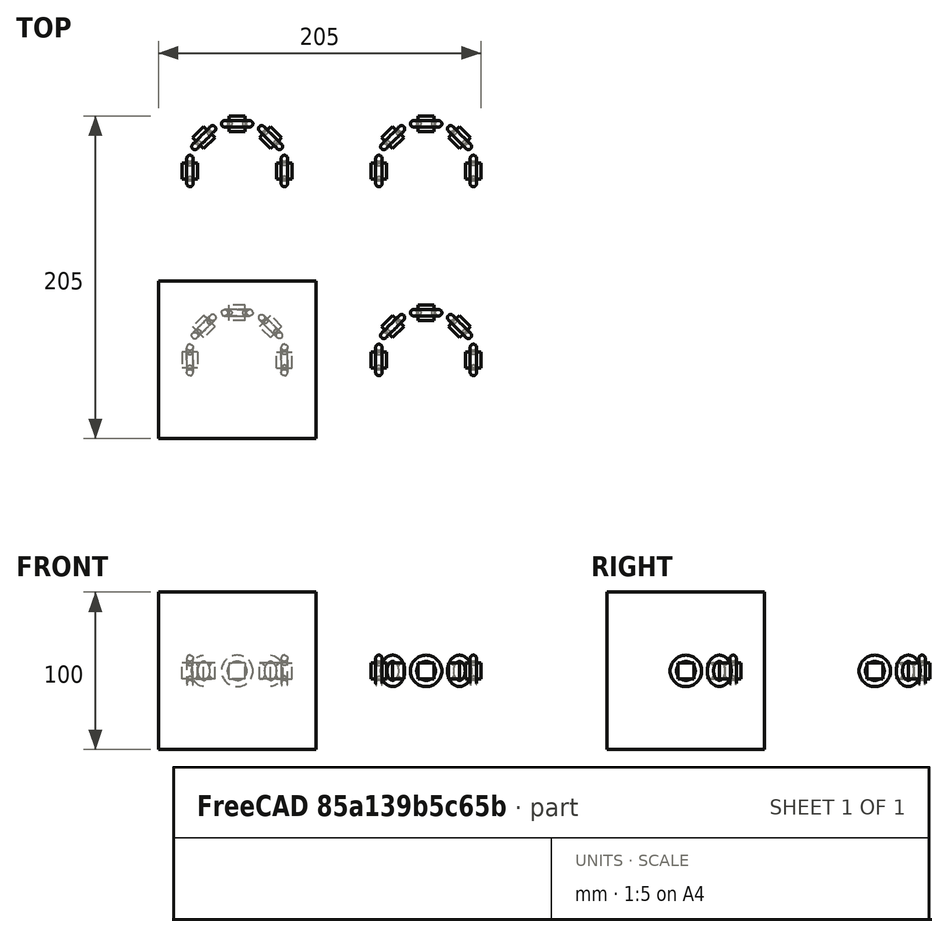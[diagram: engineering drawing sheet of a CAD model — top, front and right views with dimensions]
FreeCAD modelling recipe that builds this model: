
FCSTD DOCUMENT  (FreeCAD 1.0R39109 (Git))
Label: array-of-array-of-solid
License: All rights reserved
objects: App::DocumentObjectGroupPython×1251, Part::FeaturePython×5, App::Part×2, Part::MultiFuse×1
note: 5 computed .brp shape members not serialized (recipe doc carries the construction recipe); baked Part::Feature solids carry a one-line shape summary decoded from their .brp

FEATURE [App::DocumentObjectGroupPython] HALFPI  # scripted group (container) (typed FeaturePython)
  name = HALFPI
  value = pi/2.
FEATURE [App::DocumentObjectGroupPython] PI  # scripted group (container) (typed FeaturePython)
  name = PI
  value = 1.*pi
FEATURE [App::DocumentObjectGroupPython] TWOPI  # scripted group (container) (typed FeaturePython)
  name = TWOPI
  value = 2.*pi
FEATURE [App::DocumentObjectGroupPython] Constants  # scripted group (container) (typed FeaturePython)
  Group = -> [HALFPI,PI,TWOPI]
FEATURE [App::DocumentObjectGroupPython] Variables  # scripted group (container) (typed FeaturePython)
FEATURE [App::DocumentObjectGroupPython] Quantities  # scripted group (container) (typed FeaturePython)
FEATURE [App::DocumentObjectGroupPython] Isotopes  # scripted group (container) (typed FeaturePython)
FEATURE [App::DocumentObjectGroupPython] Elements  # scripted group (container) (typed FeaturePython)
FEATURE [App::DocumentObjectGroupPython] Matrix  # scripted group (container) (typed FeaturePython)
FEATURE [App::DocumentObjectGroupPython] Surfaces  # scripted group (container) (typed FeaturePython)
FEATURE [App::DocumentObjectGroupPython] Opticals  # scripted group (container) (typed FeaturePython)
  Group = -> [Matrix,Surfaces]
FEATURE [App::DocumentObjectGroupPython] G4Isotopes  # scripted group (container) (typed FeaturePython)
FEATURE [App::DocumentObjectGroupPython] H_element  # scripted group (container) (typed FeaturePython)
  Z = 1
  atom_value = 1.008
  formula = H
  name = H_element
FEATURE [App::DocumentObjectGroupPython] He_element  # scripted group (container) (typed FeaturePython)
  Z = 2
  atom_value = 4.0026
  formula = He
  name = He_element
FEATURE [App::DocumentObjectGroupPython] Li_element  # scripted group (container) (typed FeaturePython)
  Z = 3
  atom_value = 6.94
  formula = Li
  name = Li_element
FEATURE [App::DocumentObjectGroupPython] Be_element  # scripted group (container) (typed FeaturePython)
  Z = 4
  atom_value = 9.01218
  formula = Be
  name = Be_element
FEATURE [App::DocumentObjectGroupPython] B_element  # scripted group (container) (typed FeaturePython)
  Z = 5
  atom_value = 10.81
  formula = B
  name = B_element
FEATURE [App::DocumentObjectGroupPython] C_element  # scripted group (container) (typed FeaturePython)
  Z = 6
  atom_value = 12.011
  formula = C
  name = C_element
FEATURE [App::DocumentObjectGroupPython] N_element  # scripted group (container) (typed FeaturePython)
  Z = 7
  atom_value = 14.007
  formula = N
  name = N_element
FEATURE [App::DocumentObjectGroupPython] O_element  # scripted group (container) (typed FeaturePython)
  Z = 8
  atom_value = 15.999
  formula = O
  name = O_element
FEATURE [App::DocumentObjectGroupPython] F_element  # scripted group (container) (typed FeaturePython)
  Z = 9
  atom_value = 18.9984
  formula = F
  name = F_element
FEATURE [App::DocumentObjectGroupPython] Ne_element  # scripted group (container) (typed FeaturePython)
  Z = 10
  atom_value = 20.1797
  formula = Ne
  name = Ne_element
FEATURE [App::DocumentObjectGroupPython] Na_element  # scripted group (container) (typed FeaturePython)
  Z = 11
  atom_value = 22.9898
  formula = Na
  name = Na_element
FEATURE [App::DocumentObjectGroupPython] Mg_element  # scripted group (container) (typed FeaturePython)
  Z = 12
  atom_value = 24.305
  formula = Mg
  name = Mg_element
FEATURE [App::DocumentObjectGroupPython] Al_element  # scripted group (container) (typed FeaturePython)
  Z = 13
  atom_value = 26.9815
  formula = Al
  name = Al_element
FEATURE [App::DocumentObjectGroupPython] Si_element  # scripted group (container) (typed FeaturePython)
  Z = 14
  atom_value = 28.085
  formula = Si
  name = Si_element
FEATURE [App::DocumentObjectGroupPython] P_element  # scripted group (container) (typed FeaturePython)
  Z = 15
  atom_value = 30.9738
  formula = P
  name = P_element
FEATURE [App::DocumentObjectGroupPython] S_element  # scripted group (container) (typed FeaturePython)
  Z = 16
  atom_value = 32.06
  formula = S
  name = S_element
FEATURE [App::DocumentObjectGroupPython] Cl_element  # scripted group (container) (typed FeaturePython)
  Z = 17
  atom_value = 35.45
  formula = Cl
  name = Cl_element
FEATURE [App::DocumentObjectGroupPython] Ar_element  # scripted group (container) (typed FeaturePython)
  Z = 18
  atom_value = 39.95
  formula = Ar
  name = Ar_element
FEATURE [App::DocumentObjectGroupPython] K_element  # scripted group (container) (typed FeaturePython)
  Z = 19
  atom_value = 39.0983
  formula = K
  name = K_element
FEATURE [App::DocumentObjectGroupPython] Ca_element  # scripted group (container) (typed FeaturePython)
  Z = 20
  atom_value = 40.078
  formula = Ca
  name = Ca_element
FEATURE [App::DocumentObjectGroupPython] Sc_element  # scripted group (container) (typed FeaturePython)
  Z = 21
  atom_value = 44.9559
  formula = Sc
  name = Sc_element
FEATURE [App::DocumentObjectGroupPython] Ti_element  # scripted group (container) (typed FeaturePython)
  Z = 22
  atom_value = 47.867
  formula = Ti
  name = Ti_element
FEATURE [App::DocumentObjectGroupPython] V_element  # scripted group (container) (typed FeaturePython)
  Z = 23
  atom_value = 50.9415
  formula = V
  name = V_element
FEATURE [App::DocumentObjectGroupPython] Cr_element  # scripted group (container) (typed FeaturePython)
  Z = 24
  atom_value = 51.9961
  formula = Cr
  name = Cr_element
FEATURE [App::DocumentObjectGroupPython] Mn_element  # scripted group (container) (typed FeaturePython)
  Z = 25
  atom_value = 54.938
  formula = Mn
  name = Mn_element
FEATURE [App::DocumentObjectGroupPython] Fe_element  # scripted group (container) (typed FeaturePython)
  Z = 26
  atom_value = 55.845
  formula = Fe
  name = Fe_element
FEATURE [App::DocumentObjectGroupPython] Co_element  # scripted group (container) (typed FeaturePython)
  Z = 27
  atom_value = 58.9332
  formula = Co
  name = Co_element
FEATURE [App::DocumentObjectGroupPython] Ni_element  # scripted group (container) (typed FeaturePython)
  Z = 28
  atom_value = 58.6934
  formula = Ni
  name = Ni_element
FEATURE [App::DocumentObjectGroupPython] Cu_element  # scripted group (container) (typed FeaturePython)
  Z = 29
  atom_value = 63.546
  formula = Cu
  name = Cu_element
FEATURE [App::DocumentObjectGroupPython] Zn_element  # scripted group (container) (typed FeaturePython)
  Z = 30
  atom_value = 65.38
  formula = Zn
  name = Zn_element
FEATURE [App::DocumentObjectGroupPython] Ga_element  # scripted group (container) (typed FeaturePython)
  Z = 31
  atom_value = 69.723
  formula = Ga
  name = Ga_element
FEATURE [App::DocumentObjectGroupPython] Ge_element  # scripted group (container) (typed FeaturePython)
  Z = 32
  atom_value = 72.63
  formula = Ge
  name = Ge_element
FEATURE [App::DocumentObjectGroupPython] As_element  # scripted group (container) (typed FeaturePython)
  Z = 33
  atom_value = 74.9216
  formula = As
  name = As_element
FEATURE [App::DocumentObjectGroupPython] Se_element  # scripted group (container) (typed FeaturePython)
  Z = 34
  atom_value = 78.971
  formula = Se
  name = Se_element
FEATURE [App::DocumentObjectGroupPython] Br_element  # scripted group (container) (typed FeaturePython)
  Z = 35
  atom_value = 79.904
  formula = Br
  name = Br_element
FEATURE [App::DocumentObjectGroupPython] Kr_element  # scripted group (container) (typed FeaturePython)
  Z = 36
  atom_value = 83.798
  formula = Kr
  name = Kr_element
FEATURE [App::DocumentObjectGroupPython] Rb_element  # scripted group (container) (typed FeaturePython)
  Z = 37
  atom_value = 85.4678
  formula = Rb
  name = Rb_element
FEATURE [App::DocumentObjectGroupPython] Sr_element  # scripted group (container) (typed FeaturePython)
  Z = 38
  atom_value = 87.62
  formula = Sr
  name = Sr_element
FEATURE [App::DocumentObjectGroupPython] Y_element  # scripted group (container) (typed FeaturePython)
  Z = 39
  atom_value = 88.9058
  formula = Y
  name = Y_element
FEATURE [App::DocumentObjectGroupPython] Zr_element  # scripted group (container) (typed FeaturePython)
  Z = 40
  atom_value = 91.224
  formula = Zr
  name = Zr_element
FEATURE [App::DocumentObjectGroupPython] Nb_element  # scripted group (container) (typed FeaturePython)
  Z = 41
  atom_value = 92.9064
  formula = Nb
  name = Nb_element
FEATURE [App::DocumentObjectGroupPython] Mo_element  # scripted group (container) (typed FeaturePython)
  Z = 42
  atom_value = 95.95
  formula = Mo
  name = Mo_element
FEATURE [App::DocumentObjectGroupPython] Tc_element  # scripted group (container) (typed FeaturePython)
  Z = 43
  atom_value = 97
  formula = Tc
  name = Tc_element
FEATURE [App::DocumentObjectGroupPython] Ru_element  # scripted group (container) (typed FeaturePython)
  Z = 44
  atom_value = 101.07
  formula = Ru
  name = Ru_element
FEATURE [App::DocumentObjectGroupPython] Rh_element  # scripted group (container) (typed FeaturePython)
  Z = 45
  atom_value = 102.905
  formula = Rh
  name = Rh_element
FEATURE [App::DocumentObjectGroupPython] Pd_element  # scripted group (container) (typed FeaturePython)
  Z = 46
  atom_value = 106.42
  formula = Pd
  name = Pd_element
FEATURE [App::DocumentObjectGroupPython] Ag_element  # scripted group (container) (typed FeaturePython)
  Z = 47
  atom_value = 107.868
  formula = Ag
  name = Ag_element
FEATURE [App::DocumentObjectGroupPython] Cd_element  # scripted group (container) (typed FeaturePython)
  Z = 48
  atom_value = 112.414
  formula = Cd
  name = Cd_element
FEATURE [App::DocumentObjectGroupPython] In_element  # scripted group (container) (typed FeaturePython)
  Z = 49
  atom_value = 114.818
  formula = In
  name = In_element
FEATURE [App::DocumentObjectGroupPython] Sn_element  # scripted group (container) (typed FeaturePython)
  Z = 50
  atom_value = 118.71
  formula = Sn
  name = Sn_element
FEATURE [App::DocumentObjectGroupPython] Sb_element  # scripted group (container) (typed FeaturePython)
  Z = 51
  atom_value = 121.76
  formula = Sb
  name = Sb_element
FEATURE [App::DocumentObjectGroupPython] Te_element  # scripted group (container) (typed FeaturePython)
  Z = 52
  atom_value = 127.6
  formula = Te
  name = Te_element
FEATURE [App::DocumentObjectGroupPython] I_element  # scripted group (container) (typed FeaturePython)
  Z = 53
  atom_value = 126.904
  formula = I
  name = I_element
FEATURE [App::DocumentObjectGroupPython] Xe_element  # scripted group (container) (typed FeaturePython)
  Z = 54
  atom_value = 131.293
  formula = Xe
  name = Xe_element
FEATURE [App::DocumentObjectGroupPython] Cs_element  # scripted group (container) (typed FeaturePython)
  Z = 55
  atom_value = 132.905
  formula = Cs
  name = Cs_element
FEATURE [App::DocumentObjectGroupPython] Ba_element  # scripted group (container) (typed FeaturePython)
  Z = 56
  atom_value = 137.327
  formula = Ba
  name = Ba_element
FEATURE [App::DocumentObjectGroupPython] La_element  # scripted group (container) (typed FeaturePython)
  Z = 57
  atom_value = 138.905
  formula = La
  name = La_element
FEATURE [App::DocumentObjectGroupPython] Ce_element  # scripted group (container) (typed FeaturePython)
  Z = 58
  atom_value = 140.116
  formula = Ce
  name = Ce_element
FEATURE [App::DocumentObjectGroupPython] Pr_element  # scripted group (container) (typed FeaturePython)
  Z = 59
  atom_value = 140.908
  formula = Pr
  name = Pr_element
FEATURE [App::DocumentObjectGroupPython] Nd_element  # scripted group (container) (typed FeaturePython)
  Z = 60
  atom_value = 144.242
  formula = Nd
  name = Nd_element
FEATURE [App::DocumentObjectGroupPython] Pm_element  # scripted group (container) (typed FeaturePython)
  Z = 61
  atom_value = 145
  formula = Pm
  name = Pm_element
FEATURE [App::DocumentObjectGroupPython] Sm_element  # scripted group (container) (typed FeaturePython)
  Z = 62
  atom_value = 150.36
  formula = Sm
  name = Sm_element
FEATURE [App::DocumentObjectGroupPython] Eu_element  # scripted group (container) (typed FeaturePython)
  Z = 63
  atom_value = 151.964
  formula = Eu
  name = Eu_element
FEATURE [App::DocumentObjectGroupPython] Gd_element  # scripted group (container) (typed FeaturePython)
  Z = 64
  atom_value = 157.25
  formula = Gd
  name = Gd_element
FEATURE [App::DocumentObjectGroupPython] Tb_element  # scripted group (container) (typed FeaturePython)
  Z = 65
  atom_value = 158.925
  formula = Tb
  name = Tb_element
FEATURE [App::DocumentObjectGroupPython] Dy_element  # scripted group (container) (typed FeaturePython)
  Z = 66
  atom_value = 162.5
  formula = Dy
  name = Dy_element
FEATURE [App::DocumentObjectGroupPython] Ho_element  # scripted group (container) (typed FeaturePython)
  Z = 67
  atom_value = 164.93
  formula = Ho
  name = Ho_element
FEATURE [App::DocumentObjectGroupPython] Er_element  # scripted group (container) (typed FeaturePython)
  Z = 68
  atom_value = 167.259
  formula = Er
  name = Er_element
FEATURE [App::DocumentObjectGroupPython] Tm_element  # scripted group (container) (typed FeaturePython)
  Z = 69
  atom_value = 168.934
  formula = Tm
  name = Tm_element
FEATURE [App::DocumentObjectGroupPython] Yb_element  # scripted group (container) (typed FeaturePython)
  Z = 70
  atom_value = 173.045
  formula = Yb
  name = Yb_element
FEATURE [App::DocumentObjectGroupPython] Lu_element  # scripted group (container) (typed FeaturePython)
  Z = 71
  atom_value = 174.967
  formula = Lu
  name = Lu_element
FEATURE [App::DocumentObjectGroupPython] Hf_element  # scripted group (container) (typed FeaturePython)
  Z = 72
  atom_value = 178.49
  formula = Hf
  name = Hf_element
FEATURE [App::DocumentObjectGroupPython] Ta_element  # scripted group (container) (typed FeaturePython)
  Z = 73
  atom_value = 180.948
  formula = Ta
  name = Ta_element
FEATURE [App::DocumentObjectGroupPython] W_element  # scripted group (container) (typed FeaturePython)
  Z = 74
  atom_value = 183.84
  formula = W
  name = W_element
FEATURE [App::DocumentObjectGroupPython] Re_element  # scripted group (container) (typed FeaturePython)
  Z = 75
  atom_value = 186.207
  formula = Re
  name = Re_element
FEATURE [App::DocumentObjectGroupPython] Os_element  # scripted group (container) (typed FeaturePython)
  Z = 76
  atom_value = 190.23
  formula = Os
  name = Os_element
FEATURE [App::DocumentObjectGroupPython] Ir_element  # scripted group (container) (typed FeaturePython)
  Z = 77
  atom_value = 192.217
  formula = Ir
  name = Ir_element
FEATURE [App::DocumentObjectGroupPython] Pt_element  # scripted group (container) (typed FeaturePython)
  Z = 78
  atom_value = 195.084
  formula = Pt
  name = Pt_element
FEATURE [App::DocumentObjectGroupPython] Au_element  # scripted group (container) (typed FeaturePython)
  Z = 79
  atom_value = 196.967
  formula = Au
  name = Au_element
FEATURE [App::DocumentObjectGroupPython] Hg_element  # scripted group (container) (typed FeaturePython)
  Z = 80
  atom_value = 200.592
  formula = Hg
  name = Hg_element
FEATURE [App::DocumentObjectGroupPython] Tl_element  # scripted group (container) (typed FeaturePython)
  Z = 81
  atom_value = 204.38
  formula = Tl
  name = Tl_element
FEATURE [App::DocumentObjectGroupPython] Pb_element  # scripted group (container) (typed FeaturePython)
  Z = 82
  atom_value = 207.2
  formula = Pb
  name = Pb_element
FEATURE [App::DocumentObjectGroupPython] Bi_element  # scripted group (container) (typed FeaturePython)
  Z = 83
  atom_value = 208.98
  formula = Bi
  name = Bi_element
FEATURE [App::DocumentObjectGroupPython] Po_element  # scripted group (container) (typed FeaturePython)
  Z = 84
  atom_value = 209
  formula = Po
  name = Po_element
FEATURE [App::DocumentObjectGroupPython] At_element  # scripted group (container) (typed FeaturePython)
  Z = 85
  atom_value = 210
  formula = At
  name = At_element
FEATURE [App::DocumentObjectGroupPython] Rn_element  # scripted group (container) (typed FeaturePython)
  Z = 86
  atom_value = 222
  formula = Rn
  name = Rn_element
FEATURE [App::DocumentObjectGroupPython] Fr_element  # scripted group (container) (typed FeaturePython)
  Z = 87
  atom_value = 223
  formula = Fr
  name = Fr_element
FEATURE [App::DocumentObjectGroupPython] Ra_element  # scripted group (container) (typed FeaturePython)
  Z = 88
  atom_value = 226
  formula = Ra
  name = Ra_element
FEATURE [App::DocumentObjectGroupPython] Ac_element  # scripted group (container) (typed FeaturePython)
  Z = 89
  atom_value = 227
  formula = Ac
  name = Ac_element
FEATURE [App::DocumentObjectGroupPython] Th_element  # scripted group (container) (typed FeaturePython)
  Z = 90
  atom_value = 232.038
  formula = Th
  name = Th_element
FEATURE [App::DocumentObjectGroupPython] Pa_element  # scripted group (container) (typed FeaturePython)
  Z = 91
  atom_value = 231.036
  formula = Pa
  name = Pa_element
FEATURE [App::DocumentObjectGroupPython] U_element  # scripted group (container) (typed FeaturePython)
  Z = 92
  atom_value = 238.029
  formula = U
  name = U_element
FEATURE [App::DocumentObjectGroupPython] Np_element  # scripted group (container) (typed FeaturePython)
  Z = 93
  atom_value = 237
  formula = Np
  name = Np_element
FEATURE [App::DocumentObjectGroupPython] Pu_element  # scripted group (container) (typed FeaturePython)
  Z = 94
  atom_value = 244
  formula = Pu
  name = Pu_element
FEATURE [App::DocumentObjectGroupPython] Am_element  # scripted group (container) (typed FeaturePython)
  Z = 95
  atom_value = 243
  formula = Am
  name = Am_element
FEATURE [App::DocumentObjectGroupPython] Cm_element  # scripted group (container) (typed FeaturePython)
  Z = 96
  atom_value = 247
  formula = Cm
  name = Cm_element
FEATURE [App::DocumentObjectGroupPython] Bk_element  # scripted group (container) (typed FeaturePython)
  Z = 97
  atom_value = 247
  formula = Bk
  name = Bk_element
FEATURE [App::DocumentObjectGroupPython] Cf_element  # scripted group (container) (typed FeaturePython)
  Z = 98
  atom_value = 251
  formula = Cf
  name = Cf_element
FEATURE [App::DocumentObjectGroupPython] G4Elements  # scripted group (container) (typed FeaturePython)
  Group = -> [H_element,He_element,Li_element,Be_element,B_element,C_element,N_element,O_element,F_element,Ne_element,Na_element,Mg_element,Al_element,Si_element,P_element,S_element,Cl_element,Ar_element,K_element,Ca_element,Sc_element,Ti_element,V_element,Cr_element,Mn_element,Fe_element,Co_element,Ni_element,Cu_element,Zn_element,Ga_element,Ge_element,As_element,Se_element,Br_element,Kr_element,Rb_element,+61 more]
FEATURE [App::DocumentObjectGroupPython] H_element001  label="H_element : 0.101"  # scripted group (container) (typed FeaturePython)
  n = 0.101327
FEATURE [App::DocumentObjectGroupPython] C_element001  label="C_element : 0.775"  # scripted group (container) (typed FeaturePython)
  n = 0.7755
FEATURE [App::DocumentObjectGroupPython] N_element001  label="N_element : 0.035"  # scripted group (container) (typed FeaturePython)
  n = 0.035057
FEATURE [App::DocumentObjectGroupPython] O_element001  label="O_element : 0.052"  # scripted group (container) (typed FeaturePython)
  n = 0.0523159
FEATURE [App::DocumentObjectGroupPython] F_element001  label="F_element : 0.017"  # scripted group (container) (typed FeaturePython)
  n = 0.017422
FEATURE [App::DocumentObjectGroupPython] Ca_element001  label="Ca_element : 0.018"  # scripted group (container) (typed FeaturePython)
  n = 0.018378
FEATURE [App::DocumentObjectGroupPython] G4_A_150_TISSUE  label="G4_A-150_TISSUE"  # scripted group (container) (typed FeaturePython)
  Dunit = g/cm3
  Dvalue = 1.127
  Group = -> [H_element001,C_element001,N_element001,O_element001,F_element001,Ca_element001]
  conduct = 2
  density = 1
  expand = 3
  formula = G4_A-150_TISSUE
  name = G4_A-150_TISSUE
  specific = 4
FEATURE [App::DocumentObjectGroupPython] C_element002  label="C_element : 3"  # scripted group (container) (typed FeaturePython)
  n = 3
  ref = C_element
FEATURE [App::DocumentObjectGroupPython] H_element002  label="H_element : 6"  # scripted group (container) (typed FeaturePython)
  n = 6
  ref = H_element
FEATURE [App::DocumentObjectGroupPython] O_element002  label="O_element : 1"  # scripted group (container) (typed FeaturePython)
  n = 1
  ref = O_element
FEATURE [App::DocumentObjectGroupPython] G4_ACETONE  # scripted group (container) (typed FeaturePython)
  Dunit = g/cm3
  Dvalue = 0.7899
  Group = -> [C_element002,H_element002,O_element002]
  conduct = 2
  density = 1
  expand = 3
  formula = G4_ACETONE
  name = G4_ACETONE
  specific = 4
FEATURE [App::DocumentObjectGroupPython] C_element003  label="C_element : 2"  # scripted group (container) (typed FeaturePython)
  n = 2
  ref = C_element
FEATURE [App::DocumentObjectGroupPython] H_element003  label="H_element : 2"  # scripted group (container) (typed FeaturePython)
  n = 2
  ref = H_element
FEATURE [App::DocumentObjectGroupPython] G4_ACETYLENE  # scripted group (container) (typed FeaturePython)
  Dunit = g/cm3
  Dvalue = 0.0010967
  Group = -> [C_element003,H_element003]
  conduct = 2
  density = 1
  expand = 3
  formula = G4_ACETYLENE
  name = G4_ACETYLENE
  specific = 4
FEATURE [App::DocumentObjectGroupPython] C_element004  label="C_element : 5"  # scripted group (container) (typed FeaturePython)
  n = 5
  ref = C_element
FEATURE [App::DocumentObjectGroupPython] H_element004  label="H_element : 5"  # scripted group (container) (typed FeaturePython)
  n = 5
  ref = H_element
FEATURE [App::DocumentObjectGroupPython] N_element002  label="N_element : 5"  # scripted group (container) (typed FeaturePython)
  n = 5
  ref = N_element
FEATURE [App::DocumentObjectGroupPython] G4_ADENINE  # scripted group (container) (typed FeaturePython)
  Dunit = g/cm3
  Dvalue = 1.6
  Group = -> [C_element004,H_element004,N_element002]
  conduct = 2
  density = 1
  expand = 3
  formula = G4_ADENINE
  name = G4_ADENINE
  specific = 4
FEATURE [App::DocumentObjectGroupPython] H_element005  label="H_element : 0.114"  # scripted group (container) (typed FeaturePython)
  n = 0.114
FEATURE [App::DocumentObjectGroupPython] C_element005  label="C_element : 0.598"  # scripted group (container) (typed FeaturePython)
  n = 0.598
FEATURE [App::DocumentObjectGroupPython] N_element003  label="N_element : 0.007"  # scripted group (container) (typed FeaturePython)
  n = 0.007
FEATURE [App::DocumentObjectGroupPython] O_element003  label="O_element : 0.278"  # scripted group (container) (typed FeaturePython)
  n = 0.278
FEATURE [App::DocumentObjectGroupPython] Na_element001  label="Na_element : 0.001"  # scripted group (container) (typed FeaturePython)
  n = 0.001
FEATURE [App::DocumentObjectGroupPython] S_element001  label="S_element : 0.001"  # scripted group (container) (typed FeaturePython)
  n = 0.001
FEATURE [App::DocumentObjectGroupPython] Cl_element001  label="Cl_element : 0.001"  # scripted group (container) (typed FeaturePython)
  n = 0.001
FEATURE [App::DocumentObjectGroupPython] G4_ADIPOSE_TISSUE_ICRP  # scripted group (container) (typed FeaturePython)
  Dunit = g/cm3
  Dvalue = 0.95
  Group = -> [H_element005,C_element005,N_element003,O_element003,Na_element001,S_element001,Cl_element001]
  conduct = 2
  density = 1
  expand = 3
  formula = G4_ADIPOSE_TISSUE_ICRP
  name = G4_ADIPOSE_TISSUE_ICRP
  specific = 4
FEATURE [App::DocumentObjectGroupPython] C_element006  label="C_element : 0.000"  # scripted group (container) (typed FeaturePython)
  n = 0.000124
FEATURE [App::DocumentObjectGroupPython] N_element004  label="N_element : 0.755"  # scripted group (container) (typed FeaturePython)
  n = 0.755268
FEATURE [App::DocumentObjectGroupPython] O_element004  label="O_element : 0.232"  # scripted group (container) (typed FeaturePython)
  n = 0.231781
FEATURE [App::DocumentObjectGroupPython] Ar_element001  label="Ar_element : 0.013"  # scripted group (container) (typed FeaturePython)
  n = 0.012827
FEATURE [App::DocumentObjectGroupPython] G4_AIR  # scripted group (container) (typed FeaturePython)
  Dunit = g/cm3
  Dvalue = 0.00120479
  Group = -> [C_element006,N_element004,O_element004,Ar_element001]
  conduct = 2
  density = 1
  expand = 3
  formula = G4_AIR
  name = G4_AIR
  specific = 4
FEATURE [App::DocumentObjectGroupPython] C_element007  label="C_element : 006"  # scripted group (container) (typed FeaturePython)
  n = 3
  ref = C_element
FEATURE [App::DocumentObjectGroupPython] H_element006  label="H_element : 7"  # scripted group (container) (typed FeaturePython)
  n = 7
  ref = H_element
FEATURE [App::DocumentObjectGroupPython] N_element005  label="N_element : 1"  # scripted group (container) (typed FeaturePython)
  n = 1
  ref = N_element
FEATURE [App::DocumentObjectGroupPython] O_element005  label="O_element : 2"  # scripted group (container) (typed FeaturePython)
  n = 2
  ref = O_element
FEATURE [App::DocumentObjectGroupPython] G4_ALANINE  # scripted group (container) (typed FeaturePython)
  Dunit = g/cm3
  Dvalue = 1.42
  Group = -> [C_element007,H_element006,N_element005,O_element005]
  conduct = 2
  density = 1
  expand = 3
  formula = G4_ALANINE
  name = G4_ALANINE
  specific = 4
FEATURE [App::DocumentObjectGroupPython] Al_element001  label="Al_element : 2"  # scripted group (container) (typed FeaturePython)
  n = 2
  ref = Al_element
FEATURE [App::DocumentObjectGroupPython] O_element006  label="O_element : 3"  # scripted group (container) (typed FeaturePython)
  n = 3
  ref = O_element
FEATURE [App::DocumentObjectGroupPython] G4_ALUMINUM_OXIDE  # scripted group (container) (typed FeaturePython)
  Dunit = g/cm3
  Dvalue = 3.97
  Group = -> [Al_element001,O_element006]
  conduct = 2
  density = 1
  expand = 3
  formula = G4_ALUMINUM_OXIDE
  name = G4_ALUMINUM_OXIDE
  specific = 4
FEATURE [App::DocumentObjectGroupPython] H_element007  label="H_element : 0.106"  # scripted group (container) (typed FeaturePython)
  n = 0.10593
FEATURE [App::DocumentObjectGroupPython] C_element008  label="C_element : 0.789"  # scripted group (container) (typed FeaturePython)
  n = 0.788974
FEATURE [App::DocumentObjectGroupPython] O_element007  label="O_element : 0.105"  # scripted group (container) (typed FeaturePython)
  n = 0.105096
FEATURE [App::DocumentObjectGroupPython] G4_AMBER  # scripted group (container) (typed FeaturePython)
  Dunit = g/cm3
  Dvalue = 1.1
  Group = -> [H_element007,C_element008,O_element007]
  conduct = 2
  density = 1
  expand = 3
  formula = G4_AMBER
  name = G4_AMBER
  specific = 4
FEATURE [App::DocumentObjectGroupPython] N_element006  label="N_element : 006"  # scripted group (container) (typed FeaturePython)
  n = 1
  ref = N_element
FEATURE [App::DocumentObjectGroupPython] H_element008  label="H_element : 3"  # scripted group (container) (typed FeaturePython)
  n = 3
  ref = H_element
FEATURE [App::DocumentObjectGroupPython] G4_AMMONIA  # scripted group (container) (typed FeaturePython)
  Dunit = g/cm3
  Dvalue = 0.000826019
  Group = -> [N_element006,H_element008]
  conduct = 2
  density = 1
  expand = 3
  formula = G4_AMMONIA
  name = G4_AMMONIA
  specific = 4
FEATURE [App::DocumentObjectGroupPython] C_element009  label="C_element : 6"  # scripted group (container) (typed FeaturePython)
  n = 6
  ref = C_element
FEATURE [App::DocumentObjectGroupPython] H_element009  label="H_element : 008"  # scripted group (container) (typed FeaturePython)
  n = 7
  ref = H_element
FEATURE [App::DocumentObjectGroupPython] N_element007  label="N_element : 007"  # scripted group (container) (typed FeaturePython)
  n = 1
  ref = N_element
FEATURE [App::DocumentObjectGroupPython] G4_ANILINE  # scripted group (container) (typed FeaturePython)
  Dunit = g/cm3
  Dvalue = 1.0235
  Group = -> [C_element009,H_element009,N_element007]
  conduct = 2
  density = 1
  expand = 3
  formula = G4_ANILINE
  name = G4_ANILINE
  specific = 4
FEATURE [App::DocumentObjectGroupPython] C_element010  label="C_element : 14"  # scripted group (container) (typed FeaturePython)
  n = 14
  ref = C_element
FEATURE [App::DocumentObjectGroupPython] H_element010  label="H_element : 10"  # scripted group (container) (typed FeaturePython)
  n = 10
  ref = H_element
FEATURE [App::DocumentObjectGroupPython] G4_ANTHRACENE  # scripted group (container) (typed FeaturePython)
  Dunit = g/cm3
  Dvalue = 1.283
  Group = -> [C_element010,H_element010]
  conduct = 2
  density = 1
  expand = 3
  formula = G4_ANTHRACENE
  name = G4_ANTHRACENE
  specific = 4
FEATURE [App::DocumentObjectGroupPython] H_element011  label="H_element : 0.065"  # scripted group (container) (typed FeaturePython)
  n = 0.0654709
FEATURE [App::DocumentObjectGroupPython] C_element011  label="C_element : 0.537"  # scripted group (container) (typed FeaturePython)
  n = 0.536944
FEATURE [App::DocumentObjectGroupPython] N_element008  label="N_element : 0.021"  # scripted group (container) (typed FeaturePython)
  n = 0.0215
FEATURE [App::DocumentObjectGroupPython] O_element008  label="O_element : 0.032"  # scripted group (container) (typed FeaturePython)
  n = 0.032085
FEATURE [App::DocumentObjectGroupPython] F_element002  label="F_element : 0.167"  # scripted group (container) (typed FeaturePython)
  n = 0.167411
FEATURE [App::DocumentObjectGroupPython] Ca_element002  label="Ca_element : 0.177"  # scripted group (container) (typed FeaturePython)
  n = 0.176589
FEATURE [App::DocumentObjectGroupPython] G4_B_100_BONE  label="G4_B-100_BONE"  # scripted group (container) (typed FeaturePython)
  Dunit = g/cm3
  Dvalue = 1.45
  Group = -> [H_element011,C_element011,N_element008,O_element008,F_element002,Ca_element002]
  conduct = 2
  density = 1
  expand = 3
  formula = G4_B-100_BONE
  name = G4_B-100_BONE
  specific = 4
FEATURE [App::DocumentObjectGroupPython] H_element012  label="H_element : 0.057"  # scripted group (container) (typed FeaturePython)
  n = 0.057441
FEATURE [App::DocumentObjectGroupPython] C_element012  label="C_element : 0.790"  # scripted group (container) (typed FeaturePython)
  n = 0.774591
FEATURE [App::DocumentObjectGroupPython] O_element009  label="O_element : 0.168"  # scripted group (container) (typed FeaturePython)
  n = 0.167968
FEATURE [App::DocumentObjectGroupPython] G4_BAKELITE  # scripted group (container) (typed FeaturePython)
  Dunit = g/cm3
  Dvalue = 1.25
  Group = -> [H_element012,C_element012,O_element009]
  conduct = 2
  density = 1
  expand = 3
  formula = G4_BAKELITE
  name = G4_BAKELITE
  specific = 4
FEATURE [App::DocumentObjectGroupPython] Ba_element001  label="Ba_element : 1"  # scripted group (container) (typed FeaturePython)
  n = 1
  ref = Ba_element
FEATURE [App::DocumentObjectGroupPython] F_element003  label="F_element : 2"  # scripted group (container) (typed FeaturePython)
  n = 2
  ref = F_element
FEATURE [App::DocumentObjectGroupPython] G4_BARIUM_FLUORIDE  # scripted group (container) (typed FeaturePython)
  Dunit = g/cm3
  Dvalue = 4.89
  Group = -> [Ba_element001,F_element003]
  conduct = 2
  density = 1
  expand = 3
  formula = G4_BARIUM_FLUORIDE
  name = G4_BARIUM_FLUORIDE
  specific = 4
FEATURE [App::DocumentObjectGroupPython] Ba_element002  label="Ba_element : 002"  # scripted group (container) (typed FeaturePython)
  n = 1
  ref = Ba_element
FEATURE [App::DocumentObjectGroupPython] S_element002  label="S_element : 1"  # scripted group (container) (typed FeaturePython)
  n = 1
  ref = S_element
FEATURE [App::DocumentObjectGroupPython] O_element010  label="O_element : 4"  # scripted group (container) (typed FeaturePython)
  n = 4
  ref = O_element
FEATURE [App::DocumentObjectGroupPython] G4_BARIUM_SULFATE  # scripted group (container) (typed FeaturePython)
  Dunit = g/cm3
  Dvalue = 4.5
  Group = -> [Ba_element002,S_element002,O_element010]
  conduct = 2
  density = 1
  expand = 3
  formula = G4_BARIUM_SULFATE
  name = G4_BARIUM_SULFATE
  specific = 4
FEATURE [App::DocumentObjectGroupPython] C_element013  label="C_element : 007"  # scripted group (container) (typed FeaturePython)
  n = 6
  ref = C_element
FEATURE [App::DocumentObjectGroupPython] H_element013  label="H_element : 009"  # scripted group (container) (typed FeaturePython)
  n = 6
  ref = H_element
FEATURE [App::DocumentObjectGroupPython] G4_BENZENE  # scripted group (container) (typed FeaturePython)
  Dunit = g/cm3
  Dvalue = 0.87865
  Group = -> [C_element013,H_element013]
  conduct = 2
  density = 1
  expand = 3
  formula = G4_BENZENE
  name = G4_BENZENE
  specific = 4
FEATURE [App::DocumentObjectGroupPython] Be_element001  label="Be_element : 1"  # scripted group (container) (typed FeaturePython)
  n = 1
  ref = Be_element
FEATURE [App::DocumentObjectGroupPython] O_element011  label="O_element : 005"  # scripted group (container) (typed FeaturePython)
  n = 1
  ref = O_element
FEATURE [App::DocumentObjectGroupPython] G4_BERYLLIUM_OXIDE  # scripted group (container) (typed FeaturePython)
  Dunit = g/cm3
  Dvalue = 3.01
  Group = -> [Be_element001,O_element011]
  conduct = 2
  density = 1
  expand = 3
  formula = G4_BERYLLIUM_OXIDE
  name = G4_BERYLLIUM_OXIDE
  specific = 4
FEATURE [App::DocumentObjectGroupPython] Bi_element001  label="Bi_element : 4"  # scripted group (container) (typed FeaturePython)
  n = 4
  ref = Bi_element
FEATURE [App::DocumentObjectGroupPython] Ge_element001  label="Ge_element : 3"  # scripted group (container) (typed FeaturePython)
  n = 3
  ref = Ge_element
FEATURE [App::DocumentObjectGroupPython] O_element012  label="O_element : 12"  # scripted group (container) (typed FeaturePython)
  n = 12
  ref = O_element
FEATURE [App::DocumentObjectGroupPython] G4_BGO  # scripted group (container) (typed FeaturePython)
  Dunit = g/cm3
  Dvalue = 7.13
  Group = -> [Bi_element001,Ge_element001,O_element012]
  conduct = 2
  density = 1
  expand = 3
  formula = G4_BGO
  name = G4_BGO
  specific = 4
FEATURE [App::DocumentObjectGroupPython] H_element014  label="H_element : 0.102"  # scripted group (container) (typed FeaturePython)
  n = 0.102
FEATURE [App::DocumentObjectGroupPython] C_element014  label="C_element : 0.110"  # scripted group (container) (typed FeaturePython)
  n = 0.11
FEATURE [App::DocumentObjectGroupPython] N_element009  label="N_element : 0.033"  # scripted group (container) (typed FeaturePython)
  n = 0.033
FEATURE [App::DocumentObjectGroupPython] O_element013  label="O_element : 0.745"  # scripted group (container) (typed FeaturePython)
  n = 0.745
FEATURE [App::DocumentObjectGroupPython] Na_element002  label="Na_element : 0.002"  # scripted group (container) (typed FeaturePython)
  n = 0.001
FEATURE [App::DocumentObjectGroupPython] P_element001  label="P_element : 0.001"  # scripted group (container) (typed FeaturePython)
  n = 0.001
FEATURE [App::DocumentObjectGroupPython] S_element003  label="S_element : 0.002"  # scripted group (container) (typed FeaturePython)
  n = 0.002
FEATURE [App::DocumentObjectGroupPython] Cl_element002  label="Cl_element : 0.003"  # scripted group (container) (typed FeaturePython)
  n = 0.003
FEATURE [App::DocumentObjectGroupPython] K_element001  label="K_element : 0.002"  # scripted group (container) (typed FeaturePython)
  n = 0.002
FEATURE [App::DocumentObjectGroupPython] Fe_element001  label="Fe_element : 0.001"  # scripted group (container) (typed FeaturePython)
  n = 0.001
FEATURE [App::DocumentObjectGroupPython] G4_BLOOD_ICRP  # scripted group (container) (typed FeaturePython)
  Dunit = g/cm3
  Dvalue = 1.06
  Group = -> [H_element014,C_element014,N_element009,O_element013,Na_element002,P_element001,S_element003,Cl_element002,K_element001,Fe_element001]
  conduct = 2
  density = 1
  expand = 3
  formula = G4_BLOOD_ICRP
  name = G4_BLOOD_ICRP
  specific = 4
FEATURE [App::DocumentObjectGroupPython] H_element015  label="H_element : 0.064"  # scripted group (container) (typed FeaturePython)
  n = 0.064
FEATURE [App::DocumentObjectGroupPython] C_element015  label="C_element : 0.278"  # scripted group (container) (typed FeaturePython)
  n = 0.278
FEATURE [App::DocumentObjectGroupPython] N_element010  label="N_element : 0.027"  # scripted group (container) (typed FeaturePython)
  n = 0.027
FEATURE [App::DocumentObjectGroupPython] O_element014  label="O_element : 0.410"  # scripted group (container) (typed FeaturePython)
  n = 0.41
FEATURE [App::DocumentObjectGroupPython] Mg_element001  label="Mg_element : 0.002"  # scripted group (container) (typed FeaturePython)
  n = 0.002
FEATURE [App::DocumentObjectGroupPython] P_element002  label="P_element : 0.070"  # scripted group (container) (typed FeaturePython)
  n = 0.07
FEATURE [App::DocumentObjectGroupPython] S_element004  label="S_element : 0.003"  # scripted group (container) (typed FeaturePython)
  n = 0.002
FEATURE [App::DocumentObjectGroupPython] Ca_element003  label="Ca_element : 0.147"  # scripted group (container) (typed FeaturePython)
  n = 0.147
FEATURE [App::DocumentObjectGroupPython] G4_BONE_COMPACT_ICRU  # scripted group (container) (typed FeaturePython)
  Dunit = g/cm3
  Dvalue = 1.85
  Group = -> [H_element015,C_element015,N_element010,O_element014,Mg_element001,P_element002,S_element004,Ca_element003]
  conduct = 2
  density = 1
  expand = 3
  formula = G4_BONE_COMPACT_ICRU
  name = G4_BONE_COMPACT_ICRU
  specific = 4
FEATURE [App::DocumentObjectGroupPython] H_element016  label="H_element : 0.034"  # scripted group (container) (typed FeaturePython)
  n = 0.034
FEATURE [App::DocumentObjectGroupPython] C_element016  label="C_element : 0.155"  # scripted group (container) (typed FeaturePython)
  n = 0.155
FEATURE [App::DocumentObjectGroupPython] N_element011  label="N_element : 0.042"  # scripted group (container) (typed FeaturePython)
  n = 0.042
FEATURE [App::DocumentObjectGroupPython] O_element015  label="O_element : 0.435"  # scripted group (container) (typed FeaturePython)
  n = 0.435
FEATURE [App::DocumentObjectGroupPython] Na_element003  label="Na_element : 0.003"  # scripted group (container) (typed FeaturePython)
  n = 0.001
FEATURE [App::DocumentObjectGroupPython] Mg_element002  label="Mg_element : 0.003"  # scripted group (container) (typed FeaturePython)
  n = 0.002
FEATURE [App::DocumentObjectGroupPython] P_element003  label="P_element : 0.103"  # scripted group (container) (typed FeaturePython)
  n = 0.103
FEATURE [App::DocumentObjectGroupPython] S_element005  label="S_element : 0.004"  # scripted group (container) (typed FeaturePython)
  n = 0.003
FEATURE [App::DocumentObjectGroupPython] Ca_element004  label="Ca_element : 0.225"  # scripted group (container) (typed FeaturePython)
  n = 0.225
FEATURE [App::DocumentObjectGroupPython] G4_BONE_CORTICAL_ICRP  # scripted group (container) (typed FeaturePython)
  Dunit = g/cm3
  Dvalue = 1.92
  Group = -> [H_element016,C_element016,N_element011,O_element015,Na_element003,Mg_element002,P_element003,S_element005,Ca_element004]
  conduct = 2
  density = 1
  expand = 3
  formula = G4_BONE_CORTICAL_ICRP
  name = G4_BONE_CORTICAL_ICRP
  specific = 4
FEATURE [App::DocumentObjectGroupPython] B_element001  label="B_element : 4"  # scripted group (container) (typed FeaturePython)
  n = 4
  ref = B_element
FEATURE [App::DocumentObjectGroupPython] C_element017  label="C_element : 1"  # scripted group (container) (typed FeaturePython)
  n = 1
  ref = C_element
FEATURE [App::DocumentObjectGroupPython] G4_BORON_CARBIDE  # scripted group (container) (typed FeaturePython)
  Dunit = g/cm3
  Dvalue = 2.52
  Group = -> [B_element001,C_element017]
  conduct = 2
  density = 1
  expand = 3
  formula = G4_BORON_CARBIDE
  name = G4_BORON_CARBIDE
  specific = 4
FEATURE [App::DocumentObjectGroupPython] B_element002  label="B_element : 2"  # scripted group (container) (typed FeaturePython)
  n = 2
  ref = B_element
FEATURE [App::DocumentObjectGroupPython] O_element016  label="O_element : 006"  # scripted group (container) (typed FeaturePython)
  n = 3
  ref = O_element
FEATURE [App::DocumentObjectGroupPython] G4_BORON_OXIDE  # scripted group (container) (typed FeaturePython)
  Dunit = g/cm3
  Dvalue = 1.812
  Group = -> [B_element002,O_element016]
  conduct = 2
  density = 1
  expand = 3
  formula = G4_BORON_OXIDE
  name = G4_BORON_OXIDE
  specific = 4
FEATURE [App::DocumentObjectGroupPython] H_element017  label="H_element : 0.107"  # scripted group (container) (typed FeaturePython)
  n = 0.107
FEATURE [App::DocumentObjectGroupPython] C_element018  label="C_element : 0.145"  # scripted group (container) (typed FeaturePython)
  n = 0.145
FEATURE [App::DocumentObjectGroupPython] N_element012  label="N_element : 0.022"  # scripted group (container) (typed FeaturePython)
  n = 0.022
FEATURE [App::DocumentObjectGroupPython] O_element017  label="O_element : 0.712"  # scripted group (container) (typed FeaturePython)
  n = 0.712
FEATURE [App::DocumentObjectGroupPython] Na_element004  label="Na_element : 0.004"  # scripted group (container) (typed FeaturePython)
  n = 0.002
FEATURE [App::DocumentObjectGroupPython] P_element004  label="P_element : 0.004"  # scripted group (container) (typed FeaturePython)
  n = 0.004
FEATURE [App::DocumentObjectGroupPython] S_element006  label="S_element : 0.005"  # scripted group (container) (typed FeaturePython)
  n = 0.002
FEATURE [App::DocumentObjectGroupPython] Cl_element003  label="Cl_element : 0.004"  # scripted group (container) (typed FeaturePython)
  n = 0.003
FEATURE [App::DocumentObjectGroupPython] K_element002  label="K_element : 0.003"  # scripted group (container) (typed FeaturePython)
  n = 0.003
FEATURE [App::DocumentObjectGroupPython] G4_BRAIN_ICRP  # scripted group (container) (typed FeaturePython)
  Dunit = g/cm3
  Dvalue = 1.04
  Group = -> [H_element017,C_element018,N_element012,O_element017,Na_element004,P_element004,S_element006,Cl_element003,K_element002]
  conduct = 2
  density = 1
  expand = 3
  formula = G4_BRAIN_ICRP
  name = G4_BRAIN_ICRP
  specific = 4
FEATURE [App::DocumentObjectGroupPython] C_element019  label="C_element : 4"  # scripted group (container) (typed FeaturePython)
  n = 4
  ref = C_element
FEATURE [App::DocumentObjectGroupPython] H_element018  label="H_element : 010"  # scripted group (container) (typed FeaturePython)
  n = 10
  ref = H_element
FEATURE [App::DocumentObjectGroupPython] G4_BUTANE  # scripted group (container) (typed FeaturePython)
  Dunit = g/cm3
  Dvalue = 0.00249343
  Group = -> [C_element019,H_element018]
  conduct = 2
  density = 1
  expand = 3
  formula = G4_BUTANE
  name = G4_BUTANE
  specific = 4
FEATURE [App::DocumentObjectGroupPython] C_element020  label="C_element : 008"  # scripted group (container) (typed FeaturePython)
  n = 4
  ref = C_element
FEATURE [App::DocumentObjectGroupPython] H_element019  label="H_element : 011"  # scripted group (container) (typed FeaturePython)
  n = 10
  ref = H_element
FEATURE [App::DocumentObjectGroupPython] O_element018  label="O_element : 007"  # scripted group (container) (typed FeaturePython)
  n = 1
  ref = O_element
FEATURE [App::DocumentObjectGroupPython] G4_N_BUTYL_ALCOHOL  label="G4_N-BUTYL_ALCOHOL"  # scripted group (container) (typed FeaturePython)
  Dunit = g/cm3
  Dvalue = 0.8098
  Group = -> [C_element020,H_element019,O_element018]
  conduct = 2
  density = 1
  expand = 3
  formula = G4_N-BUTYL_ALCOHOL
  name = G4_N-BUTYL_ALCOHOL
  specific = 4
FEATURE [App::DocumentObjectGroupPython] H_element020  label="H_element : 0.025"  # scripted group (container) (typed FeaturePython)
  n = 0.02468
FEATURE [App::DocumentObjectGroupPython] C_element021  label="C_element : 0.502"  # scripted group (container) (typed FeaturePython)
  n = 0.501611
FEATURE [App::DocumentObjectGroupPython] O_element019  label="O_element : 0.005"  # scripted group (container) (typed FeaturePython)
  n = 0.004527
FEATURE [App::DocumentObjectGroupPython] F_element004  label="F_element : 0.465"  # scripted group (container) (typed FeaturePython)
  n = 0.465209
FEATURE [App::DocumentObjectGroupPython] Si_element001  label="Si_element : 0.004"  # scripted group (container) (typed FeaturePython)
  n = 0.003973
FEATURE [App::DocumentObjectGroupPython] G4_C_552  label="G4_C-552"  # scripted group (container) (typed FeaturePython)
  Dunit = g/cm3
  Dvalue = 1.76
  Group = -> [H_element020,C_element021,O_element019,F_element004,Si_element001]
  conduct = 2
  density = 1
  expand = 3
  formula = G4_C-552
  name = G4_C-552
  specific = 4
FEATURE [App::DocumentObjectGroupPython] Cd_element001  label="Cd_element : 1"  # scripted group (container) (typed FeaturePython)
  n = 1
  ref = Cd_element
FEATURE [App::DocumentObjectGroupPython] Te_element001  label="Te_element : 1"  # scripted group (container) (typed FeaturePython)
  n = 1
  ref = Te_element
FEATURE [App::DocumentObjectGroupPython] G4_CADMIUM_TELLURIDE  # scripted group (container) (typed FeaturePython)
  Dunit = g/cm3
  Dvalue = 6.2
  Group = -> [Cd_element001,Te_element001]
  conduct = 2
  density = 1
  expand = 3
  formula = G4_CADMIUM_TELLURIDE
  name = G4_CADMIUM_TELLURIDE
  specific = 4
FEATURE [App::DocumentObjectGroupPython] Cd_element002  label="Cd_element : 002"  # scripted group (container) (typed FeaturePython)
  n = 1
  ref = Cd_element
FEATURE [App::DocumentObjectGroupPython] W_element001  label="W_element : 1"  # scripted group (container) (typed FeaturePython)
  n = 1
  ref = W_element
FEATURE [App::DocumentObjectGroupPython] O_element020  label="O_element : 008"  # scripted group (container) (typed FeaturePython)
  n = 4
  ref = O_element
FEATURE [App::DocumentObjectGroupPython] G4_CADMIUM_TUNGSTATE  # scripted group (container) (typed FeaturePython)
  Dunit = g/cm3
  Dvalue = 7.9
  Group = -> [Cd_element002,W_element001,O_element020]
  conduct = 2
  density = 1
  expand = 3
  formula = G4_CADMIUM_TUNGSTATE
  name = G4_CADMIUM_TUNGSTATE
  specific = 4
FEATURE [App::DocumentObjectGroupPython] Ca_element005  label="Ca_element : 1"  # scripted group (container) (typed FeaturePython)
  n = 1
  ref = Ca_element
FEATURE [App::DocumentObjectGroupPython] C_element022  label="C_element : 009"  # scripted group (container) (typed FeaturePython)
  n = 1
  ref = C_element
FEATURE [App::DocumentObjectGroupPython] O_element021  label="O_element : 009"  # scripted group (container) (typed FeaturePython)
  n = 3
  ref = O_element
FEATURE [App::DocumentObjectGroupPython] G4_CALCIUM_CARBONATE  # scripted group (container) (typed FeaturePython)
  Dunit = g/cm3
  Dvalue = 2.8
  Group = -> [Ca_element005,C_element022,O_element021]
  conduct = 2
  density = 1
  expand = 3
  formula = G4_CALCIUM_CARBONATE
  name = G4_CALCIUM_CARBONATE
  specific = 4
FEATURE [App::DocumentObjectGroupPython] Ca_element006  label="Ca_element : 002"  # scripted group (container) (typed FeaturePython)
  n = 1
  ref = Ca_element
FEATURE [App::DocumentObjectGroupPython] F_element005  label="F_element : 003"  # scripted group (container) (typed FeaturePython)
  n = 2
  ref = F_element
FEATURE [App::DocumentObjectGroupPython] G4_CALCIUM_FLUORIDE  # scripted group (container) (typed FeaturePython)
  Dunit = g/cm3
  Dvalue = 3.18
  Group = -> [Ca_element006,F_element005]
  conduct = 2
  density = 1
  expand = 3
  formula = G4_CALCIUM_FLUORIDE
  name = G4_CALCIUM_FLUORIDE
  specific = 4
FEATURE [App::DocumentObjectGroupPython] Ca_element007  label="Ca_element : 003"  # scripted group (container) (typed FeaturePython)
  n = 1
  ref = Ca_element
FEATURE [App::DocumentObjectGroupPython] O_element022  label="O_element : 010"  # scripted group (container) (typed FeaturePython)
  n = 1
  ref = O_element
FEATURE [App::DocumentObjectGroupPython] G4_CALCIUM_OXIDE  # scripted group (container) (typed FeaturePython)
  Dunit = g/cm3
  Dvalue = 3.3
  Group = -> [Ca_element007,O_element022]
  conduct = 2
  density = 1
  expand = 3
  formula = G4_CALCIUM_OXIDE
  name = G4_CALCIUM_OXIDE
  specific = 4
FEATURE [App::DocumentObjectGroupPython] Ca_element008  label="Ca_element : 004"  # scripted group (container) (typed FeaturePython)
  n = 1
  ref = Ca_element
FEATURE [App::DocumentObjectGroupPython] S_element007  label="S_element : 002"  # scripted group (container) (typed FeaturePython)
  n = 1
  ref = S_element
FEATURE [App::DocumentObjectGroupPython] O_element023  label="O_element : 011"  # scripted group (container) (typed FeaturePython)
  n = 4
  ref = O_element
FEATURE [App::DocumentObjectGroupPython] G4_CALCIUM_SULFATE  # scripted group (container) (typed FeaturePython)
  Dunit = g/cm3
  Dvalue = 2.96
  Group = -> [Ca_element008,S_element007,O_element023]
  conduct = 2
  density = 1
  expand = 3
  formula = G4_CALCIUM_SULFATE
  name = G4_CALCIUM_SULFATE
  specific = 4
FEATURE [App::DocumentObjectGroupPython] Ca_element009  label="Ca_element : 005"  # scripted group (container) (typed FeaturePython)
  n = 1
  ref = Ca_element
FEATURE [App::DocumentObjectGroupPython] W_element002  label="W_element : 002"  # scripted group (container) (typed FeaturePython)
  n = 1
  ref = W_element
FEATURE [App::DocumentObjectGroupPython] O_element024  label="O_element : 012"  # scripted group (container) (typed FeaturePython)
  n = 4
  ref = O_element
FEATURE [App::DocumentObjectGroupPython] G4_CALCIUM_TUNGSTATE  # scripted group (container) (typed FeaturePython)
  Dunit = g/cm3
  Dvalue = 6.062
  Group = -> [Ca_element009,W_element002,O_element024]
  conduct = 2
  density = 1
  expand = 3
  formula = G4_CALCIUM_TUNGSTATE
  name = G4_CALCIUM_TUNGSTATE
  specific = 4
FEATURE [App::DocumentObjectGroupPython] C_element023  label="C_element : 010"  # scripted group (container) (typed FeaturePython)
  n = 1
  ref = C_element
FEATURE [App::DocumentObjectGroupPython] O_element025  label="O_element : 013"  # scripted group (container) (typed FeaturePython)
  n = 2
  ref = O_element
FEATURE [App::DocumentObjectGroupPython] G4_CARBON_DIOXIDE  # scripted group (container) (typed FeaturePython)
  Dunit = g/cm3
  Dvalue = 0.00184212
  Group = -> [C_element023,O_element025]
  conduct = 2
  density = 1
  expand = 3
  formula = G4_CARBON_DIOXIDE
  name = G4_CARBON_DIOXIDE
  specific = 4
FEATURE [App::DocumentObjectGroupPython] C_element024  label="C_element : 011"  # scripted group (container) (typed FeaturePython)
  n = 1
  ref = C_element
FEATURE [App::DocumentObjectGroupPython] Cl_element004  label="Cl_element : 4"  # scripted group (container) (typed FeaturePython)
  n = 4
  ref = Cl_element
FEATURE [App::DocumentObjectGroupPython] G4_CARBON_TETRACHLORIDE  # scripted group (container) (typed FeaturePython)
  Dunit = g/cm3
  Dvalue = 1.594
  Group = -> [C_element024,Cl_element004]
  conduct = 2
  density = 1
  expand = 3
  formula = G4_CARBON_TETRACHLORIDE
  name = G4_CARBON_TETRACHLORIDE
  specific = 4
FEATURE [App::DocumentObjectGroupPython] C_element025  label="C_element : 012"  # scripted group (container) (typed FeaturePython)
  n = 6
  ref = C_element
FEATURE [App::DocumentObjectGroupPython] H_element021  label="H_element : 012"  # scripted group (container) (typed FeaturePython)
  n = 10
  ref = H_element
FEATURE [App::DocumentObjectGroupPython] O_element026  label="O_element : 5"  # scripted group (container) (typed FeaturePython)
  n = 5
  ref = O_element
FEATURE [App::DocumentObjectGroupPython] G4_CELLULOSE_CELLOPHANE  # scripted group (container) (typed FeaturePython)
  Dunit = g/cm3
  Dvalue = 1.42
  Group = -> [C_element025,H_element021,O_element026]
  conduct = 2
  density = 1
  expand = 3
  formula = G4_CELLULOSE_CELLOPHANE
  name = G4_CELLULOSE_CELLOPHANE
  specific = 4
FEATURE [App::DocumentObjectGroupPython] H_element022  label="H_element : 0.067"  # scripted group (container) (typed FeaturePython)
  n = 0.067125
FEATURE [App::DocumentObjectGroupPython] C_element026  label="C_element : 0.545"  # scripted group (container) (typed FeaturePython)
  n = 0.545403
FEATURE [App::DocumentObjectGroupPython] O_element027  label="O_element : 0.387"  # scripted group (container) (typed FeaturePython)
  n = 0.387472
FEATURE [App::DocumentObjectGroupPython] G4_CELLULOSE_BUTYRATE  # scripted group (container) (typed FeaturePython)
  Dunit = g/cm3
  Dvalue = 1.2
  Group = -> [H_element022,C_element026,O_element027]
  conduct = 2
  density = 1
  expand = 3
  formula = G4_CELLULOSE_BUTYRATE
  name = G4_CELLULOSE_BUTYRATE
  specific = 4
FEATURE [App::DocumentObjectGroupPython] H_element023  label="H_element : 0.029"  # scripted group (container) (typed FeaturePython)
  n = 0.029216
FEATURE [App::DocumentObjectGroupPython] C_element027  label="C_element : 0.271"  # scripted group (container) (typed FeaturePython)
  n = 0.271296
FEATURE [App::DocumentObjectGroupPython] N_element013  label="N_element : 0.121"  # scripted group (container) (typed FeaturePython)
  n = 0.121276
FEATURE [App::DocumentObjectGroupPython] O_element028  label="O_element : 0.578"  # scripted group (container) (typed FeaturePython)
  n = 0.578212
FEATURE [App::DocumentObjectGroupPython] G4_CELLULOSE_NITRATE  # scripted group (container) (typed FeaturePython)
  Dunit = g/cm3
  Dvalue = 1.49
  Group = -> [H_element023,C_element027,N_element013,O_element028]
  conduct = 2
  density = 1
  expand = 3
  formula = G4_CELLULOSE_NITRATE
  name = G4_CELLULOSE_NITRATE
  specific = 4
FEATURE [App::DocumentObjectGroupPython] H_element024  label="H_element : 0.108"  # scripted group (container) (typed FeaturePython)
  n = 0.107596
FEATURE [App::DocumentObjectGroupPython] N_element014  label="N_element : 0.001"  # scripted group (container) (typed FeaturePython)
  n = 0.0008
FEATURE [App::DocumentObjectGroupPython] O_element029  label="O_element : 0.875"  # scripted group (container) (typed FeaturePython)
  n = 0.874976
FEATURE [App::DocumentObjectGroupPython] S_element008  label="S_element : 0.015"  # scripted group (container) (typed FeaturePython)
  n = 0.014627
FEATURE [App::DocumentObjectGroupPython] Ce_element001  label="Ce_element : 0.002"  # scripted group (container) (typed FeaturePython)
  n = 0.002001
FEATURE [App::DocumentObjectGroupPython] G4_CERIC_SULFATE  # scripted group (container) (typed FeaturePython)
  Dunit = g/cm3
  Dvalue = 1.03
  Group = -> [H_element024,N_element014,O_element029,S_element008,Ce_element001]
  conduct = 2
  density = 1
  expand = 3
  formula = G4_CERIC_SULFATE
  name = G4_CERIC_SULFATE
  specific = 4
FEATURE [App::DocumentObjectGroupPython] Cs_element001  label="Cs_element : 1"  # scripted group (container) (typed FeaturePython)
  n = 1
  ref = Cs_element
FEATURE [App::DocumentObjectGroupPython] F_element006  label="F_element : 1"  # scripted group (container) (typed FeaturePython)
  n = 1
  ref = F_element
FEATURE [App::DocumentObjectGroupPython] G4_CESIUM_FLUORIDE  # scripted group (container) (typed FeaturePython)
  Dunit = g/cm3
  Dvalue = 4.115
  Group = -> [Cs_element001,F_element006]
  conduct = 2
  density = 1
  expand = 3
  formula = G4_CESIUM_FLUORIDE
  name = G4_CESIUM_FLUORIDE
  specific = 4
FEATURE [App::DocumentObjectGroupPython] Cs_element002  label="Cs_element : 002"  # scripted group (container) (typed FeaturePython)
  n = 1
  ref = Cs_element
FEATURE [App::DocumentObjectGroupPython] I_element001  label="I_element : 1"  # scripted group (container) (typed FeaturePython)
  n = 1
  ref = I_element
FEATURE [App::DocumentObjectGroupPython] G4_CESIUM_IODIDE  # scripted group (container) (typed FeaturePython)
  Dunit = g/cm3
  Dvalue = 4.51
  Group = -> [Cs_element002,I_element001]
  conduct = 2
  density = 1
  expand = 3
  formula = G4_CESIUM_IODIDE
  name = G4_CESIUM_IODIDE
  specific = 4
FEATURE [App::DocumentObjectGroupPython] C_element028  label="C_element : 013"  # scripted group (container) (typed FeaturePython)
  n = 6
  ref = C_element
FEATURE [App::DocumentObjectGroupPython] H_element025  label="H_element : 013"  # scripted group (container) (typed FeaturePython)
  n = 5
  ref = H_element
FEATURE [App::DocumentObjectGroupPython] Cl_element005  label="Cl_element : 1"  # scripted group (container) (typed FeaturePython)
  n = 1
  ref = Cl_element
FEATURE [App::DocumentObjectGroupPython] G4_CHLOROBENZENE  # scripted group (container) (typed FeaturePython)
  Dunit = g/cm3
  Dvalue = 1.1058
  Group = -> [C_element028,H_element025,Cl_element005]
  conduct = 2
  density = 1
  expand = 3
  formula = G4_CHLOROBENZENE
  name = G4_CHLOROBENZENE
  specific = 4
FEATURE [App::DocumentObjectGroupPython] C_element029  label="C_element : 014"  # scripted group (container) (typed FeaturePython)
  n = 1
  ref = C_element
FEATURE [App::DocumentObjectGroupPython] H_element026  label="H_element : 1"  # scripted group (container) (typed FeaturePython)
  n = 1
  ref = H_element
FEATURE [App::DocumentObjectGroupPython] Cl_element006  label="Cl_element : 3"  # scripted group (container) (typed FeaturePython)
  n = 3
  ref = Cl_element
FEATURE [App::DocumentObjectGroupPython] G4_CHLOROFORM  # scripted group (container) (typed FeaturePython)
  Dunit = g/cm3
  Dvalue = 1.4832
  Group = -> [C_element029,H_element026,Cl_element006]
  conduct = 2
  density = 1
  expand = 3
  formula = G4_CHLOROFORM
  name = G4_CHLOROFORM
  specific = 4
FEATURE [App::DocumentObjectGroupPython] H_element027  label="H_element : 0.010"  # scripted group (container) (typed FeaturePython)
  n = 0.01
FEATURE [App::DocumentObjectGroupPython] C_element030  label="C_element : 0.001"  # scripted group (container) (typed FeaturePython)
  n = 0.001
FEATURE [App::DocumentObjectGroupPython] O_element030  label="O_element : 0.529"  # scripted group (container) (typed FeaturePython)
  n = 0.529107
FEATURE [App::DocumentObjectGroupPython] Na_element005  label="Na_element : 0.016"  # scripted group (container) (typed FeaturePython)
  n = 0.016
FEATURE [App::DocumentObjectGroupPython] Mg_element003  label="Mg_element : 0.004"  # scripted group (container) (typed FeaturePython)
  n = 0.002
FEATURE [App::DocumentObjectGroupPython] Al_element002  label="Al_element : 0.034"  # scripted group (container) (typed FeaturePython)
  n = 0.033872
FEATURE [App::DocumentObjectGroupPython] Si_element002  label="Si_element : 0.337"  # scripted group (container) (typed FeaturePython)
  n = 0.337021
FEATURE [App::DocumentObjectGroupPython] K_element003  label="K_element : 0.013"  # scripted group (container) (typed FeaturePython)
  n = 0.013
FEATURE [App::DocumentObjectGroupPython] Ca_element010  label="Ca_element : 0.044"  # scripted group (container) (typed FeaturePython)
  n = 0.044
FEATURE [App::DocumentObjectGroupPython] Fe_element002  label="Fe_element : 0.014"  # scripted group (container) (typed FeaturePython)
  n = 0.014
FEATURE [App::DocumentObjectGroupPython] G4_CONCRETE  # scripted group (container) (typed FeaturePython)
  Dunit = g/cm3
  Dvalue = 2.3
  Group = -> [H_element027,C_element030,O_element030,Na_element005,Mg_element003,Al_element002,Si_element002,K_element003,Ca_element010,Fe_element002]
  conduct = 2
  density = 1
  expand = 3
  formula = G4_CONCRETE
  name = G4_CONCRETE
  specific = 4
FEATURE [App::DocumentObjectGroupPython] C_element031  label="C_element : 015"  # scripted group (container) (typed FeaturePython)
  n = 6
  ref = C_element
FEATURE [App::DocumentObjectGroupPython] H_element028  label="H_element : 12"  # scripted group (container) (typed FeaturePython)
  n = 12
  ref = H_element
FEATURE [App::DocumentObjectGroupPython] G4_CYCLOHEXANE  # scripted group (container) (typed FeaturePython)
  Dunit = g/cm3
  Dvalue = 0.779
  Group = -> [C_element031,H_element028]
  conduct = 2
  density = 1
  expand = 3
  formula = G4_CYCLOHEXANE
  name = G4_CYCLOHEXANE
  specific = 4
FEATURE [App::DocumentObjectGroupPython] C_element032  label="C_element : 016"  # scripted group (container) (typed FeaturePython)
  n = 6
  ref = C_element
FEATURE [App::DocumentObjectGroupPython] H_element029  label="H_element : 4"  # scripted group (container) (typed FeaturePython)
  n = 4
  ref = H_element
FEATURE [App::DocumentObjectGroupPython] Cl_element007  label="Cl_element : 2"  # scripted group (container) (typed FeaturePython)
  n = 2
  ref = Cl_element
FEATURE [App::DocumentObjectGroupPython] G4_1_2_DICHLOROBENZENE  label="G4_1.2-DICHLOROBENZENE"  # scripted group (container) (typed FeaturePython)
  Dunit = g/cm3
  Dvalue = 1.3048
  Group = -> [C_element032,H_element029,Cl_element007]
  conduct = 2
  density = 1
  expand = 3
  formula = G4_1.2-DICHLOROBENZENE
  name = G4_1.2-DICHLOROBENZENE
  specific = 4
FEATURE [App::DocumentObjectGroupPython] C_element033  label="C_element : 017"  # scripted group (container) (typed FeaturePython)
  n = 4
  ref = C_element
FEATURE [App::DocumentObjectGroupPython] H_element030  label="H_element : 8"  # scripted group (container) (typed FeaturePython)
  n = 8
  ref = H_element
FEATURE [App::DocumentObjectGroupPython] O_element031  label="O_element : 014"  # scripted group (container) (typed FeaturePython)
  n = 1
  ref = O_element
FEATURE [App::DocumentObjectGroupPython] Cl_element008  label="Cl_element : 005"  # scripted group (container) (typed FeaturePython)
  n = 2
  ref = Cl_element
FEATURE [App::DocumentObjectGroupPython] G4_DICHLORODIETHYL_ETHER  # scripted group (container) (typed FeaturePython)
  Dunit = g/cm3
  Dvalue = 1.2199
  Group = -> [C_element033,H_element030,O_element031,Cl_element008]
  conduct = 2
  density = 1
  expand = 3
  formula = G4_DICHLORODIETHYL_ETHER
  name = G4_DICHLORODIETHYL_ETHER
  specific = 4
FEATURE [App::DocumentObjectGroupPython] C_element034  label="C_element : 018"  # scripted group (container) (typed FeaturePython)
  n = 2
  ref = C_element
FEATURE [App::DocumentObjectGroupPython] H_element031  label="H_element : 014"  # scripted group (container) (typed FeaturePython)
  n = 4
  ref = H_element
FEATURE [App::DocumentObjectGroupPython] Cl_element009  label="Cl_element : 006"  # scripted group (container) (typed FeaturePython)
  n = 2
  ref = Cl_element
FEATURE [App::DocumentObjectGroupPython] G4_1_2_DICHLOROETHANE  label="G4_1.2-DICHLOROETHANE"  # scripted group (container) (typed FeaturePython)
  Dunit = g/cm3
  Dvalue = 1.2351
  Group = -> [C_element034,H_element031,Cl_element009]
  conduct = 2
  density = 1
  expand = 3
  formula = G4_1.2-DICHLOROETHANE
  name = G4_1.2-DICHLOROETHANE
  specific = 4
FEATURE [App::DocumentObjectGroupPython] C_element035  label="C_element : 019"  # scripted group (container) (typed FeaturePython)
  n = 4
  ref = C_element
FEATURE [App::DocumentObjectGroupPython] H_element032  label="H_element : 015"  # scripted group (container) (typed FeaturePython)
  n = 10
  ref = H_element
FEATURE [App::DocumentObjectGroupPython] O_element032  label="O_element : 015"  # scripted group (container) (typed FeaturePython)
  n = 1
  ref = O_element
FEATURE [App::DocumentObjectGroupPython] G4_DIETHYL_ETHER  # scripted group (container) (typed FeaturePython)
  Dunit = g/cm3
  Dvalue = 0.71378
  Group = -> [C_element035,H_element032,O_element032]
  conduct = 2
  density = 1
  expand = 3
  formula = G4_DIETHYL_ETHER
  name = G4_DIETHYL_ETHER
  specific = 4
FEATURE [App::DocumentObjectGroupPython] C_element036  label="C_element : 020"  # scripted group (container) (typed FeaturePython)
  n = 3
  ref = C_element
FEATURE [App::DocumentObjectGroupPython] H_element033  label="H_element : 016"  # scripted group (container) (typed FeaturePython)
  n = 7
  ref = H_element
FEATURE [App::DocumentObjectGroupPython] N_element015  label="N_element : 008"  # scripted group (container) (typed FeaturePython)
  n = 1
  ref = N_element
FEATURE [App::DocumentObjectGroupPython] O_element033  label="O_element : 016"  # scripted group (container) (typed FeaturePython)
  n = 1
  ref = O_element
FEATURE [App::DocumentObjectGroupPython] G4_N_N_DIMETHYL_FORMAMIDE  label="G4_N.N-DIMETHYL_FORMAMIDE"  # scripted group (container) (typed FeaturePython)
  Dunit = g/cm3
  Dvalue = 0.9487
  Group = -> [C_element036,H_element033,N_element015,O_element033]
  conduct = 2
  density = 1
  expand = 3
  formula = G4_N.N-DIMETHYL_FORMAMIDE
  name = G4_N.N-DIMETHYL_FORMAMIDE
  specific = 4
FEATURE [App::DocumentObjectGroupPython] C_element037  label="C_element : 021"  # scripted group (container) (typed FeaturePython)
  n = 2
  ref = C_element
FEATURE [App::DocumentObjectGroupPython] H_element034  label="H_element : 017"  # scripted group (container) (typed FeaturePython)
  n = 6
  ref = H_element
FEATURE [App::DocumentObjectGroupPython] O_element034  label="O_element : 017"  # scripted group (container) (typed FeaturePython)
  n = 1
  ref = O_element
FEATURE [App::DocumentObjectGroupPython] S_element009  label="S_element : 003"  # scripted group (container) (typed FeaturePython)
  n = 1
  ref = S_element
FEATURE [App::DocumentObjectGroupPython] G4_DIMETHYL_SULFOXIDE  # scripted group (container) (typed FeaturePython)
  Dunit = g/cm3
  Dvalue = 1.1014
  Group = -> [C_element037,H_element034,O_element034,S_element009]
  conduct = 2
  density = 1
  expand = 3
  formula = G4_DIMETHYL_SULFOXIDE
  name = G4_DIMETHYL_SULFOXIDE
  specific = 4
FEATURE [App::DocumentObjectGroupPython] C_element038  label="C_element : 022"  # scripted group (container) (typed FeaturePython)
  n = 2
  ref = C_element
FEATURE [App::DocumentObjectGroupPython] H_element035  label="H_element : 018"  # scripted group (container) (typed FeaturePython)
  n = 6
  ref = H_element
FEATURE [App::DocumentObjectGroupPython] G4_ETHANE  # scripted group (container) (typed FeaturePython)
  Dunit = g/cm3
  Dvalue = 0.00125324
  Group = -> [C_element038,H_element035]
  conduct = 2
  density = 1
  expand = 3
  formula = G4_ETHANE
  name = G4_ETHANE
  specific = 4
FEATURE [App::DocumentObjectGroupPython] C_element039  label="C_element : 023"  # scripted group (container) (typed FeaturePython)
  n = 2
  ref = C_element
FEATURE [App::DocumentObjectGroupPython] H_element036  label="H_element : 019"  # scripted group (container) (typed FeaturePython)
  n = 6
  ref = H_element
FEATURE [App::DocumentObjectGroupPython] O_element035  label="O_element : 018"  # scripted group (container) (typed FeaturePython)
  n = 1
  ref = O_element
FEATURE [App::DocumentObjectGroupPython] G4_ETHYL_ALCOHOL  # scripted group (container) (typed FeaturePython)
  Dunit = g/cm3
  Dvalue = 0.7893
  Group = -> [C_element039,H_element036,O_element035]
  conduct = 2
  density = 1
  expand = 3
  formula = G4_ETHYL_ALCOHOL
  name = G4_ETHYL_ALCOHOL
  specific = 4
FEATURE [App::DocumentObjectGroupPython] H_element037  label="H_element : 0.090"  # scripted group (container) (typed FeaturePython)
  n = 0.090027
FEATURE [App::DocumentObjectGroupPython] C_element040  label="C_element : 0.585"  # scripted group (container) (typed FeaturePython)
  n = 0.585182
FEATURE [App::DocumentObjectGroupPython] O_element036  label="O_element : 0.325"  # scripted group (container) (typed FeaturePython)
  n = 0.324791
FEATURE [App::DocumentObjectGroupPython] G4_ETHYL_CELLULOSE  # scripted group (container) (typed FeaturePython)
  Dunit = g/cm3
  Dvalue = 1.13
  Group = -> [H_element037,C_element040,O_element036]
  conduct = 2
  density = 1
  expand = 3
  formula = G4_ETHYL_CELLULOSE
  name = G4_ETHYL_CELLULOSE
  specific = 4
FEATURE [App::DocumentObjectGroupPython] C_element041  label="C_element : 024"  # scripted group (container) (typed FeaturePython)
  n = 2
  ref = C_element
FEATURE [App::DocumentObjectGroupPython] H_element038  label="H_element : 020"  # scripted group (container) (typed FeaturePython)
  n = 4
  ref = H_element
FEATURE [App::DocumentObjectGroupPython] G4_ETHYLENE  # scripted group (container) (typed FeaturePython)
  Dunit = g/cm3
  Dvalue = 0.00117497
  Group = -> [C_element041,H_element038]
  conduct = 2
  density = 1
  expand = 3
  formula = G4_ETHYLENE
  name = G4_ETHYLENE
  specific = 4
FEATURE [App::DocumentObjectGroupPython] H_element039  label="H_element : 0.096"  # scripted group (container) (typed FeaturePython)
  n = 0.096
FEATURE [App::DocumentObjectGroupPython] C_element042  label="C_element : 0.195"  # scripted group (container) (typed FeaturePython)
  n = 0.195
FEATURE [App::DocumentObjectGroupPython] N_element016  label="N_element : 0.057"  # scripted group (container) (typed FeaturePython)
  n = 0.057
FEATURE [App::DocumentObjectGroupPython] O_element037  label="O_element : 0.646"  # scripted group (container) (typed FeaturePython)
  n = 0.646
FEATURE [App::DocumentObjectGroupPython] Na_element006  label="Na_element : 0.017"  # scripted group (container) (typed FeaturePython)
  n = 0.001
FEATURE [App::DocumentObjectGroupPython] P_element005  label="P_element : 0.104"  # scripted group (container) (typed FeaturePython)
  n = 0.001
FEATURE [App::DocumentObjectGroupPython] S_element010  label="S_element : 0.016"  # scripted group (container) (typed FeaturePython)
  n = 0.003
FEATURE [App::DocumentObjectGroupPython] Cl_element010  label="Cl_element : 0.005"  # scripted group (container) (typed FeaturePython)
  n = 0.001
FEATURE [App::DocumentObjectGroupPython] G4_EYE_LENS_ICRP  # scripted group (container) (typed FeaturePython)
  Dunit = g/cm3
  Dvalue = 1.07
  Group = -> [H_element039,C_element042,N_element016,O_element037,Na_element006,P_element005,S_element010,Cl_element010]
  conduct = 2
  density = 1
  expand = 3
  formula = G4_EYE_LENS_ICRP
  name = G4_EYE_LENS_ICRP
  specific = 4
FEATURE [App::DocumentObjectGroupPython] Fe_element003  label="Fe_element : 2"  # scripted group (container) (typed FeaturePython)
  n = 2
  ref = Fe_element
FEATURE [App::DocumentObjectGroupPython] O_element038  label="O_element : 019"  # scripted group (container) (typed FeaturePython)
  n = 3
  ref = O_element
FEATURE [App::DocumentObjectGroupPython] G4_FERRIC_OXIDE  # scripted group (container) (typed FeaturePython)
  Dunit = g/cm3
  Dvalue = 5.2
  Group = -> [Fe_element003,O_element038]
  conduct = 2
  density = 1
  expand = 3
  formula = G4_FERRIC_OXIDE
  name = G4_FERRIC_OXIDE
  specific = 4
FEATURE [App::DocumentObjectGroupPython] Fe_element004  label="Fe_element : 1"  # scripted group (container) (typed FeaturePython)
  n = 1
  ref = Fe_element
FEATURE [App::DocumentObjectGroupPython] B_element003  label="B_element : 1"  # scripted group (container) (typed FeaturePython)
  n = 1
  ref = B_element
FEATURE [App::DocumentObjectGroupPython] G4_FERROBORIDE  # scripted group (container) (typed FeaturePython)
  Dunit = g/cm3
  Dvalue = 7.15
  Group = -> [Fe_element004,B_element003]
  conduct = 2
  density = 1
  expand = 3
  formula = G4_FERROBORIDE
  name = G4_FERROBORIDE
  specific = 4
FEATURE [App::DocumentObjectGroupPython] Fe_element005  label="Fe_element : 003"  # scripted group (container) (typed FeaturePython)
  n = 1
  ref = Fe_element
FEATURE [App::DocumentObjectGroupPython] O_element039  label="O_element : 020"  # scripted group (container) (typed FeaturePython)
  n = 1
  ref = O_element
FEATURE [App::DocumentObjectGroupPython] G4_FERROUS_OXIDE  # scripted group (container) (typed FeaturePython)
  Dunit = g/cm3
  Dvalue = 5.7
  Group = -> [Fe_element005,O_element039]
  conduct = 2
  density = 1
  expand = 3
  formula = G4_FERROUS_OXIDE
  name = G4_FERROUS_OXIDE
  specific = 4
FEATURE [App::DocumentObjectGroupPython] H_element040  label="H_element : 0.115"  # scripted group (container) (typed FeaturePython)
  n = 0.108259
FEATURE [App::DocumentObjectGroupPython] N_element017  label="N_element : 0.000"  # scripted group (container) (typed FeaturePython)
  n = 2.7e-05
FEATURE [App::DocumentObjectGroupPython] O_element040  label="O_element : 0.879"  # scripted group (container) (typed FeaturePython)
  n = 0.878636
FEATURE [App::DocumentObjectGroupPython] Na_element007  label="Na_element : 0.000"  # scripted group (container) (typed FeaturePython)
  n = 2.2e-05
FEATURE [App::DocumentObjectGroupPython] S_element011  label="S_element : 0.013"  # scripted group (container) (typed FeaturePython)
  n = 0.012968
FEATURE [App::DocumentObjectGroupPython] Cl_element011  label="Cl_element : 0.000"  # scripted group (container) (typed FeaturePython)
  n = 3.4e-05
FEATURE [App::DocumentObjectGroupPython] Fe_element006  label="Fe_element : 0.000"  # scripted group (container) (typed FeaturePython)
  n = 5.4e-05
FEATURE [App::DocumentObjectGroupPython] G4_FERROUS_SULFATE  # scripted group (container) (typed FeaturePython)
  Dunit = g/cm3
  Dvalue = 1.024
  Group = -> [H_element040,N_element017,O_element040,Na_element007,S_element011,Cl_element011,Fe_element006]
  conduct = 2
  density = 1
  expand = 3
  formula = G4_FERROUS_SULFATE
  name = G4_FERROUS_SULFATE
  specific = 4
FEATURE [App::DocumentObjectGroupPython] C_element043  label="C_element : 0.099"  # scripted group (container) (typed FeaturePython)
  n = 0.099335
FEATURE [App::DocumentObjectGroupPython] F_element007  label="F_element : 0.314"  # scripted group (container) (typed FeaturePython)
  n = 0.314247
FEATURE [App::DocumentObjectGroupPython] Cl_element012  label="Cl_element : 0.586"  # scripted group (container) (typed FeaturePython)
  n = 0.586418
FEATURE [App::DocumentObjectGroupPython] G4_FREON_12  label="G4_FREON-12"  # scripted group (container) (typed FeaturePython)
  Dunit = g/cm3
  Dvalue = 1.12
  Group = -> [C_element043,F_element007,Cl_element012]
  conduct = 2
  density = 1
  expand = 3
  formula = G4_FREON-12
  name = G4_FREON-12
  specific = 4
FEATURE [App::DocumentObjectGroupPython] C_element044  label="C_element : 0.057"  # scripted group (container) (typed FeaturePython)
  n = 0.057245
FEATURE [App::DocumentObjectGroupPython] F_element008  label="F_element : 0.181"  # scripted group (container) (typed FeaturePython)
  n = 0.181096
FEATURE [App::DocumentObjectGroupPython] Br_element001  label="Br_element : 0.762"  # scripted group (container) (typed FeaturePython)
  n = 0.761659
FEATURE [App::DocumentObjectGroupPython] G4_FREON_12B2  label="G4_FREON-12B2"  # scripted group (container) (typed FeaturePython)
  Dunit = g/cm3
  Dvalue = 1.8
  Group = -> [C_element044,F_element008,Br_element001]
  conduct = 2
  density = 1
  expand = 3
  formula = G4_FREON-12B2
  name = G4_FREON-12B2
  specific = 4
FEATURE [App::DocumentObjectGroupPython] C_element045  label="C_element : 0.115"  # scripted group (container) (typed FeaturePython)
  n = 0.114983
FEATURE [App::DocumentObjectGroupPython] F_element009  label="F_element : 0.546"  # scripted group (container) (typed FeaturePython)
  n = 0.545621
FEATURE [App::DocumentObjectGroupPython] Cl_element013  label="Cl_element : 0.339"  # scripted group (container) (typed FeaturePython)
  n = 0.339396
FEATURE [App::DocumentObjectGroupPython] G4_FREON_13  label="G4_FREON-13"  # scripted group (container) (typed FeaturePython)
  Dunit = g/cm3
  Dvalue = 0.95
  Group = -> [C_element045,F_element009,Cl_element013]
  conduct = 2
  density = 1
  expand = 3
  formula = G4_FREON-13
  name = G4_FREON-13
  specific = 4
FEATURE [App::DocumentObjectGroupPython] C_element046  label="C_element : 025"  # scripted group (container) (typed FeaturePython)
  n = 1
  ref = C_element
FEATURE [App::DocumentObjectGroupPython] F_element010  label="F_element : 3"  # scripted group (container) (typed FeaturePython)
  n = 3
  ref = F_element
FEATURE [App::DocumentObjectGroupPython] Br_element002  label="Br_element : 1"  # scripted group (container) (typed FeaturePython)
  n = 1
  ref = Br_element
FEATURE [App::DocumentObjectGroupPython] G4_FREON_13B1  label="G4_FREON-13B1"  # scripted group (container) (typed FeaturePython)
  Dunit = g/cm3
  Dvalue = 1.5
  Group = -> [C_element046,F_element010,Br_element002]
  conduct = 2
  density = 1
  expand = 3
  formula = G4_FREON-13B1
  name = G4_FREON-13B1
  specific = 4
FEATURE [App::DocumentObjectGroupPython] C_element047  label="C_element : 0.061"  # scripted group (container) (typed FeaturePython)
  n = 0.061309
FEATURE [App::DocumentObjectGroupPython] F_element011  label="F_element : 0.291"  # scripted group (container) (typed FeaturePython)
  n = 0.290924
FEATURE [App::DocumentObjectGroupPython] I_element002  label="I_element : 0.648"  # scripted group (container) (typed FeaturePython)
  n = 0.647767
FEATURE [App::DocumentObjectGroupPython] G4_FREON_13I1  label="G4_FREON-13I1"  # scripted group (container) (typed FeaturePython)
  Dunit = g/cm3
  Dvalue = 1.8
  Group = -> [C_element047,F_element011,I_element002]
  conduct = 2
  density = 1
  expand = 3
  formula = G4_FREON-13I1
  name = G4_FREON-13I1
  specific = 4
FEATURE [App::DocumentObjectGroupPython] Gd_element001  label="Gd_element : 2"  # scripted group (container) (typed FeaturePython)
  n = 2
  ref = Gd_element
FEATURE [App::DocumentObjectGroupPython] O_element041  label="O_element : 021"  # scripted group (container) (typed FeaturePython)
  n = 2
  ref = O_element
FEATURE [App::DocumentObjectGroupPython] S_element012  label="S_element : 004"  # scripted group (container) (typed FeaturePython)
  n = 1
  ref = S_element
FEATURE [App::DocumentObjectGroupPython] G4_GADOLINIUM_OXYSULFIDE  # scripted group (container) (typed FeaturePython)
  Dunit = g/cm3
  Dvalue = 7.44
  Group = -> [Gd_element001,O_element041,S_element012]
  conduct = 2
  density = 1
  expand = 3
  formula = G4_GADOLINIUM_OXYSULFIDE
  name = G4_GADOLINIUM_OXYSULFIDE
  specific = 4
FEATURE [App::DocumentObjectGroupPython] Ga_element001  label="Ga_element : 1"  # scripted group (container) (typed FeaturePython)
  n = 1
  ref = Ga_element
FEATURE [App::DocumentObjectGroupPython] As_element001  label="As_element : 1"  # scripted group (container) (typed FeaturePython)
  n = 1
  ref = As_element
FEATURE [App::DocumentObjectGroupPython] G4_GALLIUM_ARSENIDE  # scripted group (container) (typed FeaturePython)
  Dunit = g/cm3
  Dvalue = 5.31
  Group = -> [Ga_element001,As_element001]
  conduct = 2
  density = 1
  expand = 3
  formula = G4_GALLIUM_ARSENIDE
  name = G4_GALLIUM_ARSENIDE
  specific = 4
FEATURE [App::DocumentObjectGroupPython] H_element041  label="H_element : 0.081"  # scripted group (container) (typed FeaturePython)
  n = 0.08118
FEATURE [App::DocumentObjectGroupPython] C_element048  label="C_element : 0.416"  # scripted group (container) (typed FeaturePython)
  n = 0.41606
FEATURE [App::DocumentObjectGroupPython] N_element018  label="N_element : 0.111"  # scripted group (container) (typed FeaturePython)
  n = 0.11124
FEATURE [App::DocumentObjectGroupPython] O_element042  label="O_element : 0.381"  # scripted group (container) (typed FeaturePython)
  n = 0.38064
FEATURE [App::DocumentObjectGroupPython] S_element013  label="S_element : 0.011"  # scripted group (container) (typed FeaturePython)
  n = 0.01088
FEATURE [App::DocumentObjectGroupPython] G4_GEL_PHOTO_EMULSION  # scripted group (container) (typed FeaturePython)
  Dunit = g/cm3
  Dvalue = 1.2914
  Group = -> [H_element041,C_element048,N_element018,O_element042,S_element013]
  conduct = 2
  density = 1
  expand = 3
  formula = G4_GEL_PHOTO_EMULSION
  name = G4_GEL_PHOTO_EMULSION
  specific = 4
FEATURE [App::DocumentObjectGroupPython] B_element004  label="B_element : 0.040"  # scripted group (container) (typed FeaturePython)
  n = 0.0400639
FEATURE [App::DocumentObjectGroupPython] O_element043  label="O_element : 0.540"  # scripted group (container) (typed FeaturePython)
  n = 0.539561
FEATURE [App::DocumentObjectGroupPython] Na_element008  label="Na_element : 0.028"  # scripted group (container) (typed FeaturePython)
  n = 0.0281909
FEATURE [App::DocumentObjectGroupPython] Al_element003  label="Al_element : 0.012"  # scripted group (container) (typed FeaturePython)
  n = 0.011644
FEATURE [App::DocumentObjectGroupPython] Si_element003  label="Si_element : 0.377"  # scripted group (container) (typed FeaturePython)
  n = 0.377219
FEATURE [App::DocumentObjectGroupPython] K_element004  label="K_element : 0.014"  # scripted group (container) (typed FeaturePython)
  n = 0.00332099
FEATURE [App::DocumentObjectGroupPython] G4_Pyrex_Glass  # scripted group (container) (typed FeaturePython)
  Dunit = g/cm3
  Dvalue = 2.23
  Group = -> [B_element004,O_element043,Na_element008,Al_element003,Si_element003,K_element004]
  conduct = 2
  density = 1
  expand = 3
  formula = G4_Pyrex_Glass
  name = G4_Pyrex_Glass
  specific = 4
FEATURE [App::DocumentObjectGroupPython] O_element044  label="O_element : 0.156"  # scripted group (container) (typed FeaturePython)
  n = 0.156453
FEATURE [App::DocumentObjectGroupPython] Si_element004  label="Si_element : 0.081"  # scripted group (container) (typed FeaturePython)
  n = 0.080866
FEATURE [App::DocumentObjectGroupPython] Ti_element001  label="Ti_element : 0.008"  # scripted group (container) (typed FeaturePython)
  n = 0.008092
FEATURE [App::DocumentObjectGroupPython] As_element002  label="As_element : 0.003"  # scripted group (container) (typed FeaturePython)
  n = 0.002651
FEATURE [App::DocumentObjectGroupPython] Pb_element001  label="Pb_element : 0.752"  # scripted group (container) (typed FeaturePython)
  n = 0.751938
FEATURE [App::DocumentObjectGroupPython] G4_GLASS_LEAD  # scripted group (container) (typed FeaturePython)
  Dunit = g/cm3
  Dvalue = 6.22
  Group = -> [O_element044,Si_element004,Ti_element001,As_element002,Pb_element001]
  conduct = 2
  density = 1
  expand = 3
  formula = G4_GLASS_LEAD
  name = G4_GLASS_LEAD
  specific = 4
FEATURE [App::DocumentObjectGroupPython] O_element045  label="O_element : 0.460"  # scripted group (container) (typed FeaturePython)
  n = 0.4598
FEATURE [App::DocumentObjectGroupPython] Na_element009  label="Na_element : 0.096"  # scripted group (container) (typed FeaturePython)
  n = 0.0964411
FEATURE [App::DocumentObjectGroupPython] Si_element005  label="Si_element : 0.378"  # scripted group (container) (typed FeaturePython)
  n = 0.336553
FEATURE [App::DocumentObjectGroupPython] Ca_element011  label="Ca_element : 0.107"  # scripted group (container) (typed FeaturePython)
  n = 0.107205
FEATURE [App::DocumentObjectGroupPython] G4_GLASS_PLATE  # scripted group (container) (typed FeaturePython)
  Dunit = g/cm3
  Dvalue = 2.4
  Group = -> [O_element045,Na_element009,Si_element005,Ca_element011]
  conduct = 2
  density = 1
  expand = 3
  formula = G4_GLASS_PLATE
  name = G4_GLASS_PLATE
  specific = 4
FEATURE [App::DocumentObjectGroupPython] C_element049  label="C_element : 026"  # scripted group (container) (typed FeaturePython)
  n = 5
  ref = C_element
FEATURE [App::DocumentObjectGroupPython] H_element042  label="H_element : 021"  # scripted group (container) (typed FeaturePython)
  n = 10
  ref = H_element
FEATURE [App::DocumentObjectGroupPython] N_element019  label="N_element : 2"  # scripted group (container) (typed FeaturePython)
  n = 2
  ref = N_element
FEATURE [App::DocumentObjectGroupPython] O_element046  label="O_element : 022"  # scripted group (container) (typed FeaturePython)
  n = 3
  ref = O_element
FEATURE [App::DocumentObjectGroupPython] G4_GLUTAMINE  # scripted group (container) (typed FeaturePython)
  Dunit = g/cm3
  Dvalue = 1.46
  Group = -> [C_element049,H_element042,N_element019,O_element046]
  conduct = 2
  density = 1
  expand = 3
  formula = G4_GLUTAMINE
  name = G4_GLUTAMINE
  specific = 4
FEATURE [App::DocumentObjectGroupPython] C_element050  label="C_element : 027"  # scripted group (container) (typed FeaturePython)
  n = 3
  ref = C_element
FEATURE [App::DocumentObjectGroupPython] H_element043  label="H_element : 022"  # scripted group (container) (typed FeaturePython)
  n = 8
  ref = H_element
FEATURE [App::DocumentObjectGroupPython] O_element047  label="O_element : 023"  # scripted group (container) (typed FeaturePython)
  n = 3
  ref = O_element
FEATURE [App::DocumentObjectGroupPython] G4_GLYCEROL  # scripted group (container) (typed FeaturePython)
  Dunit = g/cm3
  Dvalue = 1.2613
  Group = -> [C_element050,H_element043,O_element047]
  conduct = 2
  density = 1
  expand = 3
  formula = G4_GLYCEROL
  name = G4_GLYCEROL
  specific = 4
FEATURE [App::DocumentObjectGroupPython] C_element051  label="C_element : 028"  # scripted group (container) (typed FeaturePython)
  n = 5
  ref = C_element
FEATURE [App::DocumentObjectGroupPython] H_element044  label="H_element : 023"  # scripted group (container) (typed FeaturePython)
  n = 5
  ref = H_element
FEATURE [App::DocumentObjectGroupPython] N_element020  label="N_element : 009"  # scripted group (container) (typed FeaturePython)
  n = 5
  ref = N_element
FEATURE [App::DocumentObjectGroupPython] O_element048  label="O_element : 024"  # scripted group (container) (typed FeaturePython)
  n = 1
  ref = O_element
FEATURE [App::DocumentObjectGroupPython] G4_GUANINE  # scripted group (container) (typed FeaturePython)
  Dunit = g/cm3
  Dvalue = 2.2
  Group = -> [C_element051,H_element044,N_element020,O_element048]
  conduct = 2
  density = 1
  expand = 3
  formula = G4_GUANINE
  name = G4_GUANINE
  specific = 4
FEATURE [App::DocumentObjectGroupPython] Ca_element012  label="Ca_element : 006"  # scripted group (container) (typed FeaturePython)
  n = 1
  ref = Ca_element
FEATURE [App::DocumentObjectGroupPython] S_element014  label="S_element : 005"  # scripted group (container) (typed FeaturePython)
  n = 1
  ref = S_element
FEATURE [App::DocumentObjectGroupPython] O_element049  label="O_element : 6"  # scripted group (container) (typed FeaturePython)
  n = 6
  ref = O_element
FEATURE [App::DocumentObjectGroupPython] H_element045  label="H_element : 024"  # scripted group (container) (typed FeaturePython)
  n = 4
  ref = H_element
FEATURE [App::DocumentObjectGroupPython] G4_GYPSUM  # scripted group (container) (typed FeaturePython)
  Dunit = g/cm3
  Dvalue = 2.32
  Group = -> [Ca_element012,S_element014,O_element049,H_element045]
  conduct = 2
  density = 1
  expand = 3
  formula = G4_GYPSUM
  name = G4_GYPSUM
  specific = 4
FEATURE [App::DocumentObjectGroupPython] C_element052  label="C_element : 7"  # scripted group (container) (typed FeaturePython)
  n = 7
  ref = C_element
FEATURE [App::DocumentObjectGroupPython] H_element046  label="H_element : 16"  # scripted group (container) (typed FeaturePython)
  n = 16
  ref = H_element
FEATURE [App::DocumentObjectGroupPython] G4_N_HEPTANE  label="G4_N-HEPTANE"  # scripted group (container) (typed FeaturePython)
  Dunit = g/cm3
  Dvalue = 0.68376
  Group = -> [C_element052,H_element046]
  conduct = 2
  density = 1
  expand = 3
  formula = G4_N-HEPTANE
  name = G4_N-HEPTANE
  specific = 4
FEATURE [App::DocumentObjectGroupPython] C_element053  label="C_element : 029"  # scripted group (container) (typed FeaturePython)
  n = 6
  ref = C_element
FEATURE [App::DocumentObjectGroupPython] H_element047  label="H_element : 14"  # scripted group (container) (typed FeaturePython)
  n = 14
  ref = H_element
FEATURE [App::DocumentObjectGroupPython] G4_N_HEXANE  label="G4_N-HEXANE"  # scripted group (container) (typed FeaturePython)
  Dunit = g/cm3
  Dvalue = 0.6603
  Group = -> [C_element053,H_element047]
  conduct = 2
  density = 1
  expand = 3
  formula = G4_N-HEXANE
  name = G4_N-HEXANE
  specific = 4
FEATURE [App::DocumentObjectGroupPython] C_element054  label="C_element : 22"  # scripted group (container) (typed FeaturePython)
  n = 22
  ref = C_element
FEATURE [App::DocumentObjectGroupPython] H_element048  label="H_element : 025"  # scripted group (container) (typed FeaturePython)
  n = 10
  ref = H_element
FEATURE [App::DocumentObjectGroupPython] N_element021  label="N_element : 010"  # scripted group (container) (typed FeaturePython)
  n = 2
  ref = N_element
FEATURE [App::DocumentObjectGroupPython] O_element050  label="O_element : 025"  # scripted group (container) (typed FeaturePython)
  n = 5
  ref = O_element
FEATURE [App::DocumentObjectGroupPython] G4_KAPTON  # scripted group (container) (typed FeaturePython)
  Dunit = g/cm3
  Dvalue = 1.42
  Group = -> [C_element054,H_element048,N_element021,O_element050]
  conduct = 2
  density = 1
  expand = 3
  formula = G4_KAPTON
  name = G4_KAPTON
  specific = 4
FEATURE [App::DocumentObjectGroupPython] La_element001  label="La_element : 1"  # scripted group (container) (typed FeaturePython)
  n = 1
  ref = La_element
FEATURE [App::DocumentObjectGroupPython] Br_element003  label="Br_element : 002"  # scripted group (container) (typed FeaturePython)
  n = 1
  ref = Br_element
FEATURE [App::DocumentObjectGroupPython] O_element051  label="O_element : 026"  # scripted group (container) (typed FeaturePython)
  n = 1
  ref = O_element
FEATURE [App::DocumentObjectGroupPython] G4_LANTHANUM_OXYBROMIDE  # scripted group (container) (typed FeaturePython)
  Dunit = g/cm3
  Dvalue = 6.28
  Group = -> [La_element001,Br_element003,O_element051]
  conduct = 2
  density = 1
  expand = 3
  formula = G4_LANTHANUM_OXYBROMIDE
  name = G4_LANTHANUM_OXYBROMIDE
  specific = 4
FEATURE [App::DocumentObjectGroupPython] La_element002  label="La_element : 2"  # scripted group (container) (typed FeaturePython)
  n = 2
  ref = La_element
FEATURE [App::DocumentObjectGroupPython] O_element052  label="O_element : 027"  # scripted group (container) (typed FeaturePython)
  n = 2
  ref = O_element
FEATURE [App::DocumentObjectGroupPython] S_element015  label="S_element : 006"  # scripted group (container) (typed FeaturePython)
  n = 1
  ref = S_element
FEATURE [App::DocumentObjectGroupPython] G4_LANTHANUM_OXYSULFIDE  # scripted group (container) (typed FeaturePython)
  Dunit = g/cm3
  Dvalue = 5.86
  Group = -> [La_element002,O_element052,S_element015]
  conduct = 2
  density = 1
  expand = 3
  formula = G4_LANTHANUM_OXYSULFIDE
  name = G4_LANTHANUM_OXYSULFIDE
  specific = 4
FEATURE [App::DocumentObjectGroupPython] O_element053  label="O_element : 0.072"  # scripted group (container) (typed FeaturePython)
  n = 0.071682
FEATURE [App::DocumentObjectGroupPython] Pb_element002  label="Pb_element : 0.928"  # scripted group (container) (typed FeaturePython)
  n = 0.928318
FEATURE [App::DocumentObjectGroupPython] G4_LEAD_OXIDE  # scripted group (container) (typed FeaturePython)
  Dunit = g/cm3
  Dvalue = 9.53
  Group = -> [O_element053,Pb_element002]
  conduct = 2
  density = 1
  expand = 3
  formula = G4_LEAD_OXIDE
  name = G4_LEAD_OXIDE
  specific = 4
FEATURE [App::DocumentObjectGroupPython] Li_element001  label="Li_element : 1"  # scripted group (container) (typed FeaturePython)
  n = 1
  ref = Li_element
FEATURE [App::DocumentObjectGroupPython] N_element022  label="N_element : 011"  # scripted group (container) (typed FeaturePython)
  n = 1
  ref = N_element
FEATURE [App::DocumentObjectGroupPython] H_element049  label="H_element : 026"  # scripted group (container) (typed FeaturePython)
  n = 2
  ref = H_element
FEATURE [App::DocumentObjectGroupPython] G4_LITHIUM_AMIDE  # scripted group (container) (typed FeaturePython)
  Dunit = g/cm3
  Dvalue = 1.178
  Group = -> [Li_element001,N_element022,H_element049]
  conduct = 2
  density = 1
  expand = 3
  formula = G4_LITHIUM_AMIDE
  name = G4_LITHIUM_AMIDE
  specific = 4
FEATURE [App::DocumentObjectGroupPython] Li_element002  label="Li_element : 2"  # scripted group (container) (typed FeaturePython)
  n = 2
  ref = Li_element
FEATURE [App::DocumentObjectGroupPython] C_element055  label="C_element : 030"  # scripted group (container) (typed FeaturePython)
  n = 1
  ref = C_element
FEATURE [App::DocumentObjectGroupPython] O_element054  label="O_element : 028"  # scripted group (container) (typed FeaturePython)
  n = 3
  ref = O_element
FEATURE [App::DocumentObjectGroupPython] G4_LITHIUM_CARBONATE  # scripted group (container) (typed FeaturePython)
  Dunit = g/cm3
  Dvalue = 2.11
  Group = -> [Li_element002,C_element055,O_element054]
  conduct = 2
  density = 1
  expand = 3
  formula = G4_LITHIUM_CARBONATE
  name = G4_LITHIUM_CARBONATE
  specific = 4
FEATURE [App::DocumentObjectGroupPython] Li_element003  label="Li_element : 003"  # scripted group (container) (typed FeaturePython)
  n = 1
  ref = Li_element
FEATURE [App::DocumentObjectGroupPython] F_element012  label="F_element : 004"  # scripted group (container) (typed FeaturePython)
  n = 1
  ref = F_element
FEATURE [App::DocumentObjectGroupPython] G4_LITHIUM_FLUORIDE  # scripted group (container) (typed FeaturePython)
  Dunit = g/cm3
  Dvalue = 2.635
  Group = -> [Li_element003,F_element012]
  conduct = 2
  density = 1
  expand = 3
  formula = G4_LITHIUM_FLUORIDE
  name = G4_LITHIUM_FLUORIDE
  specific = 4
FEATURE [App::DocumentObjectGroupPython] Li_element004  label="Li_element : 004"  # scripted group (container) (typed FeaturePython)
  n = 1
  ref = Li_element
FEATURE [App::DocumentObjectGroupPython] H_element050  label="H_element : 027"  # scripted group (container) (typed FeaturePython)
  n = 1
  ref = H_element
FEATURE [App::DocumentObjectGroupPython] G4_LITHIUM_HYDRIDE  # scripted group (container) (typed FeaturePython)
  Dunit = g/cm3
  Dvalue = 0.82
  Group = -> [Li_element004,H_element050]
  conduct = 2
  density = 1
  expand = 3
  formula = G4_LITHIUM_HYDRIDE
  name = G4_LITHIUM_HYDRIDE
  specific = 4
FEATURE [App::DocumentObjectGroupPython] Li_element005  label="Li_element : 005"  # scripted group (container) (typed FeaturePython)
  n = 1
  ref = Li_element
FEATURE [App::DocumentObjectGroupPython] I_element003  label="I_element : 002"  # scripted group (container) (typed FeaturePython)
  n = 1
  ref = I_element
FEATURE [App::DocumentObjectGroupPython] G4_LITHIUM_IODIDE  # scripted group (container) (typed FeaturePython)
  Dunit = g/cm3
  Dvalue = 3.494
  Group = -> [Li_element005,I_element003]
  conduct = 2
  density = 1
  expand = 3
  formula = G4_LITHIUM_IODIDE
  name = G4_LITHIUM_IODIDE
  specific = 4
FEATURE [App::DocumentObjectGroupPython] Li_element006  label="Li_element : 006"  # scripted group (container) (typed FeaturePython)
  n = 2
  ref = Li_element
FEATURE [App::DocumentObjectGroupPython] O_element055  label="O_element : 029"  # scripted group (container) (typed FeaturePython)
  n = 1
  ref = O_element
FEATURE [App::DocumentObjectGroupPython] G4_LITHIUM_OXIDE  # scripted group (container) (typed FeaturePython)
  Dunit = g/cm3
  Dvalue = 2.013
  Group = -> [Li_element006,O_element055]
  conduct = 2
  density = 1
  expand = 3
  formula = G4_LITHIUM_OXIDE
  name = G4_LITHIUM_OXIDE
  specific = 4
FEATURE [App::DocumentObjectGroupPython] Li_element007  label="Li_element : 007"  # scripted group (container) (typed FeaturePython)
  n = 2
  ref = Li_element
FEATURE [App::DocumentObjectGroupPython] B_element005  label="B_element : 005"  # scripted group (container) (typed FeaturePython)
  n = 4
  ref = B_element
FEATURE [App::DocumentObjectGroupPython] O_element056  label="O_element : 7"  # scripted group (container) (typed FeaturePython)
  n = 7
  ref = O_element
FEATURE [App::DocumentObjectGroupPython] G4_LITHIUM_TETRABORATE  # scripted group (container) (typed FeaturePython)
  Dunit = g/cm3
  Dvalue = 2.44
  Group = -> [Li_element007,B_element005,O_element056]
  conduct = 2
  density = 1
  expand = 3
  formula = G4_LITHIUM_TETRABORATE
  name = G4_LITHIUM_TETRABORATE
  specific = 4
FEATURE [App::DocumentObjectGroupPython] H_element051  label="H_element : 0.105"  # scripted group (container) (typed FeaturePython)
  n = 0.105
FEATURE [App::DocumentObjectGroupPython] C_element056  label="C_element : 0.083"  # scripted group (container) (typed FeaturePython)
  n = 0.083
FEATURE [App::DocumentObjectGroupPython] N_element023  label="N_element : 0.023"  # scripted group (container) (typed FeaturePython)
  n = 0.023
FEATURE [App::DocumentObjectGroupPython] O_element057  label="O_element : 0.779"  # scripted group (container) (typed FeaturePython)
  n = 0.779
FEATURE [App::DocumentObjectGroupPython] Na_element010  label="Na_element : 0.097"  # scripted group (container) (typed FeaturePython)
  n = 0.002
FEATURE [App::DocumentObjectGroupPython] P_element006  label="P_element : 0.105"  # scripted group (container) (typed FeaturePython)
  n = 0.001
FEATURE [App::DocumentObjectGroupPython] S_element016  label="S_element : 0.017"  # scripted group (container) (typed FeaturePython)
  n = 0.002
FEATURE [App::DocumentObjectGroupPython] Cl_element014  label="Cl_element : 0.587"  # scripted group (container) (typed FeaturePython)
  n = 0.003
FEATURE [App::DocumentObjectGroupPython] K_element005  label="K_element : 0.015"  # scripted group (container) (typed FeaturePython)
  n = 0.002
FEATURE [App::DocumentObjectGroupPython] G4_LUNG_ICRP  # scripted group (container) (typed FeaturePython)
  Dunit = g/cm3
  Dvalue = 1.04
  Group = -> [H_element051,C_element056,N_element023,O_element057,Na_element010,P_element006,S_element016,Cl_element014,K_element005]
  conduct = 2
  density = 1
  expand = 3
  formula = G4_LUNG_ICRP
  name = G4_LUNG_ICRP
  specific = 4
FEATURE [App::DocumentObjectGroupPython] H_element052  label="H_element : 0.116"  # scripted group (container) (typed FeaturePython)
  n = 0.114318
FEATURE [App::DocumentObjectGroupPython] C_element057  label="C_element : 0.656"  # scripted group (container) (typed FeaturePython)
  n = 0.655824
FEATURE [App::DocumentObjectGroupPython] O_element058  label="O_element : 0.092"  # scripted group (container) (typed FeaturePython)
  n = 0.0921831
FEATURE [App::DocumentObjectGroupPython] Mg_element004  label="Mg_element : 0.135"  # scripted group (container) (typed FeaturePython)
  n = 0.134792
FEATURE [App::DocumentObjectGroupPython] Ca_element013  label="Ca_element : 0.003"  # scripted group (container) (typed FeaturePython)
  n = 0.002883
FEATURE [App::DocumentObjectGroupPython] G4_M3_WAX  # scripted group (container) (typed FeaturePython)
  Dunit = g/cm3
  Dvalue = 1.05
  Group = -> [H_element052,C_element057,O_element058,Mg_element004,Ca_element013]
  conduct = 2
  density = 1
  expand = 3
  formula = G4_M3_WAX
  name = G4_M3_WAX
  specific = 4
FEATURE [App::DocumentObjectGroupPython] Mg_element005  label="Mg_element : 1"  # scripted group (container) (typed FeaturePython)
  n = 1
  ref = Mg_element
FEATURE [App::DocumentObjectGroupPython] C_element058  label="C_element : 031"  # scripted group (container) (typed FeaturePython)
  n = 1
  ref = C_element
FEATURE [App::DocumentObjectGroupPython] O_element059  label="O_element : 030"  # scripted group (container) (typed FeaturePython)
  n = 3
  ref = O_element
FEATURE [App::DocumentObjectGroupPython] G4_MAGNESIUM_CARBONATE  # scripted group (container) (typed FeaturePython)
  Dunit = g/cm3
  Dvalue = 2.958
  Group = -> [Mg_element005,C_element058,O_element059]
  conduct = 2
  density = 1
  expand = 3
  formula = G4_MAGNESIUM_CARBONATE
  name = G4_MAGNESIUM_CARBONATE
  specific = 4
FEATURE [App::DocumentObjectGroupPython] Mg_element006  label="Mg_element : 002"  # scripted group (container) (typed FeaturePython)
  n = 1
  ref = Mg_element
FEATURE [App::DocumentObjectGroupPython] F_element013  label="F_element : 005"  # scripted group (container) (typed FeaturePython)
  n = 2
  ref = F_element
FEATURE [App::DocumentObjectGroupPython] G4_MAGNESIUM_FLUORIDE  # scripted group (container) (typed FeaturePython)
  Dunit = g/cm3
  Dvalue = 3
  Group = -> [Mg_element006,F_element013]
  conduct = 2
  density = 1
  expand = 3
  formula = G4_MAGNESIUM_FLUORIDE
  name = G4_MAGNESIUM_FLUORIDE
  specific = 4
FEATURE [App::DocumentObjectGroupPython] Mg_element007  label="Mg_element : 003"  # scripted group (container) (typed FeaturePython)
  n = 1
  ref = Mg_element
FEATURE [App::DocumentObjectGroupPython] O_element060  label="O_element : 031"  # scripted group (container) (typed FeaturePython)
  n = 1
  ref = O_element
FEATURE [App::DocumentObjectGroupPython] G4_MAGNESIUM_OXIDE  # scripted group (container) (typed FeaturePython)
  Dunit = g/cm3
  Dvalue = 3.58
  Group = -> [Mg_element007,O_element060]
  conduct = 2
  density = 1
  expand = 3
  formula = G4_MAGNESIUM_OXIDE
  name = G4_MAGNESIUM_OXIDE
  specific = 4
FEATURE [App::DocumentObjectGroupPython] Mg_element008  label="Mg_element : 004"  # scripted group (container) (typed FeaturePython)
  n = 1
  ref = Mg_element
FEATURE [App::DocumentObjectGroupPython] B_element006  label="B_element : 006"  # scripted group (container) (typed FeaturePython)
  n = 4
  ref = B_element
FEATURE [App::DocumentObjectGroupPython] O_element061  label="O_element : 032"  # scripted group (container) (typed FeaturePython)
  n = 7
  ref = O_element
FEATURE [App::DocumentObjectGroupPython] G4_MAGNESIUM_TETRABORATE  # scripted group (container) (typed FeaturePython)
  Dunit = g/cm3
  Dvalue = 2.53
  Group = -> [Mg_element008,B_element006,O_element061]
  conduct = 2
  density = 1
  expand = 3
  formula = G4_MAGNESIUM_TETRABORATE
  name = G4_MAGNESIUM_TETRABORATE
  specific = 4
FEATURE [App::DocumentObjectGroupPython] Hg_element001  label="Hg_element : 1"  # scripted group (container) (typed FeaturePython)
  n = 1
  ref = Hg_element
FEATURE [App::DocumentObjectGroupPython] I_element004  label="I_element : 2"  # scripted group (container) (typed FeaturePython)
  n = 2
  ref = I_element
FEATURE [App::DocumentObjectGroupPython] G4_MERCURIC_IODIDE  # scripted group (container) (typed FeaturePython)
  Dunit = g/cm3
  Dvalue = 6.36
  Group = -> [Hg_element001,I_element004]
  conduct = 2
  density = 1
  expand = 3
  formula = G4_MERCURIC_IODIDE
  name = G4_MERCURIC_IODIDE
  specific = 4
FEATURE [App::DocumentObjectGroupPython] C_element059  label="C_element : 032"  # scripted group (container) (typed FeaturePython)
  n = 1
  ref = C_element
FEATURE [App::DocumentObjectGroupPython] H_element053  label="H_element : 028"  # scripted group (container) (typed FeaturePython)
  n = 4
  ref = H_element
FEATURE [App::DocumentObjectGroupPython] G4_METHANE  # scripted group (container) (typed FeaturePython)
  Dunit = g/cm3
  Dvalue = 0.000667151
  Group = -> [C_element059,H_element053]
  conduct = 2
  density = 1
  expand = 3
  formula = G4_METHANE
  name = G4_METHANE
  specific = 4
FEATURE [App::DocumentObjectGroupPython] C_element060  label="C_element : 033"  # scripted group (container) (typed FeaturePython)
  n = 1
  ref = C_element
FEATURE [App::DocumentObjectGroupPython] H_element054  label="H_element : 029"  # scripted group (container) (typed FeaturePython)
  n = 4
  ref = H_element
FEATURE [App::DocumentObjectGroupPython] O_element062  label="O_element : 033"  # scripted group (container) (typed FeaturePython)
  n = 1
  ref = O_element
FEATURE [App::DocumentObjectGroupPython] G4_METHANOL  # scripted group (container) (typed FeaturePython)
  Dunit = g/cm3
  Dvalue = 0.7914
  Group = -> [C_element060,H_element054,O_element062]
  conduct = 2
  density = 1
  expand = 3
  formula = G4_METHANOL
  name = G4_METHANOL
  specific = 4
FEATURE [App::DocumentObjectGroupPython] H_element055  label="H_element : 0.134"  # scripted group (container) (typed FeaturePython)
  n = 0.13404
FEATURE [App::DocumentObjectGroupPython] C_element061  label="C_element : 0.778"  # scripted group (container) (typed FeaturePython)
  n = 0.77796
FEATURE [App::DocumentObjectGroupPython] O_element063  label="O_element : 0.035"  # scripted group (container) (typed FeaturePython)
  n = 0.03502
FEATURE [App::DocumentObjectGroupPython] Mg_element009  label="Mg_element : 0.039"  # scripted group (container) (typed FeaturePython)
  n = 0.038594
FEATURE [App::DocumentObjectGroupPython] Ti_element002  label="Ti_element : 0.014"  # scripted group (container) (typed FeaturePython)
  n = 0.014386
FEATURE [App::DocumentObjectGroupPython] G4_MIX_D_WAX  # scripted group (container) (typed FeaturePython)
  Dunit = g/cm3
  Dvalue = 0.99
  Group = -> [H_element055,C_element061,O_element063,Mg_element009,Ti_element002]
  conduct = 2
  density = 1
  expand = 3
  formula = G4_MIX_D_WAX
  name = G4_MIX_D_WAX
  specific = 4
FEATURE [App::DocumentObjectGroupPython] H_element056  label="H_element : 0.135"  # scripted group (container) (typed FeaturePython)
  n = 0.081192
FEATURE [App::DocumentObjectGroupPython] C_element062  label="C_element : 0.583"  # scripted group (container) (typed FeaturePython)
  n = 0.583442
FEATURE [App::DocumentObjectGroupPython] N_element024  label="N_element : 0.018"  # scripted group (container) (typed FeaturePython)
  n = 0.017798
FEATURE [App::DocumentObjectGroupPython] O_element064  label="O_element : 0.186"  # scripted group (container) (typed FeaturePython)
  n = 0.186381
FEATURE [App::DocumentObjectGroupPython] Mg_element010  label="Mg_element : 0.130"  # scripted group (container) (typed FeaturePython)
  n = 0.130287
FEATURE [App::DocumentObjectGroupPython] Cl_element015  label="Cl_element : 0.588"  # scripted group (container) (typed FeaturePython)
  n = 0.0009
FEATURE [App::DocumentObjectGroupPython] G4_MS20_TISSUE  # scripted group (container) (typed FeaturePython)
  Dunit = g/cm3
  Dvalue = 1
  Group = -> [H_element056,C_element062,N_element024,O_element064,Mg_element010,Cl_element015]
  conduct = 2
  density = 1
  expand = 3
  formula = G4_MS20_TISSUE
  name = G4_MS20_TISSUE
  specific = 4
FEATURE [App::DocumentObjectGroupPython] H_element057  label="H_element : 0.136"  # scripted group (container) (typed FeaturePython)
  n = 0.102
FEATURE [App::DocumentObjectGroupPython] C_element063  label="C_element : 0.143"  # scripted group (container) (typed FeaturePython)
  n = 0.143
FEATURE [App::DocumentObjectGroupPython] N_element025  label="N_element : 0.034"  # scripted group (container) (typed FeaturePython)
  n = 0.034
FEATURE [App::DocumentObjectGroupPython] O_element065  label="O_element : 0.710"  # scripted group (container) (typed FeaturePython)
  n = 0.71
FEATURE [App::DocumentObjectGroupPython] Na_element011  label="Na_element : 0.098"  # scripted group (container) (typed FeaturePython)
  n = 0.001
FEATURE [App::DocumentObjectGroupPython] P_element007  label="P_element : 0.002"  # scripted group (container) (typed FeaturePython)
  n = 0.002
FEATURE [App::DocumentObjectGroupPython] S_element017  label="S_element : 0.018"  # scripted group (container) (typed FeaturePython)
  n = 0.003
FEATURE [App::DocumentObjectGroupPython] Cl_element016  label="Cl_element : 0.589"  # scripted group (container) (typed FeaturePython)
  n = 0.001
FEATURE [App::DocumentObjectGroupPython] K_element006  label="K_element : 0.004"  # scripted group (container) (typed FeaturePython)
  n = 0.004
FEATURE [App::DocumentObjectGroupPython] G4_MUSCLE_SKELETAL_ICRP  # scripted group (container) (typed FeaturePython)
  Dunit = g/cm3
  Dvalue = 1.05
  Group = -> [H_element057,C_element063,N_element025,O_element065,Na_element011,P_element007,S_element017,Cl_element016,K_element006]
  conduct = 2
  density = 1
  expand = 3
  formula = G4_MUSCLE_SKELETAL_ICRP
  name = G4_MUSCLE_SKELETAL_ICRP
  specific = 4
FEATURE [App::DocumentObjectGroupPython] H_element058  label="H_element : 0.137"  # scripted group (container) (typed FeaturePython)
  n = 0.102102
FEATURE [App::DocumentObjectGroupPython] C_element064  label="C_element : 0.123"  # scripted group (container) (typed FeaturePython)
  n = 0.123123
FEATURE [App::DocumentObjectGroupPython] N_element026  label="N_element : 0.756"  # scripted group (container) (typed FeaturePython)
  n = 0.035035
FEATURE [App::DocumentObjectGroupPython] O_element066  label="O_element : 0.730"  # scripted group (container) (typed FeaturePython)
  n = 0.72973
FEATURE [App::DocumentObjectGroupPython] Na_element012  label="Na_element : 0.099"  # scripted group (container) (typed FeaturePython)
  n = 0.001001
FEATURE [App::DocumentObjectGroupPython] P_element008  label="P_element : 0.106"  # scripted group (container) (typed FeaturePython)
  n = 0.002002
FEATURE [App::DocumentObjectGroupPython] S_element018  label="S_element : 0.019"  # scripted group (container) (typed FeaturePython)
  n = 0.004004
FEATURE [App::DocumentObjectGroupPython] K_element007  label="K_element : 0.016"  # scripted group (container) (typed FeaturePython)
  n = 0.003003
FEATURE [App::DocumentObjectGroupPython] G4_MUSCLE_STRIATED_ICRU  # scripted group (container) (typed FeaturePython)
  Dunit = g/cm3
  Dvalue = 1.04
  Group = -> [H_element058,C_element064,N_element026,O_element066,Na_element012,P_element008,S_element018,K_element007]
  conduct = 2
  density = 1
  expand = 3
  formula = G4_MUSCLE_STRIATED_ICRU
  name = G4_MUSCLE_STRIATED_ICRU
  specific = 4
FEATURE [App::DocumentObjectGroupPython] H_element059  label="H_element : 0.098"  # scripted group (container) (typed FeaturePython)
  n = 0.0982341
FEATURE [App::DocumentObjectGroupPython] C_element065  label="C_element : 0.156"  # scripted group (container) (typed FeaturePython)
  n = 0.156214
FEATURE [App::DocumentObjectGroupPython] N_element027  label="N_element : 0.757"  # scripted group (container) (typed FeaturePython)
  n = 0.035451
FEATURE [App::DocumentObjectGroupPython] O_element067  label="O_element : 0.880"  # scripted group (container) (typed FeaturePython)
  n = 0.710101
FEATURE [App::DocumentObjectGroupPython] G4_MUSCLE_WITH_SUCROSE  # scripted group (container) (typed FeaturePython)
  Dunit = g/cm3
  Dvalue = 1.11
  Group = -> [H_element059,C_element065,N_element027,O_element067]
  conduct = 2
  density = 1
  expand = 3
  formula = G4_MUSCLE_WITH_SUCROSE
  name = G4_MUSCLE_WITH_SUCROSE
  specific = 4
FEATURE [App::DocumentObjectGroupPython] H_element060  label="H_element : 0.138"  # scripted group (container) (typed FeaturePython)
  n = 0.101969
FEATURE [App::DocumentObjectGroupPython] C_element066  label="C_element : 0.120"  # scripted group (container) (typed FeaturePython)
  n = 0.120058
FEATURE [App::DocumentObjectGroupPython] N_element028  label="N_element : 0.758"  # scripted group (container) (typed FeaturePython)
  n = 0.035451
FEATURE [App::DocumentObjectGroupPython] O_element068  label="O_element : 0.743"  # scripted group (container) (typed FeaturePython)
  n = 0.742522
FEATURE [App::DocumentObjectGroupPython] G4_MUSCLE_WITHOUT_SUCROSE  # scripted group (container) (typed FeaturePython)
  Dunit = g/cm3
  Dvalue = 1.07
  Group = -> [H_element060,C_element066,N_element028,O_element068]
  conduct = 2
  density = 1
  expand = 3
  formula = G4_MUSCLE_WITHOUT_SUCROSE
  name = G4_MUSCLE_WITHOUT_SUCROSE
  specific = 4
FEATURE [App::DocumentObjectGroupPython] C_element067  label="C_element : 10"  # scripted group (container) (typed FeaturePython)
  n = 10
  ref = C_element
FEATURE [App::DocumentObjectGroupPython] H_element061  label="H_element : 030"  # scripted group (container) (typed FeaturePython)
  n = 8
  ref = H_element
FEATURE [App::DocumentObjectGroupPython] G4_NAPHTHALENE  # scripted group (container) (typed FeaturePython)
  Dunit = g/cm3
  Dvalue = 1.145
  Group = -> [C_element067,H_element061]
  conduct = 2
  density = 1
  expand = 3
  formula = G4_NAPHTHALENE
  name = G4_NAPHTHALENE
  specific = 4
FEATURE [App::DocumentObjectGroupPython] C_element068  label="C_element : 034"  # scripted group (container) (typed FeaturePython)
  n = 6
  ref = C_element
FEATURE [App::DocumentObjectGroupPython] H_element062  label="H_element : 031"  # scripted group (container) (typed FeaturePython)
  n = 5
  ref = H_element
FEATURE [App::DocumentObjectGroupPython] N_element029  label="N_element : 012"  # scripted group (container) (typed FeaturePython)
  n = 1
  ref = N_element
FEATURE [App::DocumentObjectGroupPython] O_element069  label="O_element : 034"  # scripted group (container) (typed FeaturePython)
  n = 2
  ref = O_element
FEATURE [App::DocumentObjectGroupPython] G4_NITROBENZENE  # scripted group (container) (typed FeaturePython)
  Dunit = g/cm3
  Dvalue = 1.19867
  Group = -> [C_element068,H_element062,N_element029,O_element069]
  conduct = 2
  density = 1
  expand = 3
  formula = G4_NITROBENZENE
  name = G4_NITROBENZENE
  specific = 4
FEATURE [App::DocumentObjectGroupPython] N_element030  label="N_element : 013"  # scripted group (container) (typed FeaturePython)
  n = 2
  ref = N_element
FEATURE [App::DocumentObjectGroupPython] O_element070  label="O_element : 035"  # scripted group (container) (typed FeaturePython)
  n = 1
  ref = O_element
FEATURE [App::DocumentObjectGroupPython] G4_NITROUS_OXIDE  # scripted group (container) (typed FeaturePython)
  Dunit = g/cm3
  Dvalue = 0.00183094
  Group = -> [N_element030,O_element070]
  conduct = 2
  density = 1
  expand = 3
  formula = G4_NITROUS_OXIDE
  name = G4_NITROUS_OXIDE
  specific = 4
FEATURE [App::DocumentObjectGroupPython] H_element063  label="H_element : 0.104"  # scripted group (container) (typed FeaturePython)
  n = 0.103509
FEATURE [App::DocumentObjectGroupPython] C_element069  label="C_element : 0.648"  # scripted group (container) (typed FeaturePython)
  n = 0.648416
FEATURE [App::DocumentObjectGroupPython] N_element031  label="N_element : 0.100"  # scripted group (container) (typed FeaturePython)
  n = 0.0995361
FEATURE [App::DocumentObjectGroupPython] O_element071  label="O_element : 0.149"  # scripted group (container) (typed FeaturePython)
  n = 0.148539
FEATURE [App::DocumentObjectGroupPython] G4_NYLON_8062  label="G4_NYLON-8062"  # scripted group (container) (typed FeaturePython)
  Dunit = g/cm3
  Dvalue = 1.08
  Group = -> [H_element063,C_element069,N_element031,O_element071]
  conduct = 2
  density = 1
  expand = 3
  formula = G4_NYLON-8062
  name = G4_NYLON-8062
  specific = 4
FEATURE [App::DocumentObjectGroupPython] C_element070  label="C_element : 035"  # scripted group (container) (typed FeaturePython)
  n = 6
  ref = C_element
FEATURE [App::DocumentObjectGroupPython] H_element064  label="H_element : 11"  # scripted group (container) (typed FeaturePython)
  n = 11
  ref = H_element
FEATURE [App::DocumentObjectGroupPython] N_element032  label="N_element : 014"  # scripted group (container) (typed FeaturePython)
  n = 1
  ref = N_element
FEATURE [App::DocumentObjectGroupPython] O_element072  label="O_element : 036"  # scripted group (container) (typed FeaturePython)
  n = 1
  ref = O_element
FEATURE [App::DocumentObjectGroupPython] G4_NYLON_6_6  label="G4_NYLON-6-6"  # scripted group (container) (typed FeaturePython)
  Dunit = g/cm3
  Dvalue = 1.14
  Group = -> [C_element070,H_element064,N_element032,O_element072]
  conduct = 2
  density = 1
  expand = 3
  formula = G4_NYLON-6-6
  name = G4_NYLON-6-6
  specific = 4
FEATURE [App::DocumentObjectGroupPython] H_element065  label="H_element : 0.139"  # scripted group (container) (typed FeaturePython)
  n = 0.107062
FEATURE [App::DocumentObjectGroupPython] C_element071  label="C_element : 0.680"  # scripted group (container) (typed FeaturePython)
  n = 0.680449
FEATURE [App::DocumentObjectGroupPython] N_element033  label="N_element : 0.099"  # scripted group (container) (typed FeaturePython)
  n = 0.099189
FEATURE [App::DocumentObjectGroupPython] O_element073  label="O_element : 0.113"  # scripted group (container) (typed FeaturePython)
  n = 0.1133
FEATURE [App::DocumentObjectGroupPython] G4_NYLON_6_10  label="G4_NYLON-6-10"  # scripted group (container) (typed FeaturePython)
  Dunit = g/cm3
  Dvalue = 1.14
  Group = -> [H_element065,C_element071,N_element033,O_element073]
  conduct = 2
  density = 1
  expand = 3
  formula = G4_NYLON-6-10
  name = G4_NYLON-6-10
  specific = 4
FEATURE [App::DocumentObjectGroupPython] H_element066  label="H_element : 0.140"  # scripted group (container) (typed FeaturePython)
  n = 0.115476
FEATURE [App::DocumentObjectGroupPython] C_element072  label="C_element : 0.721"  # scripted group (container) (typed FeaturePython)
  n = 0.720818
FEATURE [App::DocumentObjectGroupPython] N_element034  label="N_element : 0.076"  # scripted group (container) (typed FeaturePython)
  n = 0.0764169
FEATURE [App::DocumentObjectGroupPython] O_element074  label="O_element : 0.087"  # scripted group (container) (typed FeaturePython)
  n = 0.0872889
FEATURE [App::DocumentObjectGroupPython] G4_NYLON_11_RILSAN  label="G4_NYLON-11_RILSAN"  # scripted group (container) (typed FeaturePython)
  Dunit = g/cm3
  Dvalue = 1.425
  Group = -> [H_element066,C_element072,N_element034,O_element074]
  conduct = 2
  density = 1
  expand = 3
  formula = G4_NYLON-11_RILSAN
  name = G4_NYLON-11_RILSAN
  specific = 4
FEATURE [App::DocumentObjectGroupPython] C_element073  label="C_element : 8"  # scripted group (container) (typed FeaturePython)
  n = 8
  ref = C_element
FEATURE [App::DocumentObjectGroupPython] H_element067  label="H_element : 18"  # scripted group (container) (typed FeaturePython)
  n = 18
  ref = H_element
FEATURE [App::DocumentObjectGroupPython] G4_OCTANE  # scripted group (container) (typed FeaturePython)
  Dunit = g/cm3
  Dvalue = 0.7026
  Group = -> [C_element073,H_element067]
  conduct = 2
  density = 1
  expand = 3
  formula = G4_OCTANE
  name = G4_OCTANE
  specific = 4
FEATURE [App::DocumentObjectGroupPython] C_element074  label="C_element : 25"  # scripted group (container) (typed FeaturePython)
  n = 25
  ref = C_element
FEATURE [App::DocumentObjectGroupPython] H_element068  label="H_element : 52"  # scripted group (container) (typed FeaturePython)
  n = 52
  ref = H_element
FEATURE [App::DocumentObjectGroupPython] G4_PARAFFIN  # scripted group (container) (typed FeaturePython)
  Dunit = g/cm3
  Dvalue = 0.93
  Group = -> [C_element074,H_element068]
  conduct = 2
  density = 1
  expand = 3
  formula = G4_PARAFFIN
  name = G4_PARAFFIN
  specific = 4
FEATURE [App::DocumentObjectGroupPython] C_element075  label="C_element : 036"  # scripted group (container) (typed FeaturePython)
  n = 5
  ref = C_element
FEATURE [App::DocumentObjectGroupPython] H_element069  label="H_element : 032"  # scripted group (container) (typed FeaturePython)
  n = 12
  ref = H_element
FEATURE [App::DocumentObjectGroupPython] G4_N_PENTANE  label="G4_N-PENTANE"  # scripted group (container) (typed FeaturePython)
  Dunit = g/cm3
  Dvalue = 0.6262
  Group = -> [C_element075,H_element069]
  conduct = 2
  density = 1
  expand = 3
  formula = G4_N-PENTANE
  name = G4_N-PENTANE
  specific = 4
FEATURE [App::DocumentObjectGroupPython] H_element070  label="H_element : 0.014"  # scripted group (container) (typed FeaturePython)
  n = 0.0141
FEATURE [App::DocumentObjectGroupPython] C_element076  label="C_element : 0.072"  # scripted group (container) (typed FeaturePython)
  n = 0.072261
FEATURE [App::DocumentObjectGroupPython] N_element035  label="N_element : 0.019"  # scripted group (container) (typed FeaturePython)
  n = 0.01932
FEATURE [App::DocumentObjectGroupPython] O_element075  label="O_element : 0.066"  # scripted group (container) (typed FeaturePython)
  n = 0.066101
FEATURE [App::DocumentObjectGroupPython] S_element019  label="S_element : 0.020"  # scripted group (container) (typed FeaturePython)
  n = 0.00189
FEATURE [App::DocumentObjectGroupPython] Br_element004  label="Br_element : 0.349"  # scripted group (container) (typed FeaturePython)
  n = 0.349103
FEATURE [App::DocumentObjectGroupPython] Ag_element001  label="Ag_element : 0.474"  # scripted group (container) (typed FeaturePython)
  n = 0.474105
FEATURE [App::DocumentObjectGroupPython] I_element005  label="I_element : 0.003"  # scripted group (container) (typed FeaturePython)
  n = 0.00312
FEATURE [App::DocumentObjectGroupPython] G4_PHOTO_EMULSION  # scripted group (container) (typed FeaturePython)
  Dunit = g/cm3
  Dvalue = 3.815
  Group = -> [H_element070,C_element076,N_element035,O_element075,S_element019,Br_element004,Ag_element001,I_element005]
  conduct = 2
  density = 1
  expand = 3
  formula = G4_PHOTO_EMULSION
  name = G4_PHOTO_EMULSION
  specific = 4
FEATURE [App::DocumentObjectGroupPython] C_element077  label="C_element : 9"  # scripted group (container) (typed FeaturePython)
  n = 9
  ref = C_element
FEATURE [App::DocumentObjectGroupPython] H_element071  label="H_element : 033"  # scripted group (container) (typed FeaturePython)
  n = 10
  ref = H_element
FEATURE [App::DocumentObjectGroupPython] G4_PLASTIC_SC_VINYLTOLUENE  # scripted group (container) (typed FeaturePython)
  Dunit = g/cm3
  Dvalue = 1.032
  Group = -> [C_element077,H_element071]
  conduct = 2
  density = 1
  expand = 3
  formula = G4_PLASTIC_SC_VINYLTOLUENE
  name = G4_PLASTIC_SC_VINYLTOLUENE
  specific = 4
FEATURE [App::DocumentObjectGroupPython] Pu_element001  label="Pu_element : 1"  # scripted group (container) (typed FeaturePython)
  n = 1
  ref = Pu_element
FEATURE [App::DocumentObjectGroupPython] O_element076  label="O_element : 037"  # scripted group (container) (typed FeaturePython)
  n = 2
  ref = O_element
FEATURE [App::DocumentObjectGroupPython] G4_PLUTONIUM_DIOXIDE  # scripted group (container) (typed FeaturePython)
  Dunit = g/cm3
  Dvalue = 11.46
  Group = -> [Pu_element001,O_element076]
  conduct = 2
  density = 1
  expand = 3
  formula = G4_PLUTONIUM_DIOXIDE
  name = G4_PLUTONIUM_DIOXIDE
  specific = 4
FEATURE [App::DocumentObjectGroupPython] C_element078  label="C_element : 037"  # scripted group (container) (typed FeaturePython)
  n = 3
  ref = C_element
FEATURE [App::DocumentObjectGroupPython] H_element072  label="H_element : 034"  # scripted group (container) (typed FeaturePython)
  n = 3
  ref = H_element
FEATURE [App::DocumentObjectGroupPython] N_element036  label="N_element : 015"  # scripted group (container) (typed FeaturePython)
  n = 1
  ref = N_element
FEATURE [App::DocumentObjectGroupPython] G4_POLYACRYLONITRILE  # scripted group (container) (typed FeaturePython)
  Dunit = g/cm3
  Dvalue = 1.17
  Group = -> [C_element078,H_element072,N_element036]
  conduct = 2
  density = 1
  expand = 3
  formula = G4_POLYACRYLONITRILE
  name = G4_POLYACRYLONITRILE
  specific = 4
FEATURE [App::DocumentObjectGroupPython] C_element079  label="C_element : 16"  # scripted group (container) (typed FeaturePython)
  n = 16
  ref = C_element
FEATURE [App::DocumentObjectGroupPython] H_element073  label="H_element : 035"  # scripted group (container) (typed FeaturePython)
  n = 14
  ref = H_element
FEATURE [App::DocumentObjectGroupPython] O_element077  label="O_element : 038"  # scripted group (container) (typed FeaturePython)
  n = 3
  ref = O_element
FEATURE [App::DocumentObjectGroupPython] G4_POLYCARBONATE  # scripted group (container) (typed FeaturePython)
  Dunit = g/cm3
  Dvalue = 1.2
  Group = -> [C_element079,H_element073,O_element077]
  conduct = 2
  density = 1
  expand = 3
  formula = G4_POLYCARBONATE
  name = G4_POLYCARBONATE
  specific = 4
FEATURE [App::DocumentObjectGroupPython] C_element080  label="C_element : 038"  # scripted group (container) (typed FeaturePython)
  n = 8
  ref = C_element
FEATURE [App::DocumentObjectGroupPython] H_element074  label="H_element : 036"  # scripted group (container) (typed FeaturePython)
  n = 7
  ref = H_element
FEATURE [App::DocumentObjectGroupPython] Cl_element017  label="Cl_element : 007"  # scripted group (container) (typed FeaturePython)
  n = 1
  ref = Cl_element
FEATURE [App::DocumentObjectGroupPython] G4_POLYCHLOROSTYRENE  # scripted group (container) (typed FeaturePython)
  Dunit = g/cm3
  Dvalue = 1.3
  Group = -> [C_element080,H_element074,Cl_element017]
  conduct = 2
  density = 1
  expand = 3
  formula = G4_POLYCHLOROSTYRENE
  name = G4_POLYCHLOROSTYRENE
  specific = 4
FEATURE [App::DocumentObjectGroupPython] C_element081  label="C_element : 039"  # scripted group (container) (typed FeaturePython)
  n = 1
  ref = C_element
FEATURE [App::DocumentObjectGroupPython] H_element075  label="H_element : 037"  # scripted group (container) (typed FeaturePython)
  n = 2
  ref = H_element
FEATURE [App::DocumentObjectGroupPython] G4_POLYETHYLENE  # scripted group (container) (typed FeaturePython)
  Dunit = g/cm3
  Dvalue = 0.94
  Group = -> [C_element081,H_element075]
  conduct = 2
  density = 1
  expand = 3
  formula = G4_POLYETHYLENE
  name = G4_POLYETHYLENE
  specific = 4
FEATURE [App::DocumentObjectGroupPython] C_element082  label="C_element : 040"  # scripted group (container) (typed FeaturePython)
  n = 10
  ref = C_element
FEATURE [App::DocumentObjectGroupPython] H_element076  label="H_element : 038"  # scripted group (container) (typed FeaturePython)
  n = 8
  ref = H_element
FEATURE [App::DocumentObjectGroupPython] O_element078  label="O_element : 039"  # scripted group (container) (typed FeaturePython)
  n = 4
  ref = O_element
FEATURE [App::DocumentObjectGroupPython] G4_MYLAR  # scripted group (container) (typed FeaturePython)
  Dunit = g/cm3
  Dvalue = 1.4
  Group = -> [C_element082,H_element076,O_element078]
  conduct = 2
  density = 1
  expand = 3
  formula = G4_MYLAR
  name = G4_MYLAR
  specific = 4
FEATURE [App::DocumentObjectGroupPython] C_element083  label="C_element : 041"  # scripted group (container) (typed FeaturePython)
  n = 5
  ref = C_element
FEATURE [App::DocumentObjectGroupPython] H_element077  label="H_element : 039"  # scripted group (container) (typed FeaturePython)
  n = 8
  ref = H_element
FEATURE [App::DocumentObjectGroupPython] O_element079  label="O_element : 040"  # scripted group (container) (typed FeaturePython)
  n = 2
  ref = O_element
FEATURE [App::DocumentObjectGroupPython] G4_PLEXIGLASS  # scripted group (container) (typed FeaturePython)
  Dunit = g/cm3
  Dvalue = 1.19
  Group = -> [C_element083,H_element077,O_element079]
  conduct = 2
  density = 1
  expand = 3
  formula = G4_PLEXIGLASS
  name = G4_PLEXIGLASS
  specific = 4
FEATURE [App::DocumentObjectGroupPython] C_element084  label="C_element : 042"  # scripted group (container) (typed FeaturePython)
  n = 1
  ref = C_element
FEATURE [App::DocumentObjectGroupPython] H_element078  label="H_element : 040"  # scripted group (container) (typed FeaturePython)
  n = 2
  ref = H_element
FEATURE [App::DocumentObjectGroupPython] O_element080  label="O_element : 041"  # scripted group (container) (typed FeaturePython)
  n = 1
  ref = O_element
FEATURE [App::DocumentObjectGroupPython] G4_POLYOXYMETHYLENE  # scripted group (container) (typed FeaturePython)
  Dunit = g/cm3
  Dvalue = 1.425
  Group = -> [C_element084,H_element078,O_element080]
  conduct = 2
  density = 1
  expand = 3
  formula = G4_POLYOXYMETHYLENE
  name = G4_POLYOXYMETHYLENE
  specific = 4
FEATURE [App::DocumentObjectGroupPython] C_element085  label="C_element : 043"  # scripted group (container) (typed FeaturePython)
  n = 2
  ref = C_element
FEATURE [App::DocumentObjectGroupPython] H_element079  label="H_element : 041"  # scripted group (container) (typed FeaturePython)
  n = 4
  ref = H_element
FEATURE [App::DocumentObjectGroupPython] G4_POLYPROPYLENE  # scripted group (container) (typed FeaturePython)
  Dunit = g/cm3
  Dvalue = 0.9
  Group = -> [C_element085,H_element079]
  conduct = 2
  density = 1
  expand = 3
  formula = G4_POLYPROPYLENE
  name = G4_POLYPROPYLENE
  specific = 4
FEATURE [App::DocumentObjectGroupPython] C_element086  label="C_element : 044"  # scripted group (container) (typed FeaturePython)
  n = 8
  ref = C_element
FEATURE [App::DocumentObjectGroupPython] H_element080  label="H_element : 042"  # scripted group (container) (typed FeaturePython)
  n = 8
  ref = H_element
FEATURE [App::DocumentObjectGroupPython] G4_POLYSTYRENE  # scripted group (container) (typed FeaturePython)
  Dunit = g/cm3
  Dvalue = 1.06
  Group = -> [C_element086,H_element080]
  conduct = 2
  density = 1
  expand = 3
  formula = G4_POLYSTYRENE
  name = G4_POLYSTYRENE
  specific = 4
FEATURE [App::DocumentObjectGroupPython] C_element087  label="C_element : 045"  # scripted group (container) (typed FeaturePython)
  n = 2
  ref = C_element
FEATURE [App::DocumentObjectGroupPython] F_element014  label="F_element : 4"  # scripted group (container) (typed FeaturePython)
  n = 4
  ref = F_element
FEATURE [App::DocumentObjectGroupPython] G4_TEFLON  # scripted group (container) (typed FeaturePython)
  Dunit = g/cm3
  Dvalue = 2.2
  Group = -> [C_element087,F_element014]
  conduct = 2
  density = 1
  expand = 3
  formula = G4_TEFLON
  name = G4_TEFLON
  specific = 4
FEATURE [App::DocumentObjectGroupPython] C_element088  label="C_element : 046"  # scripted group (container) (typed FeaturePython)
  n = 2
  ref = C_element
FEATURE [App::DocumentObjectGroupPython] F_element015  label="F_element : 006"  # scripted group (container) (typed FeaturePython)
  n = 3
  ref = F_element
FEATURE [App::DocumentObjectGroupPython] Cl_element018  label="Cl_element : 008"  # scripted group (container) (typed FeaturePython)
  n = 1
  ref = Cl_element
FEATURE [App::DocumentObjectGroupPython] G4_POLYTRIFLUOROCHLOROETHYLENE  # scripted group (container) (typed FeaturePython)
  Dunit = g/cm3
  Dvalue = 2.1
  Group = -> [C_element088,F_element015,Cl_element018]
  conduct = 2
  density = 1
  expand = 3
  formula = G4_POLYTRIFLUOROCHLOROETHYLENE
  name = G4_POLYTRIFLUOROCHLOROETHYLENE
  specific = 4
FEATURE [App::DocumentObjectGroupPython] C_element089  label="C_element : 047"  # scripted group (container) (typed FeaturePython)
  n = 4
  ref = C_element
FEATURE [App::DocumentObjectGroupPython] H_element081  label="H_element : 043"  # scripted group (container) (typed FeaturePython)
  n = 6
  ref = H_element
FEATURE [App::DocumentObjectGroupPython] O_element081  label="O_element : 042"  # scripted group (container) (typed FeaturePython)
  n = 2
  ref = O_element
FEATURE [App::DocumentObjectGroupPython] G4_POLYVINYL_ACETATE  # scripted group (container) (typed FeaturePython)
  Dunit = g/cm3
  Dvalue = 1.19
  Group = -> [C_element089,H_element081,O_element081]
  conduct = 2
  density = 1
  expand = 3
  formula = G4_POLYVINYL_ACETATE
  name = G4_POLYVINYL_ACETATE
  specific = 4
FEATURE [App::DocumentObjectGroupPython] C_element090  label="C_element : 048"  # scripted group (container) (typed FeaturePython)
  n = 2
  ref = C_element
FEATURE [App::DocumentObjectGroupPython] H_element082  label="H_element : 044"  # scripted group (container) (typed FeaturePython)
  n = 4
  ref = H_element
FEATURE [App::DocumentObjectGroupPython] O_element082  label="O_element : 043"  # scripted group (container) (typed FeaturePython)
  n = 1
  ref = O_element
FEATURE [App::DocumentObjectGroupPython] G4_POLYVINYL_ALCOHOL  # scripted group (container) (typed FeaturePython)
  Dunit = g/cm3
  Dvalue = 1.3
  Group = -> [C_element090,H_element082,O_element082]
  conduct = 2
  density = 1
  expand = 3
  formula = G4_POLYVINYL_ALCOHOL
  name = G4_POLYVINYL_ALCOHOL
  specific = 4
FEATURE [App::DocumentObjectGroupPython] C_element091  label="C_element : 049"  # scripted group (container) (typed FeaturePython)
  n = 8
  ref = C_element
FEATURE [App::DocumentObjectGroupPython] H_element083  label="H_element : 045"  # scripted group (container) (typed FeaturePython)
  n = 14
  ref = H_element
FEATURE [App::DocumentObjectGroupPython] O_element083  label="O_element : 044"  # scripted group (container) (typed FeaturePython)
  n = 2
  ref = O_element
FEATURE [App::DocumentObjectGroupPython] G4_POLYVINYL_BUTYRAL  # scripted group (container) (typed FeaturePython)
  Dunit = g/cm3
  Dvalue = 1.12
  Group = -> [C_element091,H_element083,O_element083]
  conduct = 2
  density = 1
  expand = 3
  formula = G4_POLYVINYL_BUTYRAL
  name = G4_POLYVINYL_BUTYRAL
  specific = 4
FEATURE [App::DocumentObjectGroupPython] C_element092  label="C_element : 050"  # scripted group (container) (typed FeaturePython)
  n = 2
  ref = C_element
FEATURE [App::DocumentObjectGroupPython] H_element084  label="H_element : 046"  # scripted group (container) (typed FeaturePython)
  n = 3
  ref = H_element
FEATURE [App::DocumentObjectGroupPython] Cl_element019  label="Cl_element : 009"  # scripted group (container) (typed FeaturePython)
  n = 1
  ref = Cl_element
FEATURE [App::DocumentObjectGroupPython] G4_POLYVINYL_CHLORIDE  # scripted group (container) (typed FeaturePython)
  Dunit = g/cm3
  Dvalue = 1.3
  Group = -> [C_element092,H_element084,Cl_element019]
  conduct = 2
  density = 1
  expand = 3
  formula = G4_POLYVINYL_CHLORIDE
  name = G4_POLYVINYL_CHLORIDE
  specific = 4
FEATURE [App::DocumentObjectGroupPython] C_element093  label="C_element : 051"  # scripted group (container) (typed FeaturePython)
  n = 2
  ref = C_element
FEATURE [App::DocumentObjectGroupPython] H_element085  label="H_element : 047"  # scripted group (container) (typed FeaturePython)
  n = 2
  ref = H_element
FEATURE [App::DocumentObjectGroupPython] Cl_element020  label="Cl_element : 010"  # scripted group (container) (typed FeaturePython)
  n = 2
  ref = Cl_element
FEATURE [App::DocumentObjectGroupPython] G4_POLYVINYLIDENE_CHLORIDE  # scripted group (container) (typed FeaturePython)
  Dunit = g/cm3
  Dvalue = 1.7
  Group = -> [C_element093,H_element085,Cl_element020]
  conduct = 2
  density = 1
  expand = 3
  formula = G4_POLYVINYLIDENE_CHLORIDE
  name = G4_POLYVINYLIDENE_CHLORIDE
  specific = 4
FEATURE [App::DocumentObjectGroupPython] C_element094  label="C_element : 052"  # scripted group (container) (typed FeaturePython)
  n = 2
  ref = C_element
FEATURE [App::DocumentObjectGroupPython] H_element086  label="H_element : 048"  # scripted group (container) (typed FeaturePython)
  n = 2
  ref = H_element
FEATURE [App::DocumentObjectGroupPython] F_element016  label="F_element : 007"  # scripted group (container) (typed FeaturePython)
  n = 2
  ref = F_element
FEATURE [App::DocumentObjectGroupPython] G4_POLYVINYLIDENE_FLUORIDE  # scripted group (container) (typed FeaturePython)
  Dunit = g/cm3
  Dvalue = 1.76
  Group = -> [C_element094,H_element086,F_element016]
  conduct = 2
  density = 1
  expand = 3
  formula = G4_POLYVINYLIDENE_FLUORIDE
  name = G4_POLYVINYLIDENE_FLUORIDE
  specific = 4
FEATURE [App::DocumentObjectGroupPython] C_element095  label="C_element : 053"  # scripted group (container) (typed FeaturePython)
  n = 6
  ref = C_element
FEATURE [App::DocumentObjectGroupPython] H_element087  label="H_element : 9"  # scripted group (container) (typed FeaturePython)
  n = 9
  ref = H_element
FEATURE [App::DocumentObjectGroupPython] N_element037  label="N_element : 016"  # scripted group (container) (typed FeaturePython)
  n = 1
  ref = N_element
FEATURE [App::DocumentObjectGroupPython] O_element084  label="O_element : 045"  # scripted group (container) (typed FeaturePython)
  n = 1
  ref = O_element
FEATURE [App::DocumentObjectGroupPython] G4_POLYVINYL_PYRROLIDONE  # scripted group (container) (typed FeaturePython)
  Dunit = g/cm3
  Dvalue = 1.25
  Group = -> [C_element095,H_element087,N_element037,O_element084]
  conduct = 2
  density = 1
  expand = 3
  formula = G4_POLYVINYL_PYRROLIDONE
  name = G4_POLYVINYL_PYRROLIDONE
  specific = 4
FEATURE [App::DocumentObjectGroupPython] K_element008  label="K_element : 1"  # scripted group (container) (typed FeaturePython)
  n = 1
  ref = K_element
FEATURE [App::DocumentObjectGroupPython] I_element006  label="I_element : 003"  # scripted group (container) (typed FeaturePython)
  n = 1
  ref = I_element
FEATURE [App::DocumentObjectGroupPython] G4_POTASSIUM_IODIDE  # scripted group (container) (typed FeaturePython)
  Dunit = g/cm3
  Dvalue = 3.13
  Group = -> [K_element008,I_element006]
  conduct = 2
  density = 1
  expand = 3
  formula = G4_POTASSIUM_IODIDE
  name = G4_POTASSIUM_IODIDE
  specific = 4
FEATURE [App::DocumentObjectGroupPython] K_element009  label="K_element : 2"  # scripted group (container) (typed FeaturePython)
  n = 2
  ref = K_element
FEATURE [App::DocumentObjectGroupPython] O_element085  label="O_element : 046"  # scripted group (container) (typed FeaturePython)
  n = 1
  ref = O_element
FEATURE [App::DocumentObjectGroupPython] G4_POTASSIUM_OXIDE  # scripted group (container) (typed FeaturePython)
  Dunit = g/cm3
  Dvalue = 2.32
  Group = -> [K_element009,O_element085]
  conduct = 2
  density = 1
  expand = 3
  formula = G4_POTASSIUM_OXIDE
  name = G4_POTASSIUM_OXIDE
  specific = 4
FEATURE [App::DocumentObjectGroupPython] C_element096  label="C_element : 054"  # scripted group (container) (typed FeaturePython)
  n = 3
  ref = C_element
FEATURE [App::DocumentObjectGroupPython] H_element088  label="H_element : 049"  # scripted group (container) (typed FeaturePython)
  n = 8
  ref = H_element
FEATURE [App::DocumentObjectGroupPython] G4_PROPANE  # scripted group (container) (typed FeaturePython)
  Dunit = g/cm3
  Dvalue = 0.00187939
  Group = -> [C_element096,H_element088]
  conduct = 2
  density = 1
  expand = 3
  formula = G4_PROPANE
  name = G4_PROPANE
  specific = 4
FEATURE [App::DocumentObjectGroupPython] C_element097  label="C_element : 055"  # scripted group (container) (typed FeaturePython)
  n = 3
  ref = C_element
FEATURE [App::DocumentObjectGroupPython] H_element089  label="H_element : 050"  # scripted group (container) (typed FeaturePython)
  n = 8
  ref = H_element
FEATURE [App::DocumentObjectGroupPython] G4_lPROPANE  # scripted group (container) (typed FeaturePython)
  Dunit = g/cm3
  Dvalue = 0.43
  Group = -> [C_element097,H_element089]
  conduct = 2
  density = 1
  expand = 3
  formula = G4_lPROPANE
  name = G4_lPROPANE
  specific = 4
FEATURE [App::DocumentObjectGroupPython] C_element098  label="C_element : 056"  # scripted group (container) (typed FeaturePython)
  n = 3
  ref = C_element
FEATURE [App::DocumentObjectGroupPython] H_element090  label="H_element : 051"  # scripted group (container) (typed FeaturePython)
  n = 8
  ref = H_element
FEATURE [App::DocumentObjectGroupPython] O_element086  label="O_element : 047"  # scripted group (container) (typed FeaturePython)
  n = 1
  ref = O_element
FEATURE [App::DocumentObjectGroupPython] G4_N_PROPYL_ALCOHOL  label="G4_N-PROPYL_ALCOHOL"  # scripted group (container) (typed FeaturePython)
  Dunit = g/cm3
  Dvalue = 0.8035
  Group = -> [C_element098,H_element090,O_element086]
  conduct = 2
  density = 1
  expand = 3
  formula = G4_N-PROPYL_ALCOHOL
  name = G4_N-PROPYL_ALCOHOL
  specific = 4
FEATURE [App::DocumentObjectGroupPython] C_element099  label="C_element : 057"  # scripted group (container) (typed FeaturePython)
  n = 5
  ref = C_element
FEATURE [App::DocumentObjectGroupPython] H_element091  label="H_element : 052"  # scripted group (container) (typed FeaturePython)
  n = 5
  ref = H_element
FEATURE [App::DocumentObjectGroupPython] N_element038  label="N_element : 017"  # scripted group (container) (typed FeaturePython)
  n = 1
  ref = N_element
FEATURE [App::DocumentObjectGroupPython] G4_PYRIDINE  # scripted group (container) (typed FeaturePython)
  Dunit = g/cm3
  Dvalue = 0.9819
  Group = -> [C_element099,H_element091,N_element038]
  conduct = 2
  density = 1
  expand = 3
  formula = G4_PYRIDINE
  name = G4_PYRIDINE
  specific = 4
FEATURE [App::DocumentObjectGroupPython] H_element092  label="H_element : 0.144"  # scripted group (container) (typed FeaturePython)
  n = 0.143711
FEATURE [App::DocumentObjectGroupPython] C_element100  label="C_element : 0.856"  # scripted group (container) (typed FeaturePython)
  n = 0.856289
FEATURE [App::DocumentObjectGroupPython] G4_RUBBER_BUTYL  # scripted group (container) (typed FeaturePython)
  Dunit = g/cm3
  Dvalue = 0.92
  Group = -> [H_element092,C_element100]
  conduct = 2
  density = 1
  expand = 3
  formula = G4_RUBBER_BUTYL
  name = G4_RUBBER_BUTYL
  specific = 4
FEATURE [App::DocumentObjectGroupPython] H_element093  label="H_element : 0.118"  # scripted group (container) (typed FeaturePython)
  n = 0.118371
FEATURE [App::DocumentObjectGroupPython] C_element101  label="C_element : 0.882"  # scripted group (container) (typed FeaturePython)
  n = 0.881629
FEATURE [App::DocumentObjectGroupPython] G4_RUBBER_NATURAL  # scripted group (container) (typed FeaturePython)
  Dunit = g/cm3
  Dvalue = 0.92
  Group = -> [H_element093,C_element101]
  conduct = 2
  density = 1
  expand = 3
  formula = G4_RUBBER_NATURAL
  name = G4_RUBBER_NATURAL
  specific = 4
FEATURE [App::DocumentObjectGroupPython] H_element094  label="H_element : 0.145"  # scripted group (container) (typed FeaturePython)
  n = 0.05692
FEATURE [App::DocumentObjectGroupPython] C_element102  label="C_element : 0.543"  # scripted group (container) (typed FeaturePython)
  n = 0.542646
FEATURE [App::DocumentObjectGroupPython] Cl_element021  label="Cl_element : 0.400"  # scripted group (container) (typed FeaturePython)
  n = 0.400434
FEATURE [App::DocumentObjectGroupPython] G4_RUBBER_NEOPRENE  # scripted group (container) (typed FeaturePython)
  Dunit = g/cm3
  Dvalue = 1.23
  Group = -> [H_element094,C_element102,Cl_element021]
  conduct = 2
  density = 1
  expand = 3
  formula = G4_RUBBER_NEOPRENE
  name = G4_RUBBER_NEOPRENE
  specific = 4
FEATURE [App::DocumentObjectGroupPython] Si_element006  label="Si_element : 1"  # scripted group (container) (typed FeaturePython)
  n = 1
  ref = Si_element
FEATURE [App::DocumentObjectGroupPython] O_element087  label="O_element : 048"  # scripted group (container) (typed FeaturePython)
  n = 2
  ref = O_element
FEATURE [App::DocumentObjectGroupPython] G4_SILICON_DIOXIDE  # scripted group (container) (typed FeaturePython)
  Dunit = g/cm3
  Dvalue = 2.32
  Group = -> [Si_element006,O_element087]
  conduct = 2
  density = 1
  expand = 3
  formula = G4_SILICON_DIOXIDE
  name = G4_SILICON_DIOXIDE
  specific = 4
FEATURE [App::DocumentObjectGroupPython] Ag_element002  label="Ag_element : 1"  # scripted group (container) (typed FeaturePython)
  n = 1
  ref = Ag_element
FEATURE [App::DocumentObjectGroupPython] Br_element005  label="Br_element : 003"  # scripted group (container) (typed FeaturePython)
  n = 1
  ref = Br_element
FEATURE [App::DocumentObjectGroupPython] G4_SILVER_BROMIDE  # scripted group (container) (typed FeaturePython)
  Dunit = g/cm3
  Dvalue = 6.473
  Group = -> [Ag_element002,Br_element005]
  conduct = 2
  density = 1
  expand = 3
  formula = G4_SILVER_BROMIDE
  name = G4_SILVER_BROMIDE
  specific = 4
FEATURE [App::DocumentObjectGroupPython] Ag_element003  label="Ag_element : 002"  # scripted group (container) (typed FeaturePython)
  n = 1
  ref = Ag_element
FEATURE [App::DocumentObjectGroupPython] Cl_element022  label="Cl_element : 011"  # scripted group (container) (typed FeaturePython)
  n = 1
  ref = Cl_element
FEATURE [App::DocumentObjectGroupPython] G4_SILVER_CHLORIDE  # scripted group (container) (typed FeaturePython)
  Dunit = g/cm3
  Dvalue = 5.56
  Group = -> [Ag_element003,Cl_element022]
  conduct = 2
  density = 1
  expand = 3
  formula = G4_SILVER_CHLORIDE
  name = G4_SILVER_CHLORIDE
  specific = 4
FEATURE [App::DocumentObjectGroupPython] Br_element006  label="Br_element : 0.423"  # scripted group (container) (typed FeaturePython)
  n = 0.422895
FEATURE [App::DocumentObjectGroupPython] Ag_element004  label="Ag_element : 0.574"  # scripted group (container) (typed FeaturePython)
  n = 0.573748
FEATURE [App::DocumentObjectGroupPython] I_element007  label="I_element : 0.649"  # scripted group (container) (typed FeaturePython)
  n = 0.003357
FEATURE [App::DocumentObjectGroupPython] G4_SILVER_HALIDES  # scripted group (container) (typed FeaturePython)
  Dunit = g/cm3
  Dvalue = 6.47
  Group = -> [Br_element006,Ag_element004,I_element007]
  conduct = 2
  density = 1
  expand = 3
  formula = G4_SILVER_HALIDES
  name = G4_SILVER_HALIDES
  specific = 4
FEATURE [App::DocumentObjectGroupPython] Ag_element005  label="Ag_element : 003"  # scripted group (container) (typed FeaturePython)
  n = 1
  ref = Ag_element
FEATURE [App::DocumentObjectGroupPython] I_element008  label="I_element : 004"  # scripted group (container) (typed FeaturePython)
  n = 1
  ref = I_element
FEATURE [App::DocumentObjectGroupPython] G4_SILVER_IODIDE  # scripted group (container) (typed FeaturePython)
  Dunit = g/cm3
  Dvalue = 6.01
  Group = -> [Ag_element005,I_element008]
  conduct = 2
  density = 1
  expand = 3
  formula = G4_SILVER_IODIDE
  name = G4_SILVER_IODIDE
  specific = 4
FEATURE [App::DocumentObjectGroupPython] H_element095  label="H_element : 0.100"  # scripted group (container) (typed FeaturePython)
  n = 0.1
FEATURE [App::DocumentObjectGroupPython] C_element103  label="C_element : 0.204"  # scripted group (container) (typed FeaturePython)
  n = 0.204
FEATURE [App::DocumentObjectGroupPython] N_element039  label="N_element : 0.759"  # scripted group (container) (typed FeaturePython)
  n = 0.042
FEATURE [App::DocumentObjectGroupPython] O_element088  label="O_element : 0.645"  # scripted group (container) (typed FeaturePython)
  n = 0.645
FEATURE [App::DocumentObjectGroupPython] Na_element013  label="Na_element : 0.100"  # scripted group (container) (typed FeaturePython)
  n = 0.002
FEATURE [App::DocumentObjectGroupPython] P_element009  label="P_element : 0.107"  # scripted group (container) (typed FeaturePython)
  n = 0.001
FEATURE [App::DocumentObjectGroupPython] S_element020  label="S_element : 0.021"  # scripted group (container) (typed FeaturePython)
  n = 0.002
FEATURE [App::DocumentObjectGroupPython] Cl_element023  label="Cl_element : 0.590"  # scripted group (container) (typed FeaturePython)
  n = 0.003
FEATURE [App::DocumentObjectGroupPython] K_element010  label="K_element : 0.001"  # scripted group (container) (typed FeaturePython)
  n = 0.001
FEATURE [App::DocumentObjectGroupPython] G4_SKIN_ICRP  # scripted group (container) (typed FeaturePython)
  Dunit = g/cm3
  Dvalue = 1.09
  Group = -> [H_element095,C_element103,N_element039,O_element088,Na_element013,P_element009,S_element020,Cl_element023,K_element010]
  conduct = 2
  density = 1
  expand = 3
  formula = G4_SKIN_ICRP
  name = G4_SKIN_ICRP
  specific = 4
FEATURE [App::DocumentObjectGroupPython] Na_element014  label="Na_element : 2"  # scripted group (container) (typed FeaturePython)
  n = 2
  ref = Na_element
FEATURE [App::DocumentObjectGroupPython] C_element104  label="C_element : 058"  # scripted group (container) (typed FeaturePython)
  n = 1
  ref = C_element
FEATURE [App::DocumentObjectGroupPython] O_element089  label="O_element : 049"  # scripted group (container) (typed FeaturePython)
  n = 3
  ref = O_element
FEATURE [App::DocumentObjectGroupPython] G4_SODIUM_CARBONATE  # scripted group (container) (typed FeaturePython)
  Dunit = g/cm3
  Dvalue = 2.532
  Group = -> [Na_element014,C_element104,O_element089]
  conduct = 2
  density = 1
  expand = 3
  formula = G4_SODIUM_CARBONATE
  name = G4_SODIUM_CARBONATE
  specific = 4
FEATURE [App::DocumentObjectGroupPython] Na_element015  label="Na_element : 1"  # scripted group (container) (typed FeaturePython)
  n = 1
  ref = Na_element
FEATURE [App::DocumentObjectGroupPython] I_element009  label="I_element : 005"  # scripted group (container) (typed FeaturePython)
  n = 1
  ref = I_element
FEATURE [App::DocumentObjectGroupPython] G4_SODIUM_IODIDE  # scripted group (container) (typed FeaturePython)
  Dunit = g/cm3
  Dvalue = 3.667
  Group = -> [Na_element015,I_element009]
  conduct = 2
  density = 1
  expand = 3
  formula = G4_SODIUM_IODIDE
  name = G4_SODIUM_IODIDE
  specific = 4
FEATURE [App::DocumentObjectGroupPython] Na_element016  label="Na_element : 003"  # scripted group (container) (typed FeaturePython)
  n = 2
  ref = Na_element
FEATURE [App::DocumentObjectGroupPython] O_element090  label="O_element : 050"  # scripted group (container) (typed FeaturePython)
  n = 1
  ref = O_element
FEATURE [App::DocumentObjectGroupPython] G4_SODIUM_MONOXIDE  # scripted group (container) (typed FeaturePython)
  Dunit = g/cm3
  Dvalue = 2.27
  Group = -> [Na_element016,O_element090]
  conduct = 2
  density = 1
  expand = 3
  formula = G4_SODIUM_MONOXIDE
  name = G4_SODIUM_MONOXIDE
  specific = 4
FEATURE [App::DocumentObjectGroupPython] Na_element017  label="Na_element : 004"  # scripted group (container) (typed FeaturePython)
  n = 1
  ref = Na_element
FEATURE [App::DocumentObjectGroupPython] N_element040  label="N_element : 018"  # scripted group (container) (typed FeaturePython)
  n = 1
  ref = N_element
FEATURE [App::DocumentObjectGroupPython] O_element091  label="O_element : 051"  # scripted group (container) (typed FeaturePython)
  n = 3
  ref = O_element
FEATURE [App::DocumentObjectGroupPython] G4_SODIUM_NITRATE  # scripted group (container) (typed FeaturePython)
  Dunit = g/cm3
  Dvalue = 2.261
  Group = -> [Na_element017,N_element040,O_element091]
  conduct = 2
  density = 1
  expand = 3
  formula = G4_SODIUM_NITRATE
  name = G4_SODIUM_NITRATE
  specific = 4
FEATURE [App::DocumentObjectGroupPython] C_element105  label="C_element : 059"  # scripted group (container) (typed FeaturePython)
  n = 14
  ref = C_element
FEATURE [App::DocumentObjectGroupPython] H_element096  label="H_element : 053"  # scripted group (container) (typed FeaturePython)
  n = 12
  ref = H_element
FEATURE [App::DocumentObjectGroupPython] G4_STILBENE  # scripted group (container) (typed FeaturePython)
  Dunit = g/cm3
  Dvalue = 0.9707
  Group = -> [C_element105,H_element096]
  conduct = 2
  density = 1
  expand = 3
  formula = G4_STILBENE
  name = G4_STILBENE
  specific = 4
FEATURE [App::DocumentObjectGroupPython] C_element106  label="C_element : 12"  # scripted group (container) (typed FeaturePython)
  n = 12
  ref = C_element
FEATURE [App::DocumentObjectGroupPython] H_element097  label="H_element : 22"  # scripted group (container) (typed FeaturePython)
  n = 22
  ref = H_element
FEATURE [App::DocumentObjectGroupPython] O_element092  label="O_element : 11"  # scripted group (container) (typed FeaturePython)
  n = 11
  ref = O_element
FEATURE [App::DocumentObjectGroupPython] G4_SUCROSE  # scripted group (container) (typed FeaturePython)
  Dunit = g/cm3
  Dvalue = 1.5805
  Group = -> [C_element106,H_element097,O_element092]
  conduct = 2
  density = 1
  expand = 3
  formula = G4_SUCROSE
  name = G4_SUCROSE
  specific = 4
FEATURE [App::DocumentObjectGroupPython] C_element107  label="C_element : 18"  # scripted group (container) (typed FeaturePython)
  n = 18
  ref = C_element
FEATURE [App::DocumentObjectGroupPython] H_element098  label="H_element : 054"  # scripted group (container) (typed FeaturePython)
  n = 14
  ref = H_element
FEATURE [App::DocumentObjectGroupPython] G4_TERPHENYL  # scripted group (container) (typed FeaturePython)
  Dunit = g/cm3
  Dvalue = 1.24
  Group = -> [C_element107,H_element098]
  conduct = 2
  density = 1
  expand = 3
  formula = G4_TERPHENYL
  name = G4_TERPHENYL
  specific = 4
FEATURE [App::DocumentObjectGroupPython] H_element099  label="H_element : 0.146"  # scripted group (container) (typed FeaturePython)
  n = 0.106
FEATURE [App::DocumentObjectGroupPython] C_element108  label="C_element : 0.883"  # scripted group (container) (typed FeaturePython)
  n = 0.099
FEATURE [App::DocumentObjectGroupPython] N_element041  label="N_element : 0.020"  # scripted group (container) (typed FeaturePython)
  n = 0.02
FEATURE [App::DocumentObjectGroupPython] O_element093  label="O_element : 0.766"  # scripted group (container) (typed FeaturePython)
  n = 0.766
FEATURE [App::DocumentObjectGroupPython] Na_element018  label="Na_element : 0.101"  # scripted group (container) (typed FeaturePython)
  n = 0.002
FEATURE [App::DocumentObjectGroupPython] P_element010  label="P_element : 0.108"  # scripted group (container) (typed FeaturePython)
  n = 0.001
FEATURE [App::DocumentObjectGroupPython] S_element021  label="S_element : 0.022"  # scripted group (container) (typed FeaturePython)
  n = 0.002
FEATURE [App::DocumentObjectGroupPython] Cl_element024  label="Cl_element : 0.002"  # scripted group (container) (typed FeaturePython)
  n = 0.002
FEATURE [App::DocumentObjectGroupPython] K_element011  label="K_element : 0.017"  # scripted group (container) (typed FeaturePython)
  n = 0.002
FEATURE [App::DocumentObjectGroupPython] G4_TESTIS_ICRP  # scripted group (container) (typed FeaturePython)
  Dunit = g/cm3
  Dvalue = 1.04
  Group = -> [H_element099,C_element108,N_element041,O_element093,Na_element018,P_element010,S_element021,Cl_element024,K_element011]
  conduct = 2
  density = 1
  expand = 3
  formula = G4_TESTIS_ICRP
  name = G4_TESTIS_ICRP
  specific = 4
FEATURE [App::DocumentObjectGroupPython] C_element109  label="C_element : 060"  # scripted group (container) (typed FeaturePython)
  n = 2
  ref = C_element
FEATURE [App::DocumentObjectGroupPython] Cl_element025  label="Cl_element : 012"  # scripted group (container) (typed FeaturePython)
  n = 4
  ref = Cl_element
FEATURE [App::DocumentObjectGroupPython] G4_TETRACHLOROETHYLENE  # scripted group (container) (typed FeaturePython)
  Dunit = g/cm3
  Dvalue = 1.625
  Group = -> [C_element109,Cl_element025]
  conduct = 2
  density = 1
  expand = 3
  formula = G4_TETRACHLOROETHYLENE
  name = G4_TETRACHLOROETHYLENE
  specific = 4
FEATURE [App::DocumentObjectGroupPython] Tl_element001  label="Tl_element : 1"  # scripted group (container) (typed FeaturePython)
  n = 1
  ref = Tl_element
FEATURE [App::DocumentObjectGroupPython] Cl_element026  label="Cl_element : 013"  # scripted group (container) (typed FeaturePython)
  n = 1
  ref = Cl_element
FEATURE [App::DocumentObjectGroupPython] G4_THALLIUM_CHLORIDE  # scripted group (container) (typed FeaturePython)
  Dunit = g/cm3
  Dvalue = 7.004
  Group = -> [Tl_element001,Cl_element026]
  conduct = 2
  density = 1
  expand = 3
  formula = G4_THALLIUM_CHLORIDE
  name = G4_THALLIUM_CHLORIDE
  specific = 4
FEATURE [App::DocumentObjectGroupPython] H_element100  label="H_element : 0.147"  # scripted group (container) (typed FeaturePython)
  n = 0.105
FEATURE [App::DocumentObjectGroupPython] C_element110  label="C_element : 0.256"  # scripted group (container) (typed FeaturePython)
  n = 0.256
FEATURE [App::DocumentObjectGroupPython] N_element042  label="N_element : 0.760"  # scripted group (container) (typed FeaturePython)
  n = 0.027
FEATURE [App::DocumentObjectGroupPython] O_element094  label="O_element : 0.602"  # scripted group (container) (typed FeaturePython)
  n = 0.602
FEATURE [App::DocumentObjectGroupPython] Na_element019  label="Na_element : 0.102"  # scripted group (container) (typed FeaturePython)
  n = 0.001
FEATURE [App::DocumentObjectGroupPython] P_element011  label="P_element : 0.109"  # scripted group (container) (typed FeaturePython)
  n = 0.002
FEATURE [App::DocumentObjectGroupPython] S_element022  label="S_element : 0.023"  # scripted group (container) (typed FeaturePython)
  n = 0.003
FEATURE [App::DocumentObjectGroupPython] Cl_element027  label="Cl_element : 0.591"  # scripted group (container) (typed FeaturePython)
  n = 0.002
FEATURE [App::DocumentObjectGroupPython] K_element012  label="K_element : 0.018"  # scripted group (container) (typed FeaturePython)
  n = 0.002
FEATURE [App::DocumentObjectGroupPython] G4_TISSUE_SOFT_ICRP  # scripted group (container) (typed FeaturePython)
  Dunit = g/cm3
  Dvalue = 1.03
  Group = -> [H_element100,C_element110,N_element042,O_element094,Na_element019,P_element011,S_element022,Cl_element027,K_element012]
  conduct = 2
  density = 1
  expand = 3
  formula = G4_TISSUE_SOFT_ICRP
  name = G4_TISSUE_SOFT_ICRP
  specific = 4
FEATURE [App::DocumentObjectGroupPython] H_element101  label="H_element : 0.148"  # scripted group (container) (typed FeaturePython)
  n = 0.101
FEATURE [App::DocumentObjectGroupPython] C_element111  label="C_element : 0.111"  # scripted group (container) (typed FeaturePython)
  n = 0.111
FEATURE [App::DocumentObjectGroupPython] N_element043  label="N_element : 0.026"  # scripted group (container) (typed FeaturePython)
  n = 0.026
FEATURE [App::DocumentObjectGroupPython] O_element095  label="O_element : 0.762"  # scripted group (container) (typed FeaturePython)
  n = 0.762
FEATURE [App::DocumentObjectGroupPython] G4_TISSUE_SOFT_ICRU_4  label="G4_TISSUE_SOFT_ICRU-4"  # scripted group (container) (typed FeaturePython)
  Dunit = g/cm3
  Dvalue = 1
  Group = -> [H_element101,C_element111,N_element043,O_element095]
  conduct = 2
  density = 1
  expand = 3
  formula = G4_TISSUE_SOFT_ICRU-4
  name = G4_TISSUE_SOFT_ICRU-4
  specific = 4
FEATURE [App::DocumentObjectGroupPython] H_element102  label="H_element : 0.149"  # scripted group (container) (typed FeaturePython)
  n = 0.101869
FEATURE [App::DocumentObjectGroupPython] C_element112  label="C_element : 0.456"  # scripted group (container) (typed FeaturePython)
  n = 0.456179
FEATURE [App::DocumentObjectGroupPython] N_element044  label="N_element : 0.761"  # scripted group (container) (typed FeaturePython)
  n = 0.035172
FEATURE [App::DocumentObjectGroupPython] O_element096  label="O_element : 0.407"  # scripted group (container) (typed FeaturePython)
  n = 0.40678
FEATURE [App::DocumentObjectGroupPython] G4_TISSUE_METHANE  label="G4_TISSUE-METHANE"  # scripted group (container) (typed FeaturePython)
  Dunit = g/cm3
  Dvalue = 0.00106409
  Group = -> [H_element102,C_element112,N_element044,O_element096]
  conduct = 2
  density = 1
  expand = 3
  formula = G4_TISSUE-METHANE
  name = G4_TISSUE-METHANE
  specific = 4
FEATURE [App::DocumentObjectGroupPython] H_element103  label="H_element : 0.103"  # scripted group (container) (typed FeaturePython)
  n = 0.102672
FEATURE [App::DocumentObjectGroupPython] C_element113  label="C_element : 0.569"  # scripted group (container) (typed FeaturePython)
  n = 0.56894
FEATURE [App::DocumentObjectGroupPython] N_element045  label="N_element : 0.762"  # scripted group (container) (typed FeaturePython)
  n = 0.035022
FEATURE [App::DocumentObjectGroupPython] O_element097  label="O_element : 0.293"  # scripted group (container) (typed FeaturePython)
  n = 0.293366
FEATURE [App::DocumentObjectGroupPython] G4_TISSUE_PROPANE  label="G4_TISSUE-PROPANE"  # scripted group (container) (typed FeaturePython)
  Dunit = g/cm3
  Dvalue = 0.00182628
  Group = -> [H_element103,C_element113,N_element045,O_element097]
  conduct = 2
  density = 1
  expand = 3
  formula = G4_TISSUE-PROPANE
  name = G4_TISSUE-PROPANE
  specific = 4
FEATURE [App::DocumentObjectGroupPython] Ti_element003  label="Ti_element : 1"  # scripted group (container) (typed FeaturePython)
  n = 1
  ref = Ti_element
FEATURE [App::DocumentObjectGroupPython] O_element098  label="O_element : 052"  # scripted group (container) (typed FeaturePython)
  n = 2
  ref = O_element
FEATURE [App::DocumentObjectGroupPython] G4_TITANIUM_DIOXIDE  # scripted group (container) (typed FeaturePython)
  Dunit = g/cm3
  Dvalue = 4.26
  Group = -> [Ti_element003,O_element098]
  conduct = 2
  density = 1
  expand = 3
  formula = G4_TITANIUM_DIOXIDE
  name = G4_TITANIUM_DIOXIDE
  specific = 4
FEATURE [App::DocumentObjectGroupPython] C_element114  label="C_element : 061"  # scripted group (container) (typed FeaturePython)
  n = 7
  ref = C_element
FEATURE [App::DocumentObjectGroupPython] H_element104  label="H_element : 055"  # scripted group (container) (typed FeaturePython)
  n = 8
  ref = H_element
FEATURE [App::DocumentObjectGroupPython] G4_TOLUENE  # scripted group (container) (typed FeaturePython)
  Dunit = g/cm3
  Dvalue = 0.8669
  Group = -> [C_element114,H_element104]
  conduct = 2
  density = 1
  expand = 3
  formula = G4_TOLUENE
  name = G4_TOLUENE
  specific = 4
FEATURE [App::DocumentObjectGroupPython] C_element115  label="C_element : 062"  # scripted group (container) (typed FeaturePython)
  n = 2
  ref = C_element
FEATURE [App::DocumentObjectGroupPython] H_element105  label="H_element : 056"  # scripted group (container) (typed FeaturePython)
  n = 1
  ref = H_element
FEATURE [App::DocumentObjectGroupPython] Cl_element028  label="Cl_element : 014"  # scripted group (container) (typed FeaturePython)
  n = 3
  ref = Cl_element
FEATURE [App::DocumentObjectGroupPython] G4_TRICHLOROETHYLENE  # scripted group (container) (typed FeaturePython)
  Dunit = g/cm3
  Dvalue = 1.46
  Group = -> [C_element115,H_element105,Cl_element028]
  conduct = 2
  density = 1
  expand = 3
  formula = G4_TRICHLOROETHYLENE
  name = G4_TRICHLOROETHYLENE
  specific = 4
FEATURE [App::DocumentObjectGroupPython] C_element116  label="C_element : 063"  # scripted group (container) (typed FeaturePython)
  n = 6
  ref = C_element
FEATURE [App::DocumentObjectGroupPython] H_element106  label="H_element : 15"  # scripted group (container) (typed FeaturePython)
  n = 15
  ref = H_element
FEATURE [App::DocumentObjectGroupPython] O_element099  label="O_element : 053"  # scripted group (container) (typed FeaturePython)
  n = 4
  ref = O_element
FEATURE [App::DocumentObjectGroupPython] P_element012  label="P_element : 1"  # scripted group (container) (typed FeaturePython)
  n = 1
  ref = P_element
FEATURE [App::DocumentObjectGroupPython] G4_TRIETHYL_PHOSPHATE  # scripted group (container) (typed FeaturePython)
  Dunit = g/cm3
  Dvalue = 1.07
  Group = -> [C_element116,H_element106,O_element099,P_element012]
  conduct = 2
  density = 1
  expand = 3
  formula = G4_TRIETHYL_PHOSPHATE
  name = G4_TRIETHYL_PHOSPHATE
  specific = 4
FEATURE [App::DocumentObjectGroupPython] W_element003  label="W_element : 003"  # scripted group (container) (typed FeaturePython)
  n = 1
  ref = W_element
FEATURE [App::DocumentObjectGroupPython] F_element017  label="F_element : 6"  # scripted group (container) (typed FeaturePython)
  n = 6
  ref = F_element
FEATURE [App::DocumentObjectGroupPython] G4_TUNGSTEN_HEXAFLUORIDE  # scripted group (container) (typed FeaturePython)
  Dunit = g/cm3
  Dvalue = 2.4
  Group = -> [W_element003,F_element017]
  conduct = 2
  density = 1
  expand = 3
  formula = G4_TUNGSTEN_HEXAFLUORIDE
  name = G4_TUNGSTEN_HEXAFLUORIDE
  specific = 4
FEATURE [App::DocumentObjectGroupPython] U_element001  label="U_element : 1"  # scripted group (container) (typed FeaturePython)
  n = 1
  ref = U_element
FEATURE [App::DocumentObjectGroupPython] C_element117  label="C_element : 064"  # scripted group (container) (typed FeaturePython)
  n = 2
  ref = C_element
FEATURE [App::DocumentObjectGroupPython] G4_URANIUM_DICARBIDE  # scripted group (container) (typed FeaturePython)
  Dunit = g/cm3
  Dvalue = 11.28
  Group = -> [U_element001,C_element117]
  conduct = 2
  density = 1
  expand = 3
  formula = G4_URANIUM_DICARBIDE
  name = G4_URANIUM_DICARBIDE
  specific = 4
FEATURE [App::DocumentObjectGroupPython] U_element002  label="U_element : 002"  # scripted group (container) (typed FeaturePython)
  n = 1
  ref = U_element
FEATURE [App::DocumentObjectGroupPython] C_element118  label="C_element : 065"  # scripted group (container) (typed FeaturePython)
  n = 1
  ref = C_element
FEATURE [App::DocumentObjectGroupPython] G4_URANIUM_MONOCARBIDE  # scripted group (container) (typed FeaturePython)
  Dunit = g/cm3
  Dvalue = 13.63
  Group = -> [U_element002,C_element118]
  conduct = 2
  density = 1
  expand = 3
  formula = G4_URANIUM_MONOCARBIDE
  name = G4_URANIUM_MONOCARBIDE
  specific = 4
FEATURE [App::DocumentObjectGroupPython] U_element003  label="U_element : 003"  # scripted group (container) (typed FeaturePython)
  n = 1
  ref = U_element
FEATURE [App::DocumentObjectGroupPython] O_element100  label="O_element : 054"  # scripted group (container) (typed FeaturePython)
  n = 2
  ref = O_element
FEATURE [App::DocumentObjectGroupPython] G4_URANIUM_OXIDE  # scripted group (container) (typed FeaturePython)
  Dunit = g/cm3
  Dvalue = 10.96
  Group = -> [U_element003,O_element100]
  conduct = 2
  density = 1
  expand = 3
  formula = G4_URANIUM_OXIDE
  name = G4_URANIUM_OXIDE
  specific = 4
FEATURE [App::DocumentObjectGroupPython] C_element119  label="C_element : 066"  # scripted group (container) (typed FeaturePython)
  n = 1
  ref = C_element
FEATURE [App::DocumentObjectGroupPython] H_element107  label="H_element : 057"  # scripted group (container) (typed FeaturePython)
  n = 4
  ref = H_element
FEATURE [App::DocumentObjectGroupPython] N_element046  label="N_element : 019"  # scripted group (container) (typed FeaturePython)
  n = 2
  ref = N_element
FEATURE [App::DocumentObjectGroupPython] O_element101  label="O_element : 055"  # scripted group (container) (typed FeaturePython)
  n = 1
  ref = O_element
FEATURE [App::DocumentObjectGroupPython] G4_UREA  # scripted group (container) (typed FeaturePython)
  Dunit = g/cm3
  Dvalue = 1.323
  Group = -> [C_element119,H_element107,N_element046,O_element101]
  conduct = 2
  density = 1
  expand = 3
  formula = G4_UREA
  name = G4_UREA
  specific = 4
FEATURE [App::DocumentObjectGroupPython] C_element120  label="C_element : 067"  # scripted group (container) (typed FeaturePython)
  n = 5
  ref = C_element
FEATURE [App::DocumentObjectGroupPython] H_element108  label="H_element : 058"  # scripted group (container) (typed FeaturePython)
  n = 11
  ref = H_element
FEATURE [App::DocumentObjectGroupPython] N_element047  label="N_element : 020"  # scripted group (container) (typed FeaturePython)
  n = 1
  ref = N_element
FEATURE [App::DocumentObjectGroupPython] O_element102  label="O_element : 056"  # scripted group (container) (typed FeaturePython)
  n = 2
  ref = O_element
FEATURE [App::DocumentObjectGroupPython] G4_VALINE  # scripted group (container) (typed FeaturePython)
  Dunit = g/cm3
  Dvalue = 1.23
  Group = -> [C_element120,H_element108,N_element047,O_element102]
  conduct = 2
  density = 1
  expand = 3
  formula = G4_VALINE
  name = G4_VALINE
  specific = 4
FEATURE [App::DocumentObjectGroupPython] H_element109  label="H_element : 0.009"  # scripted group (container) (typed FeaturePython)
  n = 0.009417
FEATURE [App::DocumentObjectGroupPython] C_element121  label="C_element : 0.281"  # scripted group (container) (typed FeaturePython)
  n = 0.280555
FEATURE [App::DocumentObjectGroupPython] F_element018  label="F_element : 0.710"  # scripted group (container) (typed FeaturePython)
  n = 0.710028
FEATURE [App::DocumentObjectGroupPython] G4_VITON  # scripted group (container) (typed FeaturePython)
  Dunit = g/cm3
  Dvalue = 1.8
  Group = -> [H_element109,C_element121,F_element018]
  conduct = 2
  density = 1
  expand = 3
  formula = G4_VITON
  name = G4_VITON
  specific = 4
FEATURE [App::DocumentObjectGroupPython] H_element110  label="H_element : 059"  # scripted group (container) (typed FeaturePython)
  n = 2
  ref = H_element
FEATURE [App::DocumentObjectGroupPython] O_element103  label="O_element : 057"  # scripted group (container) (typed FeaturePython)
  n = 1
  ref = O_element
FEATURE [App::DocumentObjectGroupPython] G4_WATER  # scripted group (container) (typed FeaturePython)
  Dunit = g/cm3
  Dvalue = 1
  Group = -> [H_element110,O_element103]
  conduct = 2
  density = 1
  expand = 3
  formula = G4_WATER
  name = G4_WATER
  specific = 4
FEATURE [App::DocumentObjectGroupPython] H_element111  label="H_element : 060"  # scripted group (container) (typed FeaturePython)
  n = 2
  ref = H_element
FEATURE [App::DocumentObjectGroupPython] O_element104  label="O_element : 058"  # scripted group (container) (typed FeaturePython)
  n = 1
  ref = O_element
FEATURE [App::DocumentObjectGroupPython] G4_WATER_VAPOR  # scripted group (container) (typed FeaturePython)
  Dunit = g/cm3
  Dvalue = 0.000756182
  Group = -> [H_element111,O_element104]
  conduct = 2
  density = 1
  expand = 3
  formula = G4_WATER_VAPOR
  name = G4_WATER_VAPOR
  specific = 4
FEATURE [App::DocumentObjectGroupPython] C_element122  label="C_element : 068"  # scripted group (container) (typed FeaturePython)
  n = 8
  ref = C_element
FEATURE [App::DocumentObjectGroupPython] H_element112  label="H_element : 061"  # scripted group (container) (typed FeaturePython)
  n = 10
  ref = H_element
FEATURE [App::DocumentObjectGroupPython] G4_XYLENE  # scripted group (container) (typed FeaturePython)
  Dunit = g/cm3
  Dvalue = 0.87
  Group = -> [C_element122,H_element112]
  conduct = 2
  density = 1
  expand = 3
  formula = G4_XYLENE
  name = G4_XYLENE
  specific = 4
FEATURE [App::DocumentObjectGroupPython] C_element123  label="C_element : 069"  # scripted group (container) (typed FeaturePython)
  n = 1
  ref = C_element
FEATURE [App::DocumentObjectGroupPython] G4_GRAPHITE  # scripted group (container) (typed FeaturePython)
  Dunit = g/cm3
  Dvalue = 2.21
  Group = -> [C_element123]
  conduct = 2
  density = 1
  expand = 3
  formula = G4_GRAPHITE
  name = G4_GRAPHITE
  specific = 4
FEATURE [App::DocumentObjectGroupPython] NIST  # scripted group (container) (typed FeaturePython)
  Group = -> [G4_A_150_TISSUE,G4_ACETONE,G4_ACETYLENE,G4_ADENINE,G4_ADIPOSE_TISSUE_ICRP,G4_AIR,G4_ALANINE,G4_ALUMINUM_OXIDE,G4_AMBER,G4_AMMONIA,G4_ANILINE,G4_ANTHRACENE,G4_B_100_BONE,G4_BAKELITE,G4_BARIUM_FLUORIDE,G4_BARIUM_SULFATE,G4_BENZENE,G4_BERYLLIUM_OXIDE,G4_BGO,G4_BLOOD_ICRP,G4_BONE_COMPACT_ICRU,G4_BONE_CORTICAL_ICRP,G4_BORON_CARBIDE,G4_BORON_OXIDE,G4_BRAIN_ICRP,G4_BUTANE,G4_N_BUTYL_ALCOHOL,G4_C_552,+152 more]
FEATURE [App::DocumentObjectGroupPython] H_element113  label="H_element : 062"  # scripted group (container) (typed FeaturePython)
  n = 1
  ref = H_element
FEATURE [App::DocumentObjectGroupPython] G4_H  # scripted group (container) (typed FeaturePython)
  Dunit = g/cm3
  Dvalue = 8.3748e-05
  Group = -> [H_element113]
  conduct = 2
  density = 1
  expand = 3
  formula = H
  name = G4_H
  specific = 4
FEATURE [App::DocumentObjectGroupPython] He_element001  label="He_element : 1"  # scripted group (container) (typed FeaturePython)
  n = 1
  ref = He_element
FEATURE [App::DocumentObjectGroupPython] G4_He  # scripted group (container) (typed FeaturePython)
  Dunit = g/cm3
  Dvalue = 0.000166322
  Group = -> [He_element001]
  conduct = 2
  density = 1
  expand = 3
  formula = He
  name = G4_He
  specific = 4
FEATURE [App::DocumentObjectGroupPython] Li_element008  label="Li_element : 008"  # scripted group (container) (typed FeaturePython)
  n = 1
  ref = Li_element
FEATURE [App::DocumentObjectGroupPython] G4_Li  # scripted group (container) (typed FeaturePython)
  Dunit = g/cm3
  Dvalue = 0.534
  Group = -> [Li_element008]
  conduct = 2
  density = 1
  expand = 3
  formula = Li
  name = G4_Li
  specific = 4
FEATURE [App::DocumentObjectGroupPython] Be_element002  label="Be_element : 002"  # scripted group (container) (typed FeaturePython)
  n = 1
  ref = Be_element
FEATURE [App::DocumentObjectGroupPython] G4_Be  # scripted group (container) (typed FeaturePython)
  Dunit = g/cm3
  Dvalue = 1.848
  Group = -> [Be_element002]
  conduct = 2
  density = 1
  expand = 3
  formula = Be
  name = G4_Be
  specific = 4
FEATURE [App::DocumentObjectGroupPython] B_element007  label="B_element : 007"  # scripted group (container) (typed FeaturePython)
  n = 1
  ref = B_element
FEATURE [App::DocumentObjectGroupPython] G4_B  # scripted group (container) (typed FeaturePython)
  Dunit = g/cm3
  Dvalue = 2.37
  Group = -> [B_element007]
  conduct = 2
  density = 1
  expand = 3
  formula = B
  name = G4_B
  specific = 4
FEATURE [App::DocumentObjectGroupPython] C_element124  label="C_element : 070"  # scripted group (container) (typed FeaturePython)
  n = 1
  ref = C_element
FEATURE [App::DocumentObjectGroupPython] G4_C  # scripted group (container) (typed FeaturePython)
  Dunit = g/cm3
  Dvalue = 2
  Group = -> [C_element124]
  conduct = 2
  density = 1
  expand = 3
  formula = C
  name = G4_C
  specific = 4
FEATURE [App::DocumentObjectGroupPython] N_element048  label="N_element : 021"  # scripted group (container) (typed FeaturePython)
  n = 1
  ref = N_element
FEATURE [App::DocumentObjectGroupPython] G4_N  # scripted group (container) (typed FeaturePython)
  Dunit = g/cm3
  Dvalue = 0.0011652
  Group = -> [N_element048]
  conduct = 2
  density = 1
  expand = 3
  formula = N
  name = G4_N
  specific = 4
FEATURE [App::DocumentObjectGroupPython] O_element105  label="O_element : 059"  # scripted group (container) (typed FeaturePython)
  n = 1
  ref = O_element
FEATURE [App::DocumentObjectGroupPython] G4_O  # scripted group (container) (typed FeaturePython)
  Dunit = g/cm3
  Dvalue = 0.00133151
  Group = -> [O_element105]
  conduct = 2
  density = 1
  expand = 3
  formula = O
  name = G4_O
  specific = 4
FEATURE [App::DocumentObjectGroupPython] F_element019  label="F_element : 008"  # scripted group (container) (typed FeaturePython)
  n = 1
  ref = F_element
FEATURE [App::DocumentObjectGroupPython] G4_F  # scripted group (container) (typed FeaturePython)
  Dunit = g/cm3
  Dvalue = 0.00158029
  Group = -> [F_element019]
  conduct = 2
  density = 1
  expand = 3
  formula = F
  name = G4_F
  specific = 4
FEATURE [App::DocumentObjectGroupPython] Ne_element001  label="Ne_element : 1"  # scripted group (container) (typed FeaturePython)
  n = 1
  ref = Ne_element
FEATURE [App::DocumentObjectGroupPython] G4_Ne  # scripted group (container) (typed FeaturePython)
  Dunit = g/cm3
  Dvalue = 0.000838505
  Group = -> [Ne_element001]
  conduct = 2
  density = 1
  expand = 3
  formula = Ne
  name = G4_Ne
  specific = 4
FEATURE [App::DocumentObjectGroupPython] Na_element020  label="Na_element : 005"  # scripted group (container) (typed FeaturePython)
  n = 1
  ref = Na_element
FEATURE [App::DocumentObjectGroupPython] G4_Na  # scripted group (container) (typed FeaturePython)
  Dunit = g/cm3
  Dvalue = 0.971
  Group = -> [Na_element020]
  conduct = 2
  density = 1
  expand = 3
  formula = Na
  name = G4_Na
  specific = 4
FEATURE [App::DocumentObjectGroupPython] Mg_element011  label="Mg_element : 005"  # scripted group (container) (typed FeaturePython)
  n = 1
  ref = Mg_element
FEATURE [App::DocumentObjectGroupPython] G4_Mg  # scripted group (container) (typed FeaturePython)
  Dunit = g/cm3
  Dvalue = 1.74
  Group = -> [Mg_element011]
  conduct = 2
  density = 1
  expand = 3
  formula = Mg
  name = G4_Mg
  specific = 4
FEATURE [App::DocumentObjectGroupPython] Al_element004  label="Al_element : 1"  # scripted group (container) (typed FeaturePython)
  n = 1
  ref = Al_element
FEATURE [App::DocumentObjectGroupPython] G4_Al  # scripted group (container) (typed FeaturePython)
  Dunit = g/cm3
  Dvalue = 2.699
  Group = -> [Al_element004]
  conduct = 2
  density = 1
  expand = 3
  formula = Al
  name = G4_Al
  specific = 4
FEATURE [App::DocumentObjectGroupPython] Si_element007  label="Si_element : 002"  # scripted group (container) (typed FeaturePython)
  n = 1
  ref = Si_element
FEATURE [App::DocumentObjectGroupPython] G4_Si  # scripted group (container) (typed FeaturePython)
  Dunit = g/cm3
  Dvalue = 2.33
  Group = -> [Si_element007]
  conduct = 2
  density = 1
  expand = 3
  formula = Si
  name = G4_Si
  specific = 4
FEATURE [App::DocumentObjectGroupPython] P_element013  label="P_element : 002"  # scripted group (container) (typed FeaturePython)
  n = 1
  ref = P_element
FEATURE [App::DocumentObjectGroupPython] G4_P  # scripted group (container) (typed FeaturePython)
  Dunit = g/cm3
  Dvalue = 2.2
  Group = -> [P_element013]
  conduct = 2
  density = 1
  expand = 3
  formula = P
  name = G4_P
  specific = 4
FEATURE [App::DocumentObjectGroupPython] S_element023  label="S_element : 007"  # scripted group (container) (typed FeaturePython)
  n = 1
  ref = S_element
FEATURE [App::DocumentObjectGroupPython] G4_S  # scripted group (container) (typed FeaturePython)
  Dunit = g/cm3
  Dvalue = 2
  Group = -> [S_element023]
  conduct = 2
  density = 1
  expand = 3
  formula = S
  name = G4_S
  specific = 4
FEATURE [App::DocumentObjectGroupPython] Cl_element029  label="Cl_element : 015"  # scripted group (container) (typed FeaturePython)
  n = 1
  ref = Cl_element
FEATURE [App::DocumentObjectGroupPython] G4_Cl  # scripted group (container) (typed FeaturePython)
  Dunit = g/cm3
  Dvalue = 0.00299473
  Group = -> [Cl_element029]
  conduct = 2
  density = 1
  expand = 3
  formula = Cl
  name = G4_Cl
  specific = 4
FEATURE [App::DocumentObjectGroupPython] Ar_element002  label="Ar_element : 1"  # scripted group (container) (typed FeaturePython)
  n = 1
  ref = Ar_element
FEATURE [App::DocumentObjectGroupPython] G4_Ar  # scripted group (container) (typed FeaturePython)
  Dunit = g/cm3
  Dvalue = 0.00166201
  Group = -> [Ar_element002]
  conduct = 2
  density = 1
  expand = 3
  formula = Ar
  name = G4_Ar
  specific = 4
FEATURE [App::DocumentObjectGroupPython] K_element013  label="K_element : 003"  # scripted group (container) (typed FeaturePython)
  n = 1
  ref = K_element
FEATURE [App::DocumentObjectGroupPython] G4_K  # scripted group (container) (typed FeaturePython)
  Dunit = g/cm3
  Dvalue = 0.862
  Group = -> [K_element013]
  conduct = 2
  density = 1
  expand = 3
  formula = K
  name = G4_K
  specific = 4
FEATURE [App::DocumentObjectGroupPython] Ca_element014  label="Ca_element : 007"  # scripted group (container) (typed FeaturePython)
  n = 1
  ref = Ca_element
FEATURE [App::DocumentObjectGroupPython] G4_Ca  # scripted group (container) (typed FeaturePython)
  Dunit = g/cm3
  Dvalue = 1.55
  Group = -> [Ca_element014]
  conduct = 2
  density = 1
  expand = 3
  formula = Ca
  name = G4_Ca
  specific = 4
FEATURE [App::DocumentObjectGroupPython] Sc_element001  label="Sc_element : 1"  # scripted group (container) (typed FeaturePython)
  n = 1
  ref = Sc_element
FEATURE [App::DocumentObjectGroupPython] G4_Sc  # scripted group (container) (typed FeaturePython)
  Dunit = g/cm3
  Dvalue = 2.989
  Group = -> [Sc_element001]
  conduct = 2
  density = 1
  expand = 3
  formula = Sc
  name = G4_Sc
  specific = 4
FEATURE [App::DocumentObjectGroupPython] Ti_element004  label="Ti_element : 002"  # scripted group (container) (typed FeaturePython)
  n = 1
  ref = Ti_element
FEATURE [App::DocumentObjectGroupPython] G4_Ti  # scripted group (container) (typed FeaturePython)
  Dunit = g/cm3
  Dvalue = 4.54
  Group = -> [Ti_element004]
  conduct = 2
  density = 1
  expand = 3
  formula = Ti
  name = G4_Ti
  specific = 4
FEATURE [App::DocumentObjectGroupPython] V_element001  label="V_element : 1"  # scripted group (container) (typed FeaturePython)
  n = 1
  ref = V_element
FEATURE [App::DocumentObjectGroupPython] G4_V  # scripted group (container) (typed FeaturePython)
  Dunit = g/cm3
  Dvalue = 6.11
  Group = -> [V_element001]
  conduct = 2
  density = 1
  expand = 3
  formula = V
  name = G4_V
  specific = 4
FEATURE [App::DocumentObjectGroupPython] Cr_element001  label="Cr_element : 1"  # scripted group (container) (typed FeaturePython)
  n = 1
  ref = Cr_element
FEATURE [App::DocumentObjectGroupPython] G4_Cr  # scripted group (container) (typed FeaturePython)
  Dunit = g/cm3
  Dvalue = 7.18
  Group = -> [Cr_element001]
  conduct = 2
  density = 1
  expand = 3
  formula = Cr
  name = G4_Cr
  specific = 4
FEATURE [App::DocumentObjectGroupPython] Mn_element001  label="Mn_element : 1"  # scripted group (container) (typed FeaturePython)
  n = 1
  ref = Mn_element
FEATURE [App::DocumentObjectGroupPython] G4_Mn  # scripted group (container) (typed FeaturePython)
  Dunit = g/cm3
  Dvalue = 7.44
  Group = -> [Mn_element001]
  conduct = 2
  density = 1
  expand = 3
  formula = Mn
  name = G4_Mn
  specific = 4
FEATURE [App::DocumentObjectGroupPython] Fe_element007  label="Fe_element : 004"  # scripted group (container) (typed FeaturePython)
  n = 1
  ref = Fe_element
FEATURE [App::DocumentObjectGroupPython] G4_Fe  # scripted group (container) (typed FeaturePython)
  Dunit = g/cm3
  Dvalue = 7.874
  Group = -> [Fe_element007]
  conduct = 2
  density = 1
  expand = 3
  formula = Fe
  name = G4_Fe
  specific = 4
FEATURE [App::DocumentObjectGroupPython] Co_element001  label="Co_element : 1"  # scripted group (container) (typed FeaturePython)
  n = 1
  ref = Co_element
FEATURE [App::DocumentObjectGroupPython] G4_Co  # scripted group (container) (typed FeaturePython)
  Dunit = g/cm3
  Dvalue = 8.9
  Group = -> [Co_element001]
  conduct = 2
  density = 1
  expand = 3
  formula = Co
  name = G4_Co
  specific = 4
FEATURE [App::DocumentObjectGroupPython] Ni_element001  label="Ni_element : 1"  # scripted group (container) (typed FeaturePython)
  n = 1
  ref = Ni_element
FEATURE [App::DocumentObjectGroupPython] G4_Ni  # scripted group (container) (typed FeaturePython)
  Dunit = g/cm3
  Dvalue = 8.902
  Group = -> [Ni_element001]
  conduct = 2
  density = 1
  expand = 3
  formula = Ni
  name = G4_Ni
  specific = 4
FEATURE [App::DocumentObjectGroupPython] Cu_element001  label="Cu_element : 1"  # scripted group (container) (typed FeaturePython)
  n = 1
  ref = Cu_element
FEATURE [App::DocumentObjectGroupPython] G4_Cu  # scripted group (container) (typed FeaturePython)
  Dunit = g/cm3
  Dvalue = 8.96
  Group = -> [Cu_element001]
  conduct = 2
  density = 1
  expand = 3
  formula = Cu
  name = G4_Cu
  specific = 4
FEATURE [App::DocumentObjectGroupPython] Zn_element001  label="Zn_element : 1"  # scripted group (container) (typed FeaturePython)
  n = 1
  ref = Zn_element
FEATURE [App::DocumentObjectGroupPython] G4_Zn  # scripted group (container) (typed FeaturePython)
  Dunit = g/cm3
  Dvalue = 7.133
  Group = -> [Zn_element001]
  conduct = 2
  density = 1
  expand = 3
  formula = Zn
  name = G4_Zn
  specific = 4
FEATURE [App::DocumentObjectGroupPython] Ga_element002  label="Ga_element : 002"  # scripted group (container) (typed FeaturePython)
  n = 1
  ref = Ga_element
FEATURE [App::DocumentObjectGroupPython] G4_Ga  # scripted group (container) (typed FeaturePython)
  Dunit = g/cm3
  Dvalue = 5.904
  Group = -> [Ga_element002]
  conduct = 2
  density = 1
  expand = 3
  formula = Ga
  name = G4_Ga
  specific = 4
FEATURE [App::DocumentObjectGroupPython] Ge_element002  label="Ge_element : 1"  # scripted group (container) (typed FeaturePython)
  n = 1
  ref = Ge_element
FEATURE [App::DocumentObjectGroupPython] G4_Ge  # scripted group (container) (typed FeaturePython)
  Dunit = g/cm3
  Dvalue = 5.323
  Group = -> [Ge_element002]
  conduct = 2
  density = 1
  expand = 3
  formula = Ge
  name = G4_Ge
  specific = 4
FEATURE [App::DocumentObjectGroupPython] As_element003  label="As_element : 002"  # scripted group (container) (typed FeaturePython)
  n = 1
  ref = As_element
FEATURE [App::DocumentObjectGroupPython] G4_As  # scripted group (container) (typed FeaturePython)
  Dunit = g/cm3
  Dvalue = 5.73
  Group = -> [As_element003]
  conduct = 2
  density = 1
  expand = 3
  formula = As
  name = G4_As
  specific = 4
FEATURE [App::DocumentObjectGroupPython] Se_element001  label="Se_element : 1"  # scripted group (container) (typed FeaturePython)
  n = 1
  ref = Se_element
FEATURE [App::DocumentObjectGroupPython] G4_Se  # scripted group (container) (typed FeaturePython)
  Dunit = g/cm3
  Dvalue = 4.5
  Group = -> [Se_element001]
  conduct = 2
  density = 1
  expand = 3
  formula = Se
  name = G4_Se
  specific = 4
FEATURE [App::DocumentObjectGroupPython] Br_element007  label="Br_element : 004"  # scripted group (container) (typed FeaturePython)
  n = 1
  ref = Br_element
FEATURE [App::DocumentObjectGroupPython] G4_Br  # scripted group (container) (typed FeaturePython)
  Dunit = g/cm3
  Dvalue = 0.0070721
  Group = -> [Br_element007]
  conduct = 2
  density = 1
  expand = 3
  formula = Br
  name = G4_Br
  specific = 4
FEATURE [App::DocumentObjectGroupPython] Kr_element001  label="Kr_element : 1"  # scripted group (container) (typed FeaturePython)
  n = 1
  ref = Kr_element
FEATURE [App::DocumentObjectGroupPython] G4_Kr  # scripted group (container) (typed FeaturePython)
  Dunit = g/cm3
  Dvalue = 0.00347832
  Group = -> [Kr_element001]
  conduct = 2
  density = 1
  expand = 3
  formula = Kr
  name = G4_Kr
  specific = 4
FEATURE [App::DocumentObjectGroupPython] Rb_element001  label="Rb_element : 1"  # scripted group (container) (typed FeaturePython)
  n = 1
  ref = Rb_element
FEATURE [App::DocumentObjectGroupPython] G4_Rb  # scripted group (container) (typed FeaturePython)
  Dunit = g/cm3
  Dvalue = 1.532
  Group = -> [Rb_element001]
  conduct = 2
  density = 1
  expand = 3
  formula = Rb
  name = G4_Rb
  specific = 4
FEATURE [App::DocumentObjectGroupPython] Sr_element001  label="Sr_element : 1"  # scripted group (container) (typed FeaturePython)
  n = 1
  ref = Sr_element
FEATURE [App::DocumentObjectGroupPython] G4_Sr  # scripted group (container) (typed FeaturePython)
  Dunit = g/cm3
  Dvalue = 2.54
  Group = -> [Sr_element001]
  conduct = 2
  density = 1
  expand = 3
  formula = Sr
  name = G4_Sr
  specific = 4
FEATURE [App::DocumentObjectGroupPython] Y_element001  label="Y_element : 1"  # scripted group (container) (typed FeaturePython)
  n = 1
  ref = Y_element
FEATURE [App::DocumentObjectGroupPython] G4_Y  # scripted group (container) (typed FeaturePython)
  Dunit = g/cm3
  Dvalue = 4.469
  Group = -> [Y_element001]
  conduct = 2
  density = 1
  expand = 3
  formula = Y
  name = G4_Y
  specific = 4
FEATURE [App::DocumentObjectGroupPython] Zr_element001  label="Zr_element : 1"  # scripted group (container) (typed FeaturePython)
  n = 1
  ref = Zr_element
FEATURE [App::DocumentObjectGroupPython] G4_Zr  # scripted group (container) (typed FeaturePython)
  Dunit = g/cm3
  Dvalue = 6.506
  Group = -> [Zr_element001]
  conduct = 2
  density = 1
  expand = 3
  formula = Zr
  name = G4_Zr
  specific = 4
FEATURE [App::DocumentObjectGroupPython] Nb_element001  label="Nb_element : 1"  # scripted group (container) (typed FeaturePython)
  n = 1
  ref = Nb_element
FEATURE [App::DocumentObjectGroupPython] G4_Nb  # scripted group (container) (typed FeaturePython)
  Dunit = g/cm3
  Dvalue = 8.57
  Group = -> [Nb_element001]
  conduct = 2
  density = 1
  expand = 3
  formula = Nb
  name = G4_Nb
  specific = 4
FEATURE [App::DocumentObjectGroupPython] Mo_element001  label="Mo_element : 1"  # scripted group (container) (typed FeaturePython)
  n = 1
  ref = Mo_element
FEATURE [App::DocumentObjectGroupPython] G4_Mo  # scripted group (container) (typed FeaturePython)
  Dunit = g/cm3
  Dvalue = 10.22
  Group = -> [Mo_element001]
  conduct = 2
  density = 1
  expand = 3
  formula = Mo
  name = G4_Mo
  specific = 4
FEATURE [App::DocumentObjectGroupPython] Tc_element001  label="Tc_element : 1"  # scripted group (container) (typed FeaturePython)
  n = 1
  ref = Tc_element
FEATURE [App::DocumentObjectGroupPython] G4_Tc  # scripted group (container) (typed FeaturePython)
  Dunit = g/cm3
  Dvalue = 11.5
  Group = -> [Tc_element001]
  conduct = 2
  density = 1
  expand = 3
  formula = Tc
  name = G4_Tc
  specific = 4
FEATURE [App::DocumentObjectGroupPython] Ru_element001  label="Ru_element : 1"  # scripted group (container) (typed FeaturePython)
  n = 1
  ref = Ru_element
FEATURE [App::DocumentObjectGroupPython] G4_Ru  # scripted group (container) (typed FeaturePython)
  Dunit = g/cm3
  Dvalue = 12.41
  Group = -> [Ru_element001]
  conduct = 2
  density = 1
  expand = 3
  formula = Ru
  name = G4_Ru
  specific = 4
FEATURE [App::DocumentObjectGroupPython] Rh_element001  label="Rh_element : 1"  # scripted group (container) (typed FeaturePython)
  n = 1
  ref = Rh_element
FEATURE [App::DocumentObjectGroupPython] G4_Rh  # scripted group (container) (typed FeaturePython)
  Dunit = g/cm3
  Dvalue = 12.41
  Group = -> [Rh_element001]
  conduct = 2
  density = 1
  expand = 3
  formula = Rh
  name = G4_Rh
  specific = 4
FEATURE [App::DocumentObjectGroupPython] Pd_element001  label="Pd_element : 1"  # scripted group (container) (typed FeaturePython)
  n = 1
  ref = Pd_element
FEATURE [App::DocumentObjectGroupPython] G4_Pd  # scripted group (container) (typed FeaturePython)
  Dunit = g/cm3
  Dvalue = 12.02
  Group = -> [Pd_element001]
  conduct = 2
  density = 1
  expand = 3
  formula = Pd
  name = G4_Pd
  specific = 4
FEATURE [App::DocumentObjectGroupPython] Ag_element006  label="Ag_element : 004"  # scripted group (container) (typed FeaturePython)
  n = 1
  ref = Ag_element
FEATURE [App::DocumentObjectGroupPython] G4_Ag  # scripted group (container) (typed FeaturePython)
  Dunit = g/cm3
  Dvalue = 10.5
  Group = -> [Ag_element006]
  conduct = 2
  density = 1
  expand = 3
  formula = Ag
  name = G4_Ag
  specific = 4
FEATURE [App::DocumentObjectGroupPython] Cd_element003  label="Cd_element : 003"  # scripted group (container) (typed FeaturePython)
  n = 1
  ref = Cd_element
FEATURE [App::DocumentObjectGroupPython] G4_Cd  # scripted group (container) (typed FeaturePython)
  Dunit = g/cm3
  Dvalue = 8.65
  Group = -> [Cd_element003]
  conduct = 2
  density = 1
  expand = 3
  formula = Cd
  name = G4_Cd
  specific = 4
FEATURE [App::DocumentObjectGroupPython] In_element001  label="In_element : 1"  # scripted group (container) (typed FeaturePython)
  n = 1
  ref = In_element
FEATURE [App::DocumentObjectGroupPython] G4_In  # scripted group (container) (typed FeaturePython)
  Dunit = g/cm3
  Dvalue = 7.31
  Group = -> [In_element001]
  conduct = 2
  density = 1
  expand = 3
  formula = In
  name = G4_In
  specific = 4
FEATURE [App::DocumentObjectGroupPython] Sn_element001  label="Sn_element : 1"  # scripted group (container) (typed FeaturePython)
  n = 1
  ref = Sn_element
FEATURE [App::DocumentObjectGroupPython] G4_Sn  # scripted group (container) (typed FeaturePython)
  Dunit = g/cm3
  Dvalue = 7.31
  Group = -> [Sn_element001]
  conduct = 2
  density = 1
  expand = 3
  formula = Sn
  name = G4_Sn
  specific = 4
FEATURE [App::DocumentObjectGroupPython] Sb_element001  label="Sb_element : 1"  # scripted group (container) (typed FeaturePython)
  n = 1
  ref = Sb_element
FEATURE [App::DocumentObjectGroupPython] G4_Sb  # scripted group (container) (typed FeaturePython)
  Dunit = g/cm3
  Dvalue = 6.691
  Group = -> [Sb_element001]
  conduct = 2
  density = 1
  expand = 3
  formula = Sb
  name = G4_Sb
  specific = 4
FEATURE [App::DocumentObjectGroupPython] Te_element002  label="Te_element : 002"  # scripted group (container) (typed FeaturePython)
  n = 1
  ref = Te_element
FEATURE [App::DocumentObjectGroupPython] G4_Te  # scripted group (container) (typed FeaturePython)
  Dunit = g/cm3
  Dvalue = 6.24
  Group = -> [Te_element002]
  conduct = 2
  density = 1
  expand = 3
  formula = Te
  name = G4_Te
  specific = 4
FEATURE [App::DocumentObjectGroupPython] I_element010  label="I_element : 006"  # scripted group (container) (typed FeaturePython)
  n = 1
  ref = I_element
FEATURE [App::DocumentObjectGroupPython] G4_I  # scripted group (container) (typed FeaturePython)
  Dunit = g/cm3
  Dvalue = 4.93
  Group = -> [I_element010]
  conduct = 2
  density = 1
  expand = 3
  formula = I
  name = G4_I
  specific = 4
FEATURE [App::DocumentObjectGroupPython] Xe_element001  label="Xe_element : 1"  # scripted group (container) (typed FeaturePython)
  n = 1
  ref = Xe_element
FEATURE [App::DocumentObjectGroupPython] G4_Xe  # scripted group (container) (typed FeaturePython)
  Dunit = g/cm3
  Dvalue = 0.00548536
  Group = -> [Xe_element001]
  conduct = 2
  density = 1
  expand = 3
  formula = Xe
  name = G4_Xe
  specific = 4
FEATURE [App::DocumentObjectGroupPython] Cs_element003  label="Cs_element : 003"  # scripted group (container) (typed FeaturePython)
  n = 1
  ref = Cs_element
FEATURE [App::DocumentObjectGroupPython] G4_Cs  # scripted group (container) (typed FeaturePython)
  Dunit = g/cm3
  Dvalue = 1.873
  Group = -> [Cs_element003]
  conduct = 2
  density = 1
  expand = 3
  formula = Cs
  name = G4_Cs
  specific = 4
FEATURE [App::DocumentObjectGroupPython] Ba_element003  label="Ba_element : 003"  # scripted group (container) (typed FeaturePython)
  n = 1
  ref = Ba_element
FEATURE [App::DocumentObjectGroupPython] G4_Ba  # scripted group (container) (typed FeaturePython)
  Dunit = g/cm3
  Dvalue = 3.5
  Group = -> [Ba_element003]
  conduct = 2
  density = 1
  expand = 3
  formula = Ba
  name = G4_Ba
  specific = 4
FEATURE [App::DocumentObjectGroupPython] La_element003  label="La_element : 003"  # scripted group (container) (typed FeaturePython)
  n = 1
  ref = La_element
FEATURE [App::DocumentObjectGroupPython] G4_La  # scripted group (container) (typed FeaturePython)
  Dunit = g/cm3
  Dvalue = 6.154
  Group = -> [La_element003]
  conduct = 2
  density = 1
  expand = 3
  formula = La
  name = G4_La
  specific = 4
FEATURE [App::DocumentObjectGroupPython] Ce_element002  label="Ce_element : 1"  # scripted group (container) (typed FeaturePython)
  n = 1
  ref = Ce_element
FEATURE [App::DocumentObjectGroupPython] G4_Ce  # scripted group (container) (typed FeaturePython)
  Dunit = g/cm3
  Dvalue = 6.657
  Group = -> [Ce_element002]
  conduct = 2
  density = 1
  expand = 3
  formula = Ce
  name = G4_Ce
  specific = 4
FEATURE [App::DocumentObjectGroupPython] Pr_element001  label="Pr_element : 1"  # scripted group (container) (typed FeaturePython)
  n = 1
  ref = Pr_element
FEATURE [App::DocumentObjectGroupPython] G4_Pr  # scripted group (container) (typed FeaturePython)
  Dunit = g/cm3
  Dvalue = 6.71
  Group = -> [Pr_element001]
  conduct = 2
  density = 1
  expand = 3
  formula = Pr
  name = G4_Pr
  specific = 4
FEATURE [App::DocumentObjectGroupPython] Nd_element001  label="Nd_element : 1"  # scripted group (container) (typed FeaturePython)
  n = 1
  ref = Nd_element
FEATURE [App::DocumentObjectGroupPython] G4_Nd  # scripted group (container) (typed FeaturePython)
  Dunit = g/cm3
  Dvalue = 6.9
  Group = -> [Nd_element001]
  conduct = 2
  density = 1
  expand = 3
  formula = Nd
  name = G4_Nd
  specific = 4
FEATURE [App::DocumentObjectGroupPython] Pm_element001  label="Pm_element : 1"  # scripted group (container) (typed FeaturePython)
  n = 1
  ref = Pm_element
FEATURE [App::DocumentObjectGroupPython] G4_Pm  # scripted group (container) (typed FeaturePython)
  Dunit = g/cm3
  Dvalue = 7.22
  Group = -> [Pm_element001]
  conduct = 2
  density = 1
  expand = 3
  formula = Pm
  name = G4_Pm
  specific = 4
FEATURE [App::DocumentObjectGroupPython] Sm_element001  label="Sm_element : 1"  # scripted group (container) (typed FeaturePython)
  n = 1
  ref = Sm_element
FEATURE [App::DocumentObjectGroupPython] G4_Sm  # scripted group (container) (typed FeaturePython)
  Dunit = g/cm3
  Dvalue = 7.46
  Group = -> [Sm_element001]
  conduct = 2
  density = 1
  expand = 3
  formula = Sm
  name = G4_Sm
  specific = 4
FEATURE [App::DocumentObjectGroupPython] Eu_element001  label="Eu_element : 1"  # scripted group (container) (typed FeaturePython)
  n = 1
  ref = Eu_element
FEATURE [App::DocumentObjectGroupPython] G4_Eu  # scripted group (container) (typed FeaturePython)
  Dunit = g/cm3
  Dvalue = 5.243
  Group = -> [Eu_element001]
  conduct = 2
  density = 1
  expand = 3
  formula = Eu
  name = G4_Eu
  specific = 4
FEATURE [App::DocumentObjectGroupPython] Gd_element002  label="Gd_element : 1"  # scripted group (container) (typed FeaturePython)
  n = 1
  ref = Gd_element
FEATURE [App::DocumentObjectGroupPython] G4_Gd  # scripted group (container) (typed FeaturePython)
  Dunit = g/cm3
  Dvalue = 7.9004
  Group = -> [Gd_element002]
  conduct = 2
  density = 1
  expand = 3
  formula = Gd
  name = G4_Gd
  specific = 4
FEATURE [App::DocumentObjectGroupPython] Tb_element001  label="Tb_element : 1"  # scripted group (container) (typed FeaturePython)
  n = 1
  ref = Tb_element
FEATURE [App::DocumentObjectGroupPython] G4_Tb  # scripted group (container) (typed FeaturePython)
  Dunit = g/cm3
  Dvalue = 8.229
  Group = -> [Tb_element001]
  conduct = 2
  density = 1
  expand = 3
  formula = Tb
  name = G4_Tb
  specific = 4
FEATURE [App::DocumentObjectGroupPython] Dy_element001  label="Dy_element : 1"  # scripted group (container) (typed FeaturePython)
  n = 1
  ref = Dy_element
FEATURE [App::DocumentObjectGroupPython] G4_Dy  # scripted group (container) (typed FeaturePython)
  Dunit = g/cm3
  Dvalue = 8.55
  Group = -> [Dy_element001]
  conduct = 2
  density = 1
  expand = 3
  formula = Dy
  name = G4_Dy
  specific = 4
FEATURE [App::DocumentObjectGroupPython] Ho_element001  label="Ho_element : 1"  # scripted group (container) (typed FeaturePython)
  n = 1
  ref = Ho_element
FEATURE [App::DocumentObjectGroupPython] G4_Ho  # scripted group (container) (typed FeaturePython)
  Dunit = g/cm3
  Dvalue = 8.795
  Group = -> [Ho_element001]
  conduct = 2
  density = 1
  expand = 3
  formula = Ho
  name = G4_Ho
  specific = 4
FEATURE [App::DocumentObjectGroupPython] Er_element001  label="Er_element : 1"  # scripted group (container) (typed FeaturePython)
  n = 1
  ref = Er_element
FEATURE [App::DocumentObjectGroupPython] G4_Er  # scripted group (container) (typed FeaturePython)
  Dunit = g/cm3
  Dvalue = 9.066
  Group = -> [Er_element001]
  conduct = 2
  density = 1
  expand = 3
  formula = Er
  name = G4_Er
  specific = 4
FEATURE [App::DocumentObjectGroupPython] Tm_element001  label="Tm_element : 1"  # scripted group (container) (typed FeaturePython)
  n = 1
  ref = Tm_element
FEATURE [App::DocumentObjectGroupPython] G4_Tm  # scripted group (container) (typed FeaturePython)
  Dunit = g/cm3
  Dvalue = 9.321
  Group = -> [Tm_element001]
  conduct = 2
  density = 1
  expand = 3
  formula = Tm
  name = G4_Tm
  specific = 4
FEATURE [App::DocumentObjectGroupPython] Yb_element001  label="Yb_element : 1"  # scripted group (container) (typed FeaturePython)
  n = 1
  ref = Yb_element
FEATURE [App::DocumentObjectGroupPython] G4_Yb  # scripted group (container) (typed FeaturePython)
  Dunit = g/cm3
  Dvalue = 6.73
  Group = -> [Yb_element001]
  conduct = 2
  density = 1
  expand = 3
  formula = Yb
  name = G4_Yb
  specific = 4
FEATURE [App::DocumentObjectGroupPython] Lu_element001  label="Lu_element : 1"  # scripted group (container) (typed FeaturePython)
  n = 1
  ref = Lu_element
FEATURE [App::DocumentObjectGroupPython] G4_Lu  # scripted group (container) (typed FeaturePython)
  Dunit = g/cm3
  Dvalue = 9.84
  Group = -> [Lu_element001]
  conduct = 2
  density = 1
  expand = 3
  formula = Lu
  name = G4_Lu
  specific = 4
FEATURE [App::DocumentObjectGroupPython] Hf_element001  label="Hf_element : 1"  # scripted group (container) (typed FeaturePython)
  n = 1
  ref = Hf_element
FEATURE [App::DocumentObjectGroupPython] G4_Hf  # scripted group (container) (typed FeaturePython)
  Dunit = g/cm3
  Dvalue = 13.31
  Group = -> [Hf_element001]
  conduct = 2
  density = 1
  expand = 3
  formula = Hf
  name = G4_Hf
  specific = 4
FEATURE [App::DocumentObjectGroupPython] Ta_element001  label="Ta_element : 1"  # scripted group (container) (typed FeaturePython)
  n = 1
  ref = Ta_element
FEATURE [App::DocumentObjectGroupPython] G4_Ta  # scripted group (container) (typed FeaturePython)
  Dunit = g/cm3
  Dvalue = 16.654
  Group = -> [Ta_element001]
  conduct = 2
  density = 1
  expand = 3
  formula = Ta
  name = G4_Ta
  specific = 4
FEATURE [App::DocumentObjectGroupPython] W_element004  label="W_element : 004"  # scripted group (container) (typed FeaturePython)
  n = 1
  ref = W_element
FEATURE [App::DocumentObjectGroupPython] G4_W  # scripted group (container) (typed FeaturePython)
  Dunit = g/cm3
  Dvalue = 19.3
  Group = -> [W_element004]
  conduct = 2
  density = 1
  expand = 3
  formula = W
  name = G4_W
  specific = 4
FEATURE [App::DocumentObjectGroupPython] Re_element001  label="Re_element : 1"  # scripted group (container) (typed FeaturePython)
  n = 1
  ref = Re_element
FEATURE [App::DocumentObjectGroupPython] G4_Re  # scripted group (container) (typed FeaturePython)
  Dunit = g/cm3
  Dvalue = 21.02
  Group = -> [Re_element001]
  conduct = 2
  density = 1
  expand = 3
  formula = Re
  name = G4_Re
  specific = 4
FEATURE [App::DocumentObjectGroupPython] Os_element001  label="Os_element : 1"  # scripted group (container) (typed FeaturePython)
  n = 1
  ref = Os_element
FEATURE [App::DocumentObjectGroupPython] G4_Os  # scripted group (container) (typed FeaturePython)
  Dunit = g/cm3
  Dvalue = 22.57
  Group = -> [Os_element001]
  conduct = 2
  density = 1
  expand = 3
  formula = Os
  name = G4_Os
  specific = 4
FEATURE [App::DocumentObjectGroupPython] Ir_element001  label="Ir_element : 1"  # scripted group (container) (typed FeaturePython)
  n = 1
  ref = Ir_element
FEATURE [App::DocumentObjectGroupPython] G4_Ir  # scripted group (container) (typed FeaturePython)
  Dunit = g/cm3
  Dvalue = 22.42
  Group = -> [Ir_element001]
  conduct = 2
  density = 1
  expand = 3
  formula = Ir
  name = G4_Ir
  specific = 4
FEATURE [App::DocumentObjectGroupPython] Pt_element001  label="Pt_element : 1"  # scripted group (container) (typed FeaturePython)
  n = 1
  ref = Pt_element
FEATURE [App::DocumentObjectGroupPython] G4_Pt  # scripted group (container) (typed FeaturePython)
  Dunit = g/cm3
  Dvalue = 21.45
  Group = -> [Pt_element001]
  conduct = 2
  density = 1
  expand = 3
  formula = Pt
  name = G4_Pt
  specific = 4
FEATURE [App::DocumentObjectGroupPython] Au_element001  label="Au_element : 1"  # scripted group (container) (typed FeaturePython)
  n = 1
  ref = Au_element
FEATURE [App::DocumentObjectGroupPython] G4_Au  # scripted group (container) (typed FeaturePython)
  Dunit = g/cm3
  Dvalue = 19.32
  Group = -> [Au_element001]
  conduct = 2
  density = 1
  expand = 3
  formula = Au
  name = G4_Au
  specific = 4
FEATURE [App::DocumentObjectGroupPython] Hg_element002  label="Hg_element : 002"  # scripted group (container) (typed FeaturePython)
  n = 1
  ref = Hg_element
FEATURE [App::DocumentObjectGroupPython] G4_Hg  # scripted group (container) (typed FeaturePython)
  Dunit = g/cm3
  Dvalue = 13.546
  Group = -> [Hg_element002]
  conduct = 2
  density = 1
  expand = 3
  formula = Hg
  name = G4_Hg
  specific = 4
FEATURE [App::DocumentObjectGroupPython] Tl_element002  label="Tl_element : 002"  # scripted group (container) (typed FeaturePython)
  n = 1
  ref = Tl_element
FEATURE [App::DocumentObjectGroupPython] G4_Tl  # scripted group (container) (typed FeaturePython)
  Dunit = g/cm3
  Dvalue = 11.72
  Group = -> [Tl_element002]
  conduct = 2
  density = 1
  expand = 3
  formula = Tl
  name = G4_Tl
  specific = 4
FEATURE [App::DocumentObjectGroupPython] Pb_element003  label="Pb_element : 1"  # scripted group (container) (typed FeaturePython)
  n = 1
  ref = Pb_element
FEATURE [App::DocumentObjectGroupPython] G4_Pb  # scripted group (container) (typed FeaturePython)
  Dunit = g/cm3
  Dvalue = 11.35
  Group = -> [Pb_element003]
  conduct = 2
  density = 1
  expand = 3
  formula = Pb
  name = G4_Pb
  specific = 4
FEATURE [App::DocumentObjectGroupPython] Bi_element002  label="Bi_element : 1"  # scripted group (container) (typed FeaturePython)
  n = 1
  ref = Bi_element
FEATURE [App::DocumentObjectGroupPython] G4_Bi  # scripted group (container) (typed FeaturePython)
  Dunit = g/cm3
  Dvalue = 9.747
  Group = -> [Bi_element002]
  conduct = 2
  density = 1
  expand = 3
  formula = Bi
  name = G4_Bi
  specific = 4
FEATURE [App::DocumentObjectGroupPython] Po_element001  label="Po_element : 1"  # scripted group (container) (typed FeaturePython)
  n = 1
  ref = Po_element
FEATURE [App::DocumentObjectGroupPython] G4_Po  # scripted group (container) (typed FeaturePython)
  Dunit = g/cm3
  Dvalue = 9.32
  Group = -> [Po_element001]
  conduct = 2
  density = 1
  expand = 3
  formula = Po
  name = G4_Po
  specific = 4
FEATURE [App::DocumentObjectGroupPython] At_element001  label="At_element : 1"  # scripted group (container) (typed FeaturePython)
  n = 1
  ref = At_element
FEATURE [App::DocumentObjectGroupPython] G4_At  # scripted group (container) (typed FeaturePython)
  Dunit = g/cm3
  Dvalue = 9.32
  Group = -> [At_element001]
  conduct = 2
  density = 1
  expand = 3
  formula = At
  name = G4_At
  specific = 4
FEATURE [App::DocumentObjectGroupPython] Rn_element001  label="Rn_element : 1"  # scripted group (container) (typed FeaturePython)
  n = 1
  ref = Rn_element
FEATURE [App::DocumentObjectGroupPython] G4_Rn  # scripted group (container) (typed FeaturePython)
  Dunit = g/cm3
  Dvalue = 0.00900662
  Group = -> [Rn_element001]
  conduct = 2
  density = 1
  expand = 3
  formula = Rn
  name = G4_Rn
  specific = 4
FEATURE [App::DocumentObjectGroupPython] Fr_element001  label="Fr_element : 1"  # scripted group (container) (typed FeaturePython)
  n = 1
  ref = Fr_element
FEATURE [App::DocumentObjectGroupPython] G4_Fr  # scripted group (container) (typed FeaturePython)
  Dunit = g/cm3
  Dvalue = 1
  Group = -> [Fr_element001]
  conduct = 2
  density = 1
  expand = 3
  formula = Fr
  name = G4_Fr
  specific = 4
FEATURE [App::DocumentObjectGroupPython] Ra_element001  label="Ra_element : 1"  # scripted group (container) (typed FeaturePython)
  n = 1
  ref = Ra_element
FEATURE [App::DocumentObjectGroupPython] G4_Ra  # scripted group (container) (typed FeaturePython)
  Dunit = g/cm3
  Dvalue = 5
  Group = -> [Ra_element001]
  conduct = 2
  density = 1
  expand = 3
  formula = Ra
  name = G4_Ra
  specific = 4
FEATURE [App::DocumentObjectGroupPython] Ac_element001  label="Ac_element : 1"  # scripted group (container) (typed FeaturePython)
  n = 1
  ref = Ac_element
FEATURE [App::DocumentObjectGroupPython] G4_Ac  # scripted group (container) (typed FeaturePython)
  Dunit = g/cm3
  Dvalue = 10.07
  Group = -> [Ac_element001]
  conduct = 2
  density = 1
  expand = 3
  formula = Ac
  name = G4_Ac
  specific = 4
FEATURE [App::DocumentObjectGroupPython] Th_element001  label="Th_element : 1"  # scripted group (container) (typed FeaturePython)
  n = 1
  ref = Th_element
FEATURE [App::DocumentObjectGroupPython] G4_Th  # scripted group (container) (typed FeaturePython)
  Dunit = g/cm3
  Dvalue = 11.72
  Group = -> [Th_element001]
  conduct = 2
  density = 1
  expand = 3
  formula = Th
  name = G4_Th
  specific = 4
FEATURE [App::DocumentObjectGroupPython] Pa_element001  label="Pa_element : 1"  # scripted group (container) (typed FeaturePython)
  n = 1
  ref = Pa_element
FEATURE [App::DocumentObjectGroupPython] G4_Pa  # scripted group (container) (typed FeaturePython)
  Dunit = g/cm3
  Dvalue = 15.37
  Group = -> [Pa_element001]
  conduct = 2
  density = 1
  expand = 3
  formula = Pa
  name = G4_Pa
  specific = 4
FEATURE [App::DocumentObjectGroupPython] U_element004  label="U_element : 004"  # scripted group (container) (typed FeaturePython)
  n = 1
  ref = U_element
FEATURE [App::DocumentObjectGroupPython] G4_U  # scripted group (container) (typed FeaturePython)
  Dunit = g/cm3
  Dvalue = 18.95
  Group = -> [U_element004]
  conduct = 2
  density = 1
  expand = 3
  formula = U
  name = G4_U
  specific = 4
FEATURE [App::DocumentObjectGroupPython] Np_element001  label="Np_element : 1"  # scripted group (container) (typed FeaturePython)
  n = 1
  ref = Np_element
FEATURE [App::DocumentObjectGroupPython] G4_Np  # scripted group (container) (typed FeaturePython)
  Dunit = g/cm3
  Dvalue = 20.25
  Group = -> [Np_element001]
  conduct = 2
  density = 1
  expand = 3
  formula = Np
  name = G4_Np
  specific = 4
FEATURE [App::DocumentObjectGroupPython] Pu_element002  label="Pu_element : 002"  # scripted group (container) (typed FeaturePython)
  n = 1
  ref = Pu_element
FEATURE [App::DocumentObjectGroupPython] G4_Pu  # scripted group (container) (typed FeaturePython)
  Dunit = g/cm3
  Dvalue = 19.84
  Group = -> [Pu_element002]
  conduct = 2
  density = 1
  expand = 3
  formula = Pu
  name = G4_Pu
  specific = 4
FEATURE [App::DocumentObjectGroupPython] Am_element001  label="Am_element : 1"  # scripted group (container) (typed FeaturePython)
  n = 1
  ref = Am_element
FEATURE [App::DocumentObjectGroupPython] G4_Am  # scripted group (container) (typed FeaturePython)
  Dunit = g/cm3
  Dvalue = 13.67
  Group = -> [Am_element001]
  conduct = 2
  density = 1
  expand = 3
  formula = Am
  name = G4_Am
  specific = 4
FEATURE [App::DocumentObjectGroupPython] Cm_element001  label="Cm_element : 1"  # scripted group (container) (typed FeaturePython)
  n = 1
  ref = Cm_element
FEATURE [App::DocumentObjectGroupPython] G4_Cm  # scripted group (container) (typed FeaturePython)
  Dunit = g/cm3
  Dvalue = 13.51
  Group = -> [Cm_element001]
  conduct = 2
  density = 1
  expand = 3
  formula = Cm
  name = G4_Cm
  specific = 4
FEATURE [App::DocumentObjectGroupPython] Bk_element001  label="Bk_element : 1"  # scripted group (container) (typed FeaturePython)
  n = 1
  ref = Bk_element
FEATURE [App::DocumentObjectGroupPython] G4_Bk  # scripted group (container) (typed FeaturePython)
  Dunit = g/cm3
  Dvalue = 14
  Group = -> [Bk_element001]
  conduct = 2
  density = 1
  expand = 3
  formula = Bk
  name = G4_Bk
  specific = 4
FEATURE [App::DocumentObjectGroupPython] Cf_element001  label="Cf_element : 1"  # scripted group (container) (typed FeaturePython)
  n = 1
  ref = Cf_element
FEATURE [App::DocumentObjectGroupPython] G4_Cf  # scripted group (container) (typed FeaturePython)
  Dunit = g/cm3
  Dvalue = 10
  Group = -> [Cf_element001]
  conduct = 2
  density = 1
  expand = 3
  formula = Cf
  name = G4_Cf
  specific = 4
FEATURE [App::DocumentObjectGroupPython] Element  # scripted group (container) (typed FeaturePython)
  Group = -> [G4_H,G4_He,G4_Li,G4_Be,G4_B,G4_C,G4_N,G4_O,G4_F,G4_Ne,G4_Na,G4_Mg,G4_Al,G4_Si,G4_P,G4_S,G4_Cl,G4_Ar,G4_K,G4_Ca,G4_Sc,G4_Ti,G4_V,G4_Cr,G4_Mn,G4_Fe,G4_Co,G4_Ni,G4_Cu,G4_Zn,G4_Ga,G4_Ge,G4_As,G4_Se,G4_Br,G4_Kr,G4_Rb,G4_Sr,G4_Y,G4_Zr,G4_Nb,G4_Mo,G4_Tc,G4_Ru,G4_Rh,G4_Pd,G4_Ag,G4_Cd,G4_In,G4_Sn,G4_Sb,G4_Te,G4_I,G4_Xe,G4_Cs,G4_Ba,G4_La,G4_Ce,G4_Pr,G4_Nd,G4_Pm,G4_Sm,G4_Eu,G4_Gd,G4_Tb,G4_Dy,G4_Ho,G4_Er,+30 more]
FEATURE [App::DocumentObjectGroupPython] H_element114  label="H_element : 063"  # scripted group (container) (typed FeaturePython)
  n = 2
  ref = H_element
FEATURE [App::DocumentObjectGroupPython] G4_lH2  # scripted group (container) (typed FeaturePython)
  Dunit = g/cm3
  Dvalue = 0.0708
  Group = -> [H_element114]
  conduct = 2
  density = 1
  expand = 3
  formula = G4_lH2
  name = G4_lH2
  specific = 4
FEATURE [App::DocumentObjectGroupPython] N_element049  label="N_element : 022"  # scripted group (container) (typed FeaturePython)
  n = 2
  ref = N_element
FEATURE [App::DocumentObjectGroupPython] G4_lN2  # scripted group (container) (typed FeaturePython)
  Dunit = g/cm3
  Dvalue = 0.807
  Group = -> [N_element049]
  conduct = 2
  density = 1
  expand = 3
  formula = G4_lN2
  name = G4_lN2
  specific = 4
FEATURE [App::DocumentObjectGroupPython] O_element106  label="O_element : 060"  # scripted group (container) (typed FeaturePython)
  n = 2
  ref = O_element
FEATURE [App::DocumentObjectGroupPython] G4_lO2  # scripted group (container) (typed FeaturePython)
  Dunit = g/cm3
  Dvalue = 1.141
  Group = -> [O_element106]
  conduct = 2
  density = 1
  expand = 3
  formula = G4_lO2
  name = G4_lO2
  specific = 4
FEATURE [App::DocumentObjectGroupPython] Ar_element003  label="Ar_element : 002"  # scripted group (container) (typed FeaturePython)
  n = 1
  ref = Ar_element
FEATURE [App::DocumentObjectGroupPython] G4_lAr  # scripted group (container) (typed FeaturePython)
  Dunit = g/cm3
  Dvalue = 1.396
  Group = -> [Ar_element003]
  conduct = 2
  density = 1
  expand = 3
  formula = G4_lAr
  name = G4_lAr
  specific = 4
FEATURE [App::DocumentObjectGroupPython] Br_element008  label="Br_element : 005"  # scripted group (container) (typed FeaturePython)
  n = 1
  ref = Br_element
FEATURE [App::DocumentObjectGroupPython] G4_lBr  # scripted group (container) (typed FeaturePython)
  Dunit = g/cm3
  Dvalue = 3.1028
  Group = -> [Br_element008]
  conduct = 2
  density = 1
  expand = 3
  formula = G4_lBr
  name = G4_lBr
  specific = 4
FEATURE [App::DocumentObjectGroupPython] Kr_element002  label="Kr_element : 002"  # scripted group (container) (typed FeaturePython)
  n = 1
  ref = Kr_element
FEATURE [App::DocumentObjectGroupPython] G4_lKr  # scripted group (container) (typed FeaturePython)
  Dunit = g/cm3
  Dvalue = 2.418
  Group = -> [Kr_element002]
  conduct = 2
  density = 1
  expand = 3
  formula = G4_lKr
  name = G4_lKr
  specific = 4
FEATURE [App::DocumentObjectGroupPython] Xe_element002  label="Xe_element : 002"  # scripted group (container) (typed FeaturePython)
  n = 1
  ref = Xe_element
FEATURE [App::DocumentObjectGroupPython] G4_lXe  # scripted group (container) (typed FeaturePython)
  Dunit = g/cm3
  Dvalue = 2.953
  Group = -> [Xe_element002]
  conduct = 2
  density = 1
  expand = 3
  formula = G4_lXe
  name = G4_lXe
  specific = 4
FEATURE [App::DocumentObjectGroupPython] O_element107  label="O_element : 061"  # scripted group (container) (typed FeaturePython)
  n = 4
  ref = O_element
FEATURE [App::DocumentObjectGroupPython] Pb_element004  label="Pb_element : 002"  # scripted group (container) (typed FeaturePython)
  n = 1
  ref = Pb_element
FEATURE [App::DocumentObjectGroupPython] W_element005  label="W_element : 005"  # scripted group (container) (typed FeaturePython)
  n = 1
  ref = W_element
FEATURE [App::DocumentObjectGroupPython] G4_PbWO4  # scripted group (container) (typed FeaturePython)
  Dunit = g/cm3
  Dvalue = 8.28
  Group = -> [O_element107,Pb_element004,W_element005]
  conduct = 2
  density = 1
  expand = 3
  formula = G4_PbWO4
  name = G4_PbWO4
  specific = 4
FEATURE [App::DocumentObjectGroupPython] H_element115  label="H_element : 064"  # scripted group (container) (typed FeaturePython)
  n = 1
  ref = H_element
FEATURE [App::DocumentObjectGroupPython] G4_Galactic  # scripted group (container) (typed FeaturePython)
  Dunit = g/cm3
  Dvalue = 0
  Group = -> [H_element115]
  conduct = 2
  density = 1
  expand = 3
  formula = G4_Galactic
  name = G4_Galactic
  specific = 4
FEATURE [App::DocumentObjectGroupPython] C_element125  label="C_element : 071"  # scripted group (container) (typed FeaturePython)
  n = 1
  ref = C_element
FEATURE [App::DocumentObjectGroupPython] G4_GRAPHITE_POROUS  # scripted group (container) (typed FeaturePython)
  Dunit = g/cm3
  Dvalue = 1.7
  Group = -> [C_element125]
  conduct = 2
  density = 1
  expand = 3
  formula = G4_GRAPHITE_POROUS
  name = G4_GRAPHITE_POROUS
  specific = 4
FEATURE [App::DocumentObjectGroupPython] H_element116  label="H_element : 0.150"  # scripted group (container) (typed FeaturePython)
  n = 0.080538
FEATURE [App::DocumentObjectGroupPython] C_element126  label="C_element : 0.600"  # scripted group (container) (typed FeaturePython)
  n = 0.599848
FEATURE [App::DocumentObjectGroupPython] O_element108  label="O_element : 0.320"  # scripted group (container) (typed FeaturePython)
  n = 0.319614
FEATURE [App::DocumentObjectGroupPython] G4_LUCITE  # scripted group (container) (typed FeaturePython)
  Dunit = g/cm3
  Dvalue = 1.19
  Group = -> [H_element116,C_element126,O_element108]
  conduct = 2
  density = 1
  expand = 3
  formula = G4_LUCITE
  name = G4_LUCITE
  specific = 4
FEATURE [App::DocumentObjectGroupPython] Cu_element002  label="Cu_element : 62"  # scripted group (container) (typed FeaturePython)
  n = 62
  ref = Cu_element
FEATURE [App::DocumentObjectGroupPython] Zn_element002  label="Zn_element : 35"  # scripted group (container) (typed FeaturePython)
  n = 35
  ref = Zn_element
FEATURE [App::DocumentObjectGroupPython] Pb_element005  label="Pb_element : 3"  # scripted group (container) (typed FeaturePython)
  n = 3
  ref = Pb_element
FEATURE [App::DocumentObjectGroupPython] G4_BRASS  # scripted group (container) (typed FeaturePython)
  Dunit = g/cm3
  Dvalue = 8.52
  Group = -> [Cu_element002,Zn_element002,Pb_element005]
  conduct = 2
  density = 1
  expand = 3
  formula = G4_BRASS
  name = G4_BRASS
  specific = 4
FEATURE [App::DocumentObjectGroupPython] Cu_element003  label="Cu_element : 89"  # scripted group (container) (typed FeaturePython)
  n = 89
  ref = Cu_element
FEATURE [App::DocumentObjectGroupPython] Zn_element003  label="Zn_element : 9"  # scripted group (container) (typed FeaturePython)
  n = 9
  ref = Zn_element
FEATURE [App::DocumentObjectGroupPython] Pb_element006  label="Pb_element : 2"  # scripted group (container) (typed FeaturePython)
  n = 2
  ref = Pb_element
FEATURE [App::DocumentObjectGroupPython] G4_BRONZE  # scripted group (container) (typed FeaturePython)
  Dunit = g/cm3
  Dvalue = 8.82
  Group = -> [Cu_element003,Zn_element003,Pb_element006]
  conduct = 2
  density = 1
  expand = 3
  formula = G4_BRONZE
  name = G4_BRONZE
  specific = 4
FEATURE [App::DocumentObjectGroupPython] Fe_element008  label="Fe_element : 74"  # scripted group (container) (typed FeaturePython)
  n = 74
  ref = Fe_element
FEATURE [App::DocumentObjectGroupPython] Cr_element002  label="Cr_element : 18"  # scripted group (container) (typed FeaturePython)
  n = 18
  ref = Cr_element
FEATURE [App::DocumentObjectGroupPython] Ni_element002  label="Ni_element : 8"  # scripted group (container) (typed FeaturePython)
  n = 8
  ref = Ni_element
FEATURE [App::DocumentObjectGroupPython] G4_STAINLESS_STEEL  label="G4_STAINLESS-STEEL"  # scripted group (container) (typed FeaturePython)
  Dunit = g/cm3
  Dvalue = 8
  Group = -> [Fe_element008,Cr_element002,Ni_element002]
  conduct = 2
  density = 1
  expand = 3
  formula = G4_STAINLESS-STEEL
  name = G4_STAINLESS-STEEL
  specific = 4
FEATURE [App::DocumentObjectGroupPython] H_element117  label="H_element : 065"  # scripted group (container) (typed FeaturePython)
  n = 18
  ref = H_element
FEATURE [App::DocumentObjectGroupPython] C_element127  label="C_element : 072"  # scripted group (container) (typed FeaturePython)
  n = 12
  ref = C_element
FEATURE [App::DocumentObjectGroupPython] O_element109  label="O_element : 062"  # scripted group (container) (typed FeaturePython)
  n = 7
  ref = O_element
FEATURE [App::DocumentObjectGroupPython] G4_CR39  # scripted group (container) (typed FeaturePython)
  Dunit = g/cm3
  Dvalue = 1.32
  Group = -> [H_element117,C_element127,O_element109]
  conduct = 2
  density = 1
  expand = 3
  formula = G4_CR39
  name = G4_CR39
  specific = 4
FEATURE [App::DocumentObjectGroupPython] H_element118  label="H_element : 38"  # scripted group (container) (typed FeaturePython)
  n = 38
  ref = H_element
FEATURE [App::DocumentObjectGroupPython] C_element128  label="C_element : 073"  # scripted group (container) (typed FeaturePython)
  n = 18
  ref = C_element
FEATURE [App::DocumentObjectGroupPython] O_element110  label="O_element : 063"  # scripted group (container) (typed FeaturePython)
  n = 1
  ref = O_element
FEATURE [App::DocumentObjectGroupPython] G4_OCTADECANOL  # scripted group (container) (typed FeaturePython)
  Dunit = g/cm3
  Dvalue = 0.812
  Group = -> [H_element118,C_element128,O_element110]
  conduct = 2
  density = 1
  expand = 3
  formula = G4_OCTADECANOL
  name = G4_OCTADECANOL
  specific = 4
FEATURE [App::DocumentObjectGroupPython] HEP  # scripted group (container) (typed FeaturePython)
  Group = -> [G4_lH2,G4_lN2,G4_lO2,G4_lAr,G4_lBr,G4_lKr,G4_lXe,G4_PbWO4,G4_Galactic,G4_GRAPHITE_POROUS,G4_LUCITE,G4_BRASS,G4_BRONZE,G4_STAINLESS_STEEL,G4_CR39,G4_OCTADECANOL]
FEATURE [App::DocumentObjectGroupPython] C_element129  label="C_element : 074"  # scripted group (container) (typed FeaturePython)
  n = 14
  ref = C_element
FEATURE [App::DocumentObjectGroupPython] H_element119  label="H_element : 066"  # scripted group (container) (typed FeaturePython)
  n = 10
  ref = H_element
FEATURE [App::DocumentObjectGroupPython] O_element111  label="O_element : 064"  # scripted group (container) (typed FeaturePython)
  n = 2
  ref = O_element
FEATURE [App::DocumentObjectGroupPython] N_element050  label="N_element : 023"  # scripted group (container) (typed FeaturePython)
  n = 2
  ref = N_element
FEATURE [App::DocumentObjectGroupPython] G4_KEVLAR  # scripted group (container) (typed FeaturePython)
  Dunit = g/cm3
  Dvalue = 1.44
  Group = -> [C_element129,H_element119,O_element111,N_element050]
  conduct = 2
  density = 1
  expand = 3
  formula = G4_KEVLAR
  name = G4_KEVLAR
  specific = 4
FEATURE [App::DocumentObjectGroupPython] C_element130  label="C_element : 075"  # scripted group (container) (typed FeaturePython)
  n = 10
  ref = C_element
FEATURE [App::DocumentObjectGroupPython] H_element120  label="H_element : 067"  # scripted group (container) (typed FeaturePython)
  n = 8
  ref = H_element
FEATURE [App::DocumentObjectGroupPython] O_element112  label="O_element : 065"  # scripted group (container) (typed FeaturePython)
  n = 4
  ref = O_element
FEATURE [App::DocumentObjectGroupPython] G4_DACRON  # scripted group (container) (typed FeaturePython)
  Dunit = g/cm3
  Dvalue = 1.4
  Group = -> [C_element130,H_element120,O_element112]
  conduct = 2
  density = 1
  expand = 3
  formula = G4_DACRON
  name = G4_DACRON
  specific = 4
FEATURE [App::DocumentObjectGroupPython] C_element131  label="C_element : 076"  # scripted group (container) (typed FeaturePython)
  n = 4
  ref = C_element
FEATURE [App::DocumentObjectGroupPython] H_element121  label="H_element : 068"  # scripted group (container) (typed FeaturePython)
  n = 5
  ref = H_element
FEATURE [App::DocumentObjectGroupPython] Cl_element030  label="Cl_element : 016"  # scripted group (container) (typed FeaturePython)
  n = 1
  ref = Cl_element
FEATURE [App::DocumentObjectGroupPython] G4_NEOPRENE  # scripted group (container) (typed FeaturePython)
  Dunit = g/cm3
  Dvalue = 1.23
  Group = -> [C_element131,H_element121,Cl_element030]
  conduct = 2
  density = 1
  expand = 3
  formula = G4_NEOPRENE
  name = G4_NEOPRENE
  specific = 4
FEATURE [App::DocumentObjectGroupPython] Space  # scripted group (container) (typed FeaturePython)
  Group = -> [G4_KEVLAR,G4_DACRON,G4_NEOPRENE]
FEATURE [App::DocumentObjectGroupPython] H_element122  label="H_element : 069"  # scripted group (container) (typed FeaturePython)
  n = 5
  ref = H_element
FEATURE [App::DocumentObjectGroupPython] C_element132  label="C_element : 077"  # scripted group (container) (typed FeaturePython)
  n = 4
  ref = C_element
FEATURE [App::DocumentObjectGroupPython] N_element051  label="N_element : 3"  # scripted group (container) (typed FeaturePython)
  n = 3
  ref = N_element
FEATURE [App::DocumentObjectGroupPython] O_element113  label="O_element : 066"  # scripted group (container) (typed FeaturePython)
  n = 1
  ref = O_element
FEATURE [App::DocumentObjectGroupPython] G4_CYTOSINE  # scripted group (container) (typed FeaturePython)
  Dunit = g/cm3
  Dvalue = 1.55
  Group = -> [H_element122,C_element132,N_element051,O_element113]
  conduct = 2
  density = 1
  expand = 3
  formula = G4_CYTOSINE
  name = G4_CYTOSINE
  specific = 4
FEATURE [App::DocumentObjectGroupPython] H_element123  label="H_element : 070"  # scripted group (container) (typed FeaturePython)
  n = 6
  ref = H_element
FEATURE [App::DocumentObjectGroupPython] C_element133  label="C_element : 078"  # scripted group (container) (typed FeaturePython)
  n = 5
  ref = C_element
FEATURE [App::DocumentObjectGroupPython] N_element052  label="N_element : 024"  # scripted group (container) (typed FeaturePython)
  n = 2
  ref = N_element
FEATURE [App::DocumentObjectGroupPython] O_element114  label="O_element : 067"  # scripted group (container) (typed FeaturePython)
  n = 2
  ref = O_element
FEATURE [App::DocumentObjectGroupPython] G4_THYMINE  # scripted group (container) (typed FeaturePython)
  Dunit = g/cm3
  Dvalue = 1.23
  Group = -> [H_element123,C_element133,N_element052,O_element114]
  conduct = 2
  density = 1
  expand = 3
  formula = G4_THYMINE
  name = G4_THYMINE
  specific = 4
FEATURE [App::DocumentObjectGroupPython] H_element124  label="H_element : 071"  # scripted group (container) (typed FeaturePython)
  n = 4
  ref = H_element
FEATURE [App::DocumentObjectGroupPython] C_element134  label="C_element : 079"  # scripted group (container) (typed FeaturePython)
  n = 4
  ref = C_element
FEATURE [App::DocumentObjectGroupPython] N_element053  label="N_element : 025"  # scripted group (container) (typed FeaturePython)
  n = 2
  ref = N_element
FEATURE [App::DocumentObjectGroupPython] O_element115  label="O_element : 068"  # scripted group (container) (typed FeaturePython)
  n = 2
  ref = O_element
FEATURE [App::DocumentObjectGroupPython] G4_URACIL  # scripted group (container) (typed FeaturePython)
  Dunit = g/cm3
  Dvalue = 1.32
  Group = -> [H_element124,C_element134,N_element053,O_element115]
  conduct = 2
  density = 1
  expand = 3
  formula = G4_URACIL
  name = G4_URACIL
  specific = 4
FEATURE [App::DocumentObjectGroupPython] H_element125  label="H_element : 072"  # scripted group (container) (typed FeaturePython)
  n = 4
  ref = H_element
FEATURE [App::DocumentObjectGroupPython] C_element135  label="C_element : 080"  # scripted group (container) (typed FeaturePython)
  n = 5
  ref = C_element
FEATURE [App::DocumentObjectGroupPython] N_element054  label="N_element : 026"  # scripted group (container) (typed FeaturePython)
  n = 5
  ref = N_element
FEATURE [App::DocumentObjectGroupPython] G4_DNA_ADENINE  # scripted group (container) (typed FeaturePython)
  Dunit = g/cm3
  Dvalue = 1
  Group = -> [H_element125,C_element135,N_element054]
  conduct = 2
  density = 1
  expand = 3
  formula = G4_DNA_ADENINE
  name = G4_DNA_ADENINE
  specific = 4
FEATURE [App::DocumentObjectGroupPython] H_element126  label="H_element : 073"  # scripted group (container) (typed FeaturePython)
  n = 4
  ref = H_element
FEATURE [App::DocumentObjectGroupPython] C_element136  label="C_element : 081"  # scripted group (container) (typed FeaturePython)
  n = 5
  ref = C_element
FEATURE [App::DocumentObjectGroupPython] N_element055  label="N_element : 027"  # scripted group (container) (typed FeaturePython)
  n = 5
  ref = N_element
FEATURE [App::DocumentObjectGroupPython] O_element116  label="O_element : 069"  # scripted group (container) (typed FeaturePython)
  n = 1
  ref = O_element
FEATURE [App::DocumentObjectGroupPython] G4_DNA_GUANINE  # scripted group (container) (typed FeaturePython)
  Dunit = g/cm3
  Dvalue = 1
  Group = -> [H_element126,C_element136,N_element055,O_element116]
  conduct = 2
  density = 1
  expand = 3
  formula = G4_DNA_GUANINE
  name = G4_DNA_GUANINE
  specific = 4
FEATURE [App::DocumentObjectGroupPython] H_element127  label="H_element : 074"  # scripted group (container) (typed FeaturePython)
  n = 4
  ref = H_element
FEATURE [App::DocumentObjectGroupPython] C_element137  label="C_element : 082"  # scripted group (container) (typed FeaturePython)
  n = 4
  ref = C_element
FEATURE [App::DocumentObjectGroupPython] N_element056  label="N_element : 028"  # scripted group (container) (typed FeaturePython)
  n = 3
  ref = N_element
FEATURE [App::DocumentObjectGroupPython] O_element117  label="O_element : 070"  # scripted group (container) (typed FeaturePython)
  n = 1
  ref = O_element
FEATURE [App::DocumentObjectGroupPython] G4_DNA_CYTOSINE  # scripted group (container) (typed FeaturePython)
  Dunit = g/cm3
  Dvalue = 1
  Group = -> [H_element127,C_element137,N_element056,O_element117]
  conduct = 2
  density = 1
  expand = 3
  formula = G4_DNA_CYTOSINE
  name = G4_DNA_CYTOSINE
  specific = 4
FEATURE [App::DocumentObjectGroupPython] H_element128  label="H_element : 075"  # scripted group (container) (typed FeaturePython)
  n = 5
  ref = H_element
FEATURE [App::DocumentObjectGroupPython] C_element138  label="C_element : 083"  # scripted group (container) (typed FeaturePython)
  n = 5
  ref = C_element
FEATURE [App::DocumentObjectGroupPython] N_element057  label="N_element : 029"  # scripted group (container) (typed FeaturePython)
  n = 2
  ref = N_element
FEATURE [App::DocumentObjectGroupPython] O_element118  label="O_element : 071"  # scripted group (container) (typed FeaturePython)
  n = 2
  ref = O_element
FEATURE [App::DocumentObjectGroupPython] G4_DNA_THYMINE  # scripted group (container) (typed FeaturePython)
  Dunit = g/cm3
  Dvalue = 1
  Group = -> [H_element128,C_element138,N_element057,O_element118]
  conduct = 2
  density = 1
  expand = 3
  formula = G4_DNA_THYMINE
  name = G4_DNA_THYMINE
  specific = 4
FEATURE [App::DocumentObjectGroupPython] H_element129  label="H_element : 076"  # scripted group (container) (typed FeaturePython)
  n = 3
  ref = H_element
FEATURE [App::DocumentObjectGroupPython] C_element139  label="C_element : 084"  # scripted group (container) (typed FeaturePython)
  n = 4
  ref = C_element
FEATURE [App::DocumentObjectGroupPython] N_element058  label="N_element : 030"  # scripted group (container) (typed FeaturePython)
  n = 2
  ref = N_element
FEATURE [App::DocumentObjectGroupPython] O_element119  label="O_element : 072"  # scripted group (container) (typed FeaturePython)
  n = 2
  ref = O_element
FEATURE [App::DocumentObjectGroupPython] G4_DNA_URACIL  # scripted group (container) (typed FeaturePython)
  Dunit = g/cm3
  Dvalue = 1
  Group = -> [H_element129,C_element139,N_element058,O_element119]
  conduct = 2
  density = 1
  expand = 3
  formula = G4_DNA_URACIL
  name = G4_DNA_URACIL
  specific = 4
FEATURE [App::DocumentObjectGroupPython] H_element130  label="H_element : 077"  # scripted group (container) (typed FeaturePython)
  n = 10
  ref = H_element
FEATURE [App::DocumentObjectGroupPython] C_element140  label="C_element : 085"  # scripted group (container) (typed FeaturePython)
  n = 10
  ref = C_element
FEATURE [App::DocumentObjectGroupPython] N_element059  label="N_element : 031"  # scripted group (container) (typed FeaturePython)
  n = 5
  ref = N_element
FEATURE [App::DocumentObjectGroupPython] O_element120  label="O_element : 073"  # scripted group (container) (typed FeaturePython)
  n = 4
  ref = O_element
FEATURE [App::DocumentObjectGroupPython] G4_DNA_ADENOSINE  # scripted group (container) (typed FeaturePython)
  Dunit = g/cm3
  Dvalue = 1
  Group = -> [H_element130,C_element140,N_element059,O_element120]
  conduct = 2
  density = 1
  expand = 3
  formula = G4_DNA_ADENOSINE
  name = G4_DNA_ADENOSINE
  specific = 4
FEATURE [App::DocumentObjectGroupPython] H_element131  label="H_element : 078"  # scripted group (container) (typed FeaturePython)
  n = 10
  ref = H_element
FEATURE [App::DocumentObjectGroupPython] C_element141  label="C_element : 086"  # scripted group (container) (typed FeaturePython)
  n = 10
  ref = C_element
FEATURE [App::DocumentObjectGroupPython] N_element060  label="N_element : 032"  # scripted group (container) (typed FeaturePython)
  n = 5
  ref = N_element
FEATURE [App::DocumentObjectGroupPython] O_element121  label="O_element : 074"  # scripted group (container) (typed FeaturePython)
  n = 5
  ref = O_element
FEATURE [App::DocumentObjectGroupPython] G4_DNA_GUANOSINE  # scripted group (container) (typed FeaturePython)
  Dunit = g/cm3
  Dvalue = 1
  Group = -> [H_element131,C_element141,N_element060,O_element121]
  conduct = 2
  density = 1
  expand = 3
  formula = G4_DNA_GUANOSINE
  name = G4_DNA_GUANOSINE
  specific = 4
FEATURE [App::DocumentObjectGroupPython] H_element132  label="H_element : 079"  # scripted group (container) (typed FeaturePython)
  n = 10
  ref = H_element
FEATURE [App::DocumentObjectGroupPython] C_element142  label="C_element : 087"  # scripted group (container) (typed FeaturePython)
  n = 9
  ref = C_element
FEATURE [App::DocumentObjectGroupPython] N_element061  label="N_element : 033"  # scripted group (container) (typed FeaturePython)
  n = 3
  ref = N_element
FEATURE [App::DocumentObjectGroupPython] O_element122  label="O_element : 075"  # scripted group (container) (typed FeaturePython)
  n = 5
  ref = O_element
FEATURE [App::DocumentObjectGroupPython] G4_DNA_CYTIDINE  # scripted group (container) (typed FeaturePython)
  Dunit = g/cm3
  Dvalue = 1
  Group = -> [H_element132,C_element142,N_element061,O_element122]
  conduct = 2
  density = 1
  expand = 3
  formula = G4_DNA_CYTIDINE
  name = G4_DNA_CYTIDINE
  specific = 4
FEATURE [App::DocumentObjectGroupPython] H_element133  label="H_element : 080"  # scripted group (container) (typed FeaturePython)
  n = 9
  ref = H_element
FEATURE [App::DocumentObjectGroupPython] C_element143  label="C_element : 088"  # scripted group (container) (typed FeaturePython)
  n = 9
  ref = C_element
FEATURE [App::DocumentObjectGroupPython] N_element062  label="N_element : 034"  # scripted group (container) (typed FeaturePython)
  n = 2
  ref = N_element
FEATURE [App::DocumentObjectGroupPython] O_element123  label="O_element : 076"  # scripted group (container) (typed FeaturePython)
  n = 6
  ref = O_element
FEATURE [App::DocumentObjectGroupPython] G4_DNA_URIDINE  # scripted group (container) (typed FeaturePython)
  Dunit = g/cm3
  Dvalue = 1
  Group = -> [H_element133,C_element143,N_element062,O_element123]
  conduct = 2
  density = 1
  expand = 3
  formula = G4_DNA_URIDINE
  name = G4_DNA_URIDINE
  specific = 4
FEATURE [App::DocumentObjectGroupPython] H_element134  label="H_element : 081"  # scripted group (container) (typed FeaturePython)
  n = 11
  ref = H_element
FEATURE [App::DocumentObjectGroupPython] C_element144  label="C_element : 089"  # scripted group (container) (typed FeaturePython)
  n = 10
  ref = C_element
FEATURE [App::DocumentObjectGroupPython] N_element063  label="N_element : 035"  # scripted group (container) (typed FeaturePython)
  n = 2
  ref = N_element
FEATURE [App::DocumentObjectGroupPython] O_element124  label="O_element : 077"  # scripted group (container) (typed FeaturePython)
  n = 6
  ref = O_element
FEATURE [App::DocumentObjectGroupPython] G4_DNA_METHYLURIDINE  # scripted group (container) (typed FeaturePython)
  Dunit = g/cm3
  Dvalue = 1
  Group = -> [H_element134,C_element144,N_element063,O_element124]
  conduct = 2
  density = 1
  expand = 3
  formula = G4_DNA_METHYLURIDINE
  name = G4_DNA_METHYLURIDINE
  specific = 4
FEATURE [App::DocumentObjectGroupPython] P_element014  label="P_element : 003"  # scripted group (container) (typed FeaturePython)
  n = 1
  ref = P_element
FEATURE [App::DocumentObjectGroupPython] O_element125  label="O_element : 078"  # scripted group (container) (typed FeaturePython)
  n = 3
  ref = O_element
FEATURE [App::DocumentObjectGroupPython] G4_DNA_MONOPHOSPHATE  # scripted group (container) (typed FeaturePython)
  Dunit = g/cm3
  Dvalue = 1
  Group = -> [P_element014,O_element125]
  conduct = 2
  density = 1
  expand = 3
  formula = G4_DNA_MONOPHOSPHATE
  name = G4_DNA_MONOPHOSPHATE
  specific = 4
FEATURE [App::DocumentObjectGroupPython] H_element135  label="H_element : 082"  # scripted group (container) (typed FeaturePython)
  n = 10
  ref = H_element
FEATURE [App::DocumentObjectGroupPython] C_element145  label="C_element : 090"  # scripted group (container) (typed FeaturePython)
  n = 10
  ref = C_element
FEATURE [App::DocumentObjectGroupPython] N_element064  label="N_element : 036"  # scripted group (container) (typed FeaturePython)
  n = 5
  ref = N_element
FEATURE [App::DocumentObjectGroupPython] O_element126  label="O_element : 079"  # scripted group (container) (typed FeaturePython)
  n = 7
  ref = O_element
FEATURE [App::DocumentObjectGroupPython] P_element015  label="P_element : 004"  # scripted group (container) (typed FeaturePython)
  n = 1
  ref = P_element
FEATURE [App::DocumentObjectGroupPython] G4_DNA_A  # scripted group (container) (typed FeaturePython)
  Dunit = g/cm3
  Dvalue = 1
  Group = -> [H_element135,C_element145,N_element064,O_element126,P_element015]
  conduct = 2
  density = 1
  expand = 3
  formula = G4_DNA_A
  name = G4_DNA_A
  specific = 4
FEATURE [App::DocumentObjectGroupPython] H_element136  label="H_element : 083"  # scripted group (container) (typed FeaturePython)
  n = 10
  ref = H_element
FEATURE [App::DocumentObjectGroupPython] C_element146  label="C_element : 091"  # scripted group (container) (typed FeaturePython)
  n = 10
  ref = C_element
FEATURE [App::DocumentObjectGroupPython] N_element065  label="N_element : 037"  # scripted group (container) (typed FeaturePython)
  n = 5
  ref = N_element
FEATURE [App::DocumentObjectGroupPython] O_element127  label="O_element : 8"  # scripted group (container) (typed FeaturePython)
  n = 8
  ref = O_element
FEATURE [App::DocumentObjectGroupPython] P_element016  label="P_element : 005"  # scripted group (container) (typed FeaturePython)
  n = 1
  ref = P_element
FEATURE [App::DocumentObjectGroupPython] G4_DNA_G  # scripted group (container) (typed FeaturePython)
  Dunit = g/cm3
  Dvalue = 1
  Group = -> [H_element136,C_element146,N_element065,O_element127,P_element016]
  conduct = 2
  density = 1
  expand = 3
  formula = G4_DNA_G
  name = G4_DNA_G
  specific = 4
FEATURE [App::DocumentObjectGroupPython] H_element137  label="H_element : 084"  # scripted group (container) (typed FeaturePython)
  n = 10
  ref = H_element
FEATURE [App::DocumentObjectGroupPython] C_element147  label="C_element : 092"  # scripted group (container) (typed FeaturePython)
  n = 9
  ref = C_element
FEATURE [App::DocumentObjectGroupPython] N_element066  label="N_element : 038"  # scripted group (container) (typed FeaturePython)
  n = 3
  ref = N_element
FEATURE [App::DocumentObjectGroupPython] O_element128  label="O_element : 080"  # scripted group (container) (typed FeaturePython)
  n = 8
  ref = O_element
FEATURE [App::DocumentObjectGroupPython] P_element017  label="P_element : 006"  # scripted group (container) (typed FeaturePython)
  n = 1
  ref = P_element
FEATURE [App::DocumentObjectGroupPython] G4_DNA_C  # scripted group (container) (typed FeaturePython)
  Dunit = g/cm3
  Dvalue = 1
  Group = -> [H_element137,C_element147,N_element066,O_element128,P_element017]
  conduct = 2
  density = 1
  expand = 3
  formula = G4_DNA_C
  name = G4_DNA_C
  specific = 4
FEATURE [App::DocumentObjectGroupPython] H_element138  label="H_element : 085"  # scripted group (container) (typed FeaturePython)
  n = 9
  ref = H_element
FEATURE [App::DocumentObjectGroupPython] C_element148  label="C_element : 093"  # scripted group (container) (typed FeaturePython)
  n = 9
  ref = C_element
FEATURE [App::DocumentObjectGroupPython] N_element067  label="N_element : 039"  # scripted group (container) (typed FeaturePython)
  n = 2
  ref = N_element
FEATURE [App::DocumentObjectGroupPython] O_element129  label="O_element : 9"  # scripted group (container) (typed FeaturePython)
  n = 9
  ref = O_element
FEATURE [App::DocumentObjectGroupPython] P_element018  label="P_element : 007"  # scripted group (container) (typed FeaturePython)
  n = 1
  ref = P_element
FEATURE [App::DocumentObjectGroupPython] G4_DNA_U  # scripted group (container) (typed FeaturePython)
  Dunit = g/cm3
  Dvalue = 1
  Group = -> [H_element138,C_element148,N_element067,O_element129,P_element018]
  conduct = 2
  density = 1
  expand = 3
  formula = G4_DNA_U
  name = G4_DNA_U
  specific = 4
FEATURE [App::DocumentObjectGroupPython] H_element139  label="H_element : 086"  # scripted group (container) (typed FeaturePython)
  n = 11
  ref = H_element
FEATURE [App::DocumentObjectGroupPython] C_element149  label="C_element : 094"  # scripted group (container) (typed FeaturePython)
  n = 10
  ref = C_element
FEATURE [App::DocumentObjectGroupPython] N_element068  label="N_element : 040"  # scripted group (container) (typed FeaturePython)
  n = 2
  ref = N_element
FEATURE [App::DocumentObjectGroupPython] O_element130  label="O_element : 081"  # scripted group (container) (typed FeaturePython)
  n = 9
  ref = O_element
FEATURE [App::DocumentObjectGroupPython] P_element019  label="P_element : 008"  # scripted group (container) (typed FeaturePython)
  n = 1
  ref = P_element
FEATURE [App::DocumentObjectGroupPython] G4_DNA_MU  # scripted group (container) (typed FeaturePython)
  Dunit = g/cm3
  Dvalue = 1
  Group = -> [H_element139,C_element149,N_element068,O_element130,P_element019]
  conduct = 2
  density = 1
  expand = 3
  formula = G4_DNA_MU
  name = G4_DNA_MU
  specific = 4
FEATURE [App::DocumentObjectGroupPython] BioChemical  # scripted group (container) (typed FeaturePython)
  Group = -> [G4_CYTOSINE,G4_THYMINE,G4_URACIL,G4_DNA_ADENINE,G4_DNA_GUANINE,G4_DNA_CYTOSINE,G4_DNA_THYMINE,G4_DNA_URACIL,G4_DNA_ADENOSINE,G4_DNA_GUANOSINE,G4_DNA_CYTIDINE,G4_DNA_URIDINE,G4_DNA_METHYLURIDINE,G4_DNA_MONOPHOSPHATE,G4_DNA_A,G4_DNA_G,G4_DNA_C,G4_DNA_U,G4_DNA_MU]
FEATURE [App::DocumentObjectGroupPython] G4Materials  # scripted group (container) (typed FeaturePython)
  Group = -> [NIST,Element,HEP,Space,BioChemical]
  version = 1
FEATURE [App::DocumentObjectGroupPython] Geant4  # scripted group (container) (typed FeaturePython)
  Group = -> [G4Isotopes,G4Elements,G4Materials]
FEATURE [App::DocumentObjectGroupPython] Materials  # scripted group (container) (typed FeaturePython)
  Group = -> [Geant4]
FEATURE [Part::FeaturePython] GDMLBox_WorldBox  # WARN: FeaturePython — macro-defined, semantics opaque (R4)
  lunit = 2
  material = 5
  x = 100
  y = 100
  z = 100
FEATURE [Part::FeaturePython] GDMLBox_Box  # WARN: FeaturePython — macro-defined, semantics opaque (R4)
  Placement = pos=(30,0,0) rot=(0,0,1;0rad)
  lunit = 2
  material = 0
  x = 10
  y = 10
  z = 10
FEATURE [Part::FeaturePython] GDMLTorus  # WARN: FeaturePython — macro-defined, semantics opaque (R4)
  Placement = pos=(30,0,0) rot=(0,1,0;1.5708rad)
  aunit = deg
  deltaphi = 360
  lunit = 2
  material = 0
  rmax = 2
  rmin = 0
  rtor = 8
  startphi = 0
FEATURE [Part::MultiFuse] Fusion
  Shapes = -> [GDMLBox_Box,GDMLTorus]
FEATURE [Part::FeaturePython] Array  # Draft array (typed FeaturePython)
  AlwaysSyncPlacement = false
  Angle = 180
  ArrayType = 1
  Axis = (0,0,1)
  Base = -> Fusion
  Center = (0,0,0)
  Count = 5
  ExpandArray = false
  Fuse = false
  IntervalAxis = (0,0,0)
  IntervalX = (50,0,0)
  IntervalY = (0,50,0)
  IntervalZ = (0,0,50)
  NumberCircles = 3
  NumberPolar = 5
  NumberX = 2
  NumberY = 2
  NumberZ = 1
  PlacementList = 5 placements: [(0,0,0),(0,0,0),(0,0,0),(0,0,0),(0,0,0)]
  RadialDistance = 50
  ScaleList = (5) [(1,1,1),(1,1,1),(1,1,1),(1,1,1),(1,1,1)]
  Symmetry = 1
  TangentialDistance = 25
FEATURE [Part::FeaturePython] Array001  # Draft array (typed FeaturePython)
  AlwaysSyncPlacement = false
  Angle = 360
  ArrayType = 0
  Axis = (0,0,1)
  Base = -> Array
  Center = (0,0,0)
  Count = 4
  ExpandArray = false
  Fuse = true
  IntervalAxis = (0,0,0)
  IntervalX = (120,0,0)
  IntervalY = (0,120,0)
  IntervalZ = (0,0,100)
  NumberCircles = 3
  NumberPolar = 5
  NumberX = 2
  NumberY = 2
  NumberZ = 1
  PlacementList = 4 placements: [(0,0,0),(0,120,0),(120,0,0),(120,120,0)]
  RadialDistance = 50
  ScaleList = (4) [(1,1,1),(1,1,1),(1,1,1),(1,1,1)]
  Symmetry = 1
  TangentialDistance = 25
FEATURE [App::Part] Part001
  Group = -> [Array,GDMLBox_Box,GDMLTorus,Fusion,Array001]
  Origin = -> Origin004
FEATURE [App::Part] worldVOL
  Group = -> [GDMLBox_WorldBox,Part001]
  Origin = -> Origin
